FCSTD DOCUMENT  (FreeCAD 0.21R33771 (Git))
Label: RaspberryPi_Pico_Variations
Comment: https://gitlab.com/recursivenomad/ki-lime-pi-pico/
License: MIT-0 OR CC0-1.0
LicenseURL: https://opensource.org/license/mit-0/
objects: App::Link×368, App::LinkElement×80, App::DocumentObjectGroup×37, App::Part×36, PartDesign::Pad×35, Part::Compound×32, Sketcher::SketchObject×29, PartDesign::Mirrored×25, Part::Part2DObjectPython×21, PartDesign::LinearPattern×21, PartDesign::Pocket×16, PartDesign::Body×15, Part::FeaturePython×15, Part::Box×14, PartDesign::MultiTransform×11, Spreadsheet::Sheet×7, PartDesign::Point×5, Part::MultiFuse×5, Part::Cut×4, PartDesign::Fillet×3, +7 more types

FEATURE [Sketcher::SketchObject] Sketch  label="Sketch_Header_BodyQuadrant"
  FullyConstrained = true
  MapMode = 5
  Support = -> [XY_Plane005]
  expr: Constraints[15] = Spreadsheet002.InsulationEdgeToPin
  expr: Constraints[16] = <<vHeader>>.InsulationWidth
  expr: Constraints[29] = <<vPico>>.PinPitch * 2
  expr: Constraints[30] = Spreadsheet002.BodyOuterCrossbarInset + <<vHeader>>.InsulationWidth / 2
  expr: Constraints[32] = <<vPico>>.BoardWidth / 2 - <<vPico>>.PinInset
  expr: Constraints[33] = (<<vPico>>.PinDIPCount / 4 - 0.5) * <<vPico>>.PinPitch
  sketch-geometry (12):
    g0: LineSegment StartX=-10.16 StartY=25 StartZ=0 EndX=-7.62 EndY=25 EndZ=0
    g1: LineSegment StartX=-7.62 StartY=25 StartZ=0 EndX=-7.62 EndY=20.066 EndZ=0
    g2: LineSegment StartX=-7.62 StartY=20.066 StartZ=0 EndX=0 EndY=20.066 EndZ=0
    g3: LineSegment StartX=-10.16 StartY=25 StartZ=0 EndX=-10.16 EndY=0 EndZ=0
    g4: LineSegment StartX=-7.62 StartY=17.526 StartZ=0 EndX=0 EndY=17.526 EndZ=0
    g5: LineSegment StartX=-7.62 StartY=17.526 StartZ=0 EndX=-7.62 EndY=2.54 EndZ=0
    g6: LineSegment StartX=-7.62 StartY=2.54 StartZ=0 EndX=0 EndY=2.54 EndZ=0
    g7: LineSegment StartX=-8.89 StartY=24.13 StartZ=0 EndX=-8.89 EndY=25 EndZ=0
    g8: LineSegment StartX=-10.16 StartY=0 StartZ=0 EndX=0 EndY=0 EndZ=0
    g9: LineSegment StartX=0 StartY=0 StartZ=0 EndX=0 EndY=2.54 EndZ=0
    g10: LineSegment StartX=0 StartY=17.526 StartZ=0 EndX=0 EndY=20.066 EndZ=0
    g11: GeomPoint X=-8.89 Y=19.05 Z=0
  constraints (34):
    c: Coincident(g1,g0)
    c: Coincident(g2,g1)
    c: Coincident(g3,g0)
    c: Coincident(g5,g4)
    c: Coincident(g6,g5)
    c: Vertical(g3)
    c: Perpendicular(g0,g3)
    c: Parallel(g1,g3)
    c: PointOnObject(g4,g1)
    c: Parallel(g5,g3)
    c: Perpendicular(g3,g2)
    c: Parallel(g4,g2)
    c: Parallel(g6,g2)
    c: Perpendicular(g0,g7)
    c: Symmetric(g0,g0,g7)
    c: Distance(g7) = 0.87
    c: Distance(g0) = 2.54
    c: PointOnObject(g2,g-2)
    c: PointOnObject(g4,g-2)
    c: PointOnObject(g6,g-2)
    c: PointOnObject(g3,g-1)
    c: Coincident(g8,g3)
    c: Coincident(g8,g-1)
    c: Coincident(g9,g8)
    c: Coincident(g9,g6)
    c: Coincident(g10,g4)
    c: Coincident(g10,g2)
    c: Equal(g0,g10)
    c: PointOnObject(g11,g7)
    c: Distance(g7,g11) = 5.08
    c: Distance(g11,g4) = 1.524
    c: Equal(g9,g0)
    c: Distance(g7,g-2) = 8.89
    c: Distance(g7,g-1) = 24.13
FEATURE [PartDesign::Pad] Pad  label="Pad_Header_BodyQuadrant"
  Direction = (0,0,1)
  Length = 2.54
  Length2 = 10
  Profile = -> Sketch
  ReferenceAxis = -> Sketch [N_Axis]
  Type = 0
  expr: Length = <<vHeader>>.InsulationThickness
FEATURE [PartDesign::Mirrored] Mirrored  label="Mirror_Header_BodyQuarter"
  MirrorPlane = -> Sketch [V_Axis]
FEATURE [PartDesign::Mirrored] Mirrored001  label="Mirror_Header_BodyHalf"
  MirrorPlane = -> Sketch [H_Axis]
FEATURE [PartDesign::MultiTransform] MultiTransform  label="MultiMirror_Header_Body"
  BaseFeature = -> Pad
  Originals = -> [Pad]
  Refine = true
  Transformations = -> [Mirrored,Mirrored001]
FEATURE [PartDesign::Body] Body  label="Header_Body"
  Group = -> [Sketch,Pad,MultiTransform,Mirrored,Mirrored001]
  Origin = -> Origin005
  Tip = -> MultiTransform
FEATURE [Spreadsheet::Sheet] Spreadsheet001  label="vPico"
  cells = A1='Board Thickness; B1(BoardThickness)=1; D1='Board Corner Radius; E1(BoardCornerRadius)=0.5; G1='C1 Placement; H1='C2 Placement; I1='D1 Placement; J1='D2 Placement; K1='J1 Placement; L1='L1 Placement; M1='Q1 Placement; N1='SW1 Placement; O1='U1 Placement; P1='U2 Placement; Q1='U3 Placement; R1='X1 Placement; A2='Board Width; B2(BoardWidth)=21; D2='Board Mounting Hole Diameter; E2(BoardMountingHoleDiameter)=2.1; G2(C1Placement)==create(<<placement>>; create(<<vector>>; 2.9; 17.1; 0); create(<<rotation>>; 0; 0; 0)); H2(C2Placement)==create(<<placement>>; create(<<vector>>; 2.9; 12.1; 0); create(<<rotation>>; 0; 0; 0)); I2(D1Placement)==create(<<placement>>; create(<<vector>>; 6; 18.9; 0); create(<<rotation>>; 0; 0; 0)); J2(D2Placement)==create(<<placement>>; create(<<vector>>; -5.7; 20.7; 0); create(<<rotation>>; 0; 0; 0)); K2(J1Placement)==create(<<placement>>; create(<<vector>>; 0; BoardLength / 2 + 1.3 - .J1TabPortrusion.y - .J1BodySize.y / 2; 0); create(<<rotation>>; 0; 0; 0)); L2(L1Placement)==create(<<placement>>; create(<<vector>>; 6; 14.6; 0); create(<<rotation>>; 0; 0; 0)); M2(Q1Placement)==create(<<placement>>; create(<<vector>>; 6.4; 7.2; 0); create(<<rotation>>; 0; 0; 0)); N2(SW1Placement)==create(<<placement>>; create(<<vector>>; -3.5; 13.5; 0); create(<<rotation>>; 0; 0; 0)); O2(U1Placement)==create(<<placement>>; create(<<vector>>; 0; -0.5; 0); create(<<rotation>>; 0; 0; 0)); P2(U2Placement)==create(<<placement>>; create(<<vector>>; 2.9; 14.6; 0); create(<<rotation>>; 180; 0; 0)); Q2(U3Placement)==create(<<placement>>; create(<<vector>>; -3.8; 6.4; 0); create(<<rotation>>; 90; 0; 0)); R2(X1Placement)==create(<<placement>>; create(<<vector>>; -2.3; -9.05; 0); create(<<rotation>>; 0; 0; 0)); A3='Board Length; B3(BoardLength)=51; D3='Board Mounting Hole Margin Diameter; E3(BoardMountingHoleMarginDiameter)=3.8; G4='C1 Size; H4='C2 Size; I4='D1 Base Size; J4='D2 Base Size; K4='J1 Body Size; L4='L1 Size; M4='Q1 Size; N4='SW1 Base Size; O4='U1 Size; P4='U2 Size; Q4='U3 Size; R4='X1 Size; A5='Pin Pitch; B5(PinPitch)=2.54; D5='Pin Hole Diameter; E5(PinHoleDiameter)=1; G5(C1Size)==create(<<vector>>; 2; 1.25; 1.25); H5(C2Size)==C1Size; I5(D1BaseSize)==create(<<vector>>; 1.65; 2.7; 0.95); J5(D2BaseSize)==create(<<vector>>; 1.6; 0.8; 0.3); K5(J1BodySize)==create(<<vector>>; 7.5; 5; 2.45); L5(L1Size)==create(<<vector>>; 2; 2.5; 1.2); M5(Q1Size)==create(<<vector>>; 1.6; 0.8; 0.8); N5(SW1BaseSize)==create(<<vector>>; 3.2; 4.25; 1.6); O5(U1Size)==create(<<vector>>; 7; 7; 0.9); P5(U2Size)==create(<<vector>>; 2.5; 2.5; 0.75); Q5(U3Size)==create(<<vector>>; 3; 2; 0.6); R5(X1Size)==create(<<vector>>; 3.2; 2.5; 0.6); A6='Pin DIP Count; B6(PinDIPCount)=40; D6='Pin Pad Width; E6(PinPadWidth)=1.6; K6='// J1 part was potentially listed incorrectly on Pico datasheet schematic; listed part name in FreeCAD tree as possible true part; D7='Pin Square Pad Radius; E7(PinSquarePadRadius)=0.2; I7='D1 Lead Offset; J7='D2 Lens Offset; K7='J1 Cavity Base Width; N7='SW1 Button Offset; A8='TP AB Radius; B8(TPABRadius)=0.55; D8='Pin Inset; E8(PinInset)=1.61; I8(D1LeadOffset)==create(<<vector>>; 0; (.D1BaseSize.y + .D1LeadSize.y) / 2; 0); J8(D2LensOffset)==create(<<vector>>; 0; 0; .D2BaseSize.z); K8(J1CavityBaseWidth)=5.4; N8(SW1ButtonOffset)==create(<<vector>>; 0; 0; .SW1BaseSize.z); A9='TP AB Height; B9(TPABHeight)=1.8; D9='Pin Inset Debug; E9(PinInsetDebug)=1.6; A10='TP CD Radius; B10(TPCDRadius)=0.525; D10='Pin To Castellation Center; E10(PinToCastellationCenter)=1.6; I10='D1 Lead Size; J10='D2 Lens Size; K10='J1 Cavity Fillet Radius; N10='SW1 Button Size; A11='TP CD Height; B11(TPCDHeight)=1.45; D11='Pin Hole Rows; E11(PinHoleRows)=2; F11='// 3 so pads extend linearly over edge for cleaner model; I11(D1LeadSize)==create(<<vector>>; 0.9; (3.6 - .D1BaseSize.y) / 2; 0.15); J11(D2LensSize)==create(<<vector>>; 1; 0.8; 0.3); K11(J1CavityFilletRadius)=0.25; N11(SW1ButtonSize)==create(<<vector>>; 2.25; 1.15 + 2.25; 0.9); A13='TP Radius; B13(TPRadius)=0.3; D13='Debug Center; E13(DebugCenter)==create(<<vector>>; 0; -BoardLength / 2 + PinInsetDebug; 0); J13='D2 Phosphor Offset; K13='J1 Cavity Side Height; N13='SW1 Button Fillet Radius; A14='TP Width; B14(TPWidth)=1.5; D14='Debug Pad Depth; E14(DebugPadDepth)==BoardThickness; J14(D2PhosphorOffset)==create(<<vector>>; 0; 0; .D2BaseSize.z); K14(J1CavitySideHeight)=1.1; N14(SW1ButtonFilletRadius)=0.5; D15='Debug Square Pin Index; E15(DebugSquarePinIndex)=1; J16='D2 Phosphor Size; K16='J1 Shell Thickness; A17='TP Pos A; B17(TPPosA)==create(<<vector>>; 7.775; 49.5); J17(D2PhosphorSize)==create(<<vector>>; 0.1; 0.1; 0.075); K17(J1ShellThickness)=0.3; A18='TP Pos B; B18(TPPosB)==create(<<vector>>; 13.225; 49.5); J18='// ESTIMATE; A19='TP Pos C; B19(TPPosC)==create(<<vector>>; 8.075; 46.47); K19='J1 Tab Portrusion; A20='TP Pos D; B20(TPPosD)==create(<<vector>>; 12.925; 46.47); K20(J1TabPortrusion)==create(<<vector>>; 0; 5.6 - .J1BodySize.y; 0.3); A21='TP Pos 1; B21(TPPos1)==create(<<vector>>; 10.5; 46.5); A22='TP Pos 2; B22(TPPos2)==create(<<vector>>; 9.5; 49.8); K22='J1 Tab Inset; A23='TP Pos 3; B23(TPPos3)==create(<<vector>>; 11.5; 49.8); K23(J1TabInset)=0.05; A24='TP Pos 4; B24(TPPos4)==create(<<vector>>; 8; 43); A25='TP Pos 5; B25(TPPos5)==create(<<vector>>; 8; 40.5); K25='J1 Tab Angle; A26='TP Pos 6; B26(TPPos6)==create(<<vector>>; 8; 38); K26(J1TabAngle)=45; K28='J1 Tab Widths; A29='Board Mounting Hole Inset; B29(BoardMountingHoleInset)==create(<<vector>>; 4.8; 2; 0); K29(J1TabWidths)==create(<<vector>>; 6.2; 5.1; 0.65); K31='J1 Tab Fillet Radius; K32(J1TabFilletRadius)=0.2
FEATURE [Spreadsheet::Sheet] Spreadsheet002  label="vHeader"
  cells = A1='Pin Length; B1(PinLength)=10.525; A2='Pin Width; B2(PinWidth)=0.635; A3='Pin Base Width; B3(PinBaseWidth)=0.3175; A4='Pin Tip Length; B4(PinTipLength)=0.635; A5='Pin Interface Length; B5(PinInterfaceLength)=6.35; A7='Insulation Thickness; B7(InsulationThickness)=2.54; A8='Insulation Width; B8(InsulationWidth)=2.54; A9='Insulation Edge To Pin; B9(InsulationEdgeToPin)=0.87; A10='Outer Crossbar Inset; B10(BodyOuterCrossbarInset)=0.254
FEATURE [Spreadsheet::Sheet] Spreadsheet003  label="vSocket"
  cells = A1='Body Height; B1(BodyHeight)=8.46; A2='Body Width; B2(BodyWidth)=2.54; A4='Standoff Width; B4(StandoffWidth)==BodyWidth / 4; A5='Standoff Depth; B5(StandoffDepth)==StandoffWidth; A7='Hole Width; B7(HoleWidth)=0.85; A8='Hole Guide Angle; B8(HoleGuideAngle)=45; A9='Hole Margin; B9(HoleMargin)=0.4; A11='Pin Length; B11(PinLength)=3.175; A12='Pin Width; B12(PinWidth)=0.635; A13='Pin Thickness; B13(PinThickness)=0.4; A14='Pin Base Width; B14(PinBaseWidth)=0.3175; A15='Pin Base Height; B15(PinBaseHeight)==PinBaseWidth; A17='Insertion Depth; B17(InsertionDepth)=6.35; A19='Part Prefix; B19(PartPrefix)='DIP-40_W17.78mm_H8.51mm; A20='Part Name; B20(PartName)==PartPrefix + <<_Socket>>
FEATURE [Sketcher::SketchObject] Sketch002  label="Sketch_SocketBody"
  AttachmentOffset = pos=(-8.89,0,0) rot=(0,0,1;0rad)
  FullyConstrained = true
  MapMode = 5
  Placement = pos=(-8.89,0,0) rot=(1,0,0;1.5708rad)
  Support = -> [XZ_Plane007]
  expr: .AttachmentOffset.Base.x = -(<<vPico>>.BoardWidth / 2 - <<vPico>>.PinInset)
  expr: Constraints[21] = <<vSocket>>.StandoffWidth
  expr: Constraints[22] = <<vSocket>>.StandoffDepth
  expr: Constraints[7] = <<vSocket>>.BodyWidth
  expr: Constraints[8] = <<vSocket>>.BodyHeight
  sketch-geometry (9):
    g0: LineSegment StartX=0 StartY=8.46 StartZ=0 EndX=0 EndY=0 EndZ=0
    g1: LineSegment StartX=-1.27 StartY=0 StartZ=0 EndX=-1.27 EndY=8.46 EndZ=0
    g2: LineSegment StartX=-1.27 StartY=8.46 StartZ=0 EndX=1.27 EndY=8.46 EndZ=0
    g3: LineSegment StartX=1.27 StartY=8.46 StartZ=0 EndX=1.27 EndY=0 EndZ=0
    g4: LineSegment StartX=-1.27 StartY=0 StartZ=0 EndX=-0.635 EndY=0 EndZ=0
    g5: LineSegment StartX=-0.635 StartY=0 StartZ=0 EndX=-0.635 EndY=0.635 EndZ=0
    g6: LineSegment StartX=-0.635 StartY=0.635 StartZ=0 EndX=0.635 EndY=0.635 EndZ=0
    g7: LineSegment StartX=0.635 StartY=0.635 StartZ=0 EndX=0.634999 EndY=0 EndZ=0
    g8: LineSegment StartX=0.634999 StartY=0 StartZ=0 EndX=1.27 EndY=0 EndZ=0
  constraints (25):
    c: Vertical(g0)
    c: PointOnObject(g1,g-1)
    c: Coincident(g2,g1)
    c: Coincident(g3,g2)
    c: Symmetric(g1,g3,g0)
    c: Perpendicular(g-1,g1)
    c: Perpendicular(g-1,g3)
    c: Distance(g2) = 2.54
    c: Distance(g1) = 8.46
    c: Parallel(g2,g-1)
    c: Coincident(g4,g1)
    c: Coincident(g5,g4)
    c: Coincident(g6,g5)
    c: PointOnObject(g7,g-1)
    c: Coincident(g8,g7)
    c: Coincident(g8,g3)
    c: PointOnObject(g4,g-1)
    c: Coincident(g6,g7)
    c: Symmetric(g5,g6,g0)
    c: Equal(g7,g5)
    c: Perpendicular(g4,g5)
    c: Distance(g4) = 0.635
    c: Distance(g5) = 0.635
    c: PointOnObject(g0,g2)
    c: Coincident(g0,g-1)
FEATURE [PartDesign::Pad] Pad002  label="Pad_Socket_Body"
  Direction = (0,-1,-2e-16)
  Length = 51.6
  Length2 = 10
  Midplane = true
  Placement = pos=(0,0,0) rot=(1,0,0;1.5708rad)
  Profile = -> Sketch002
  ReferenceAxis = -> Sketch002 [N_Axis]
  Type = 0
  expr: Length = <<vPico>>.PinPitch * <<vPico>>.PinDIPCount / 2 + <<vSocket>>.HoleMargin * 2
FEATURE [Sketcher::SketchObject] Sketch003  label="Sketch_SocketHole"
  AttachmentOffset = pos=(-8.89,24.13,8.46) rot=(0,0,1;0rad)
  FullyConstrained = true
  MapMode = 5
  Placement = pos=(-8.89,24.13,8.46) rot=(0,0,1;0rad)
  Support = -> [XY_Plane007]
  expr: .AttachmentOffset.Base.x = -(<<vPico>>.BoardWidth / 2 - <<vPico>>.PinInset)
  expr: .AttachmentOffset.Base.y = (<<vPico>>.PinDIPCount / 4 - 0.5) * <<vPico>>.PinPitch
  expr: .AttachmentOffset.Base.z = <<vSocket>>.BodyHeight
  expr: Constraints[9] = <<vSocket>>.HoleWidth
  sketch-geometry (5):
    g0: LineSegment StartX=0.425 StartY=-0.425 StartZ=0 EndX=0.425 EndY=0.425 EndZ=0
    g1: LineSegment StartX=0.425 StartY=0.425 StartZ=0 EndX=-0.425 EndY=0.425 EndZ=0
    g2: LineSegment StartX=-0.425 StartY=0.425 StartZ=0 EndX=-0.425 EndY=-0.425 EndZ=0
    g3: LineSegment StartX=-0.425 StartY=-0.425 StartZ=0 EndX=0.425 EndY=-0.425 EndZ=0
    g4: GeomPoint X=0 Y=0 Z=0
  constraints (12):
    c: Coincident(g0,g1)
    c: Coincident(g1,g2)
    c: Coincident(g2,g3)
    c: Coincident(g3,g0)
    c: Perpendicular(g3,g0)
    c: Parallel(g0,g2)
    c: Parallel(g3,g1)
    c: Equal(g0,g3)
    c: Vertical(g0)
    c: Distance(g1) = 0.85
    c: Symmetric(g2,g0,g4)
    c: Coincident(g4,g-1)
FEATURE [PartDesign::Pocket] Pocket  label="Pocket_Socket_Hole"
  BaseFeature = -> Pad002
  Direction = (0,0,-1)
  Length = 6.35
  Length2 = 5
  Placement = pos=(0,0,0) rot=(1,0,0;1.5708rad)
  Profile = -> Sketch003
  ReferenceAxis = -> Sketch003 [N_Axis]
  Type = 0
  expr: Length = <<vSocket>>.InsertionDepth
FEATURE [Part::Box] Box  label="Cube_U1"
  AttacherType = Attacher::AttachEngine3D
  Height = 0.9
  Length = 7
  Placement = pos=(-3.5,-3.5,0) rot=(0,0,1;0rad)
  Width = 7
  expr: .Placement.Base.x = -Length / 2
  expr: .Placement.Base.y = -Width / 2
  expr: Height = <<U1>>.Metadata_Dimensions.z
  expr: Label = <<Cube_>> + <<U1>>.Label
  expr: Length = <<U1>>.Metadata_Dimensions.x
  expr: Width = <<U1>>.Metadata_Dimensions.y
FEATURE [App::DocumentObjectGroup] Group001  label="U1"
  Metadata_Dimensions = (7,7,0.9)
  Metadata_PartName = RP2040
  Metadata_Placement = pos=(0,-0.5,0) rot=(0,0,1;0rad)
  expr: Metadata_Dimensions = <<vPico>>.U1Size
  expr: Metadata_Placement = <<vPico>>.U1Placement
FEATURE [Part::Box] Box001  label="Cube_U2"
  AttacherType = Attacher::AttachEngine3D
  Height = 0.75
  Length = 2.5
  Placement = pos=(-1.25,-1.25,0) rot=(0,0,1;0rad)
  Width = 2.5
  expr: .Placement.Base.x = -Length / 2
  expr: .Placement.Base.y = -Width / 2
  expr: Height = <<U2>>.Metadata_Dimensions.z
  expr: Label = <<Cube_>> + <<U2>>.Label
  expr: Length = <<U2>>.Metadata_Dimensions.x
  expr: Width = <<U2>>.Metadata_Dimensions.y
FEATURE [App::DocumentObjectGroup] Group002  label="U2"
  Metadata_Dimensions = (2.5,2.5,0.75)
  Metadata_PartName = RT6150B-33GQW
  Metadata_Placement = pos=(2.9,14.6,0) rot=(0,0,1;3.14159rad)
  expr: Metadata_Dimensions = <<vPico>>.U2Size
  expr: Metadata_Placement = <<vPico>>.U2Placement
FEATURE [Part::Box] Box002  label="Cube_U3"
  AttacherType = Attacher::AttachEngine3D
  Height = 0.6
  Length = 3
  Placement = pos=(-1.5,-1,0) rot=(0,0,1;0rad)
  Width = 2
  expr: .Placement.Base.x = -Length / 2
  expr: .Placement.Base.y = -Width / 2
  expr: Height = <<U3>>.Metadata_Dimensions.z
  expr: Label = <<Cube_>> + <<U3>>.Label
  expr: Length = <<U3>>.Metadata_Dimensions.x
  expr: Width = <<U3>>.Metadata_Dimensions.y
FEATURE [App::DocumentObjectGroup] Group003  label="U3"
  Metadata_Dimensions = (3,2,0.6)
  Metadata_PartName = W25Q16JVUXIQ
  Metadata_Placement = pos=(-3.8,6.4,0) rot=(0,0,1;1.5708rad)
  expr: Metadata_Dimensions = <<vPico>>.U3Size
  expr: Metadata_Placement = <<vPico>>.U3Placement
FEATURE [Part::Box] Box003  label="Cube_X1"
  AttacherType = Attacher::AttachEngine3D
  Height = 0.6
  Length = 3.2
  Placement = pos=(-1.6,-1.25,0) rot=(0,0,1;0rad)
  Width = 2.5
  expr: .Placement.Base.x = -Length / 2
  expr: .Placement.Base.y = -Width / 2
  expr: Height = <<X1>>.Metadata_Dimensions.z
  expr: Label = <<Cube_>> + <<X1>>.Label
  expr: Length = <<X1>>.Metadata_Dimensions.x
  expr: Width = <<X1>>.Metadata_Dimensions.y
FEATURE [App::DocumentObjectGroup] Group004  label="X1"
  Metadata_Dimensions = (3.2,2.5,0.6)
  Metadata_PartName = X12M000000S096
  Metadata_Placement = pos=(-2.3,-9.05,0) rot=(0,0,1;0rad)
  expr: Metadata_Dimensions = <<vPico>>.X1Size
  expr: Metadata_Placement = <<vPico>>.X1Placement
FEATURE [Part::Box] Box006  label="Cube_Q1"
  AttacherType = Attacher::AttachEngine3D
  Height = 0.8
  Length = 1.6
  Placement = pos=(-0.8,-0.4,0) rot=(0,0,1;0rad)
  Width = 0.8
  expr: .Placement.Base.x = -Length / 2
  expr: .Placement.Base.y = -Width / 2
  expr: Height = <<Q1>>.Metadata_Dimensions.z
  expr: Label = <<Cube_>> + <<Q1>>.Label
  expr: Length = <<Q1>>.Metadata_Dimensions.x
  expr: Width = <<Q1>>.Metadata_Dimensions.y
FEATURE [App::DocumentObjectGroup] Group007  label="Q1"
  Metadata_Dimensions = (1.6,0.8,0.8)
  Metadata_PartName = DMG1012T
  Metadata_Placement = pos=(6.4,7.2,0) rot=(0,0,1;0rad)
  expr: Metadata_Dimensions = <<vPico>>.Q1Size
  expr: Metadata_Placement = <<vPico>>.Q1Placement
FEATURE [App::DocumentObjectGroup] Group008  label="D1"
  Metadata_Dimensions = (1.65,2.7,0.95)
  Metadata_LeadDimensions = (0.9,0.45,0.15)
  Metadata_LeadOffset = (0,1.575,0)
  Metadata_PartName = MBR120VLSFT1G
  Metadata_Placement = pos=(6,18.9,0) rot=(0,0,1;0rad)
  expr: Metadata_Dimensions = <<vPico>>.D1BaseSize
  expr: Metadata_LeadDimensions = <<vPico>>.D1LeadSize
  expr: Metadata_LeadOffset = <<vPico>>.D1LeadOffset
  expr: Metadata_Placement = <<vPico>>.D1Placement
FEATURE [App::DocumentObjectGroup] Group009  label="D2"
  Metadata_BodyDimensions = (1,0.8,0.3)
  Metadata_BodyOffset = (0,0,0.3)
  Metadata_Dimensions = (1.6,0.8,0.3)
  Metadata_PartName = QSME-C194
  Metadata_PhosphorDimensions = (0.1,0.1,0.075)
  Metadata_PhosphorOffset = (0,0,0.3)
  Metadata_Placement = pos=(-5.7,20.7,0) rot=(0,0,1;0rad)
  expr: Metadata_BodyDimensions = Spreadsheet001.D2LensSize
  expr: Metadata_BodyOffset = Spreadsheet001.D2LensOffset
  expr: Metadata_Dimensions = Spreadsheet001.J5
  expr: Metadata_PhosphorDimensions = <<vPico>>.D2PhosphorSize
  expr: Metadata_PhosphorOffset = <<vPico>>.D2PhosphorOffset
  expr: Metadata_Placement = <<vPico>>.D2Placement
FEATURE [App::DocumentObjectGroup] Group010  label="SW1"
  Metadata_ButtonDimensions = (2.25,3.4,0.9)
  Metadata_ButtonFilletRadius = 0.5
  Metadata_ButtonOffset = (0,0,1.6)
  Metadata_Dimensions = (3.2,4.25,1.6)
  Metadata_PartName = TP-1221U-K9K5325
  Metadata_Placement = pos=(-3.5,13.5,0) rot=(0,0,1;0rad)
  expr: Metadata_ButtonDimensions = <<vPico>>.SW1ButtonSize
  expr: Metadata_ButtonFilletRadius = <<vPico>>.SW1ButtonFilletRadius
  expr: Metadata_ButtonOffset = <<vPico>>.SW1ButtonOffset
  expr: Metadata_Dimensions = <<vPico>>.SW1BaseSize
  expr: Metadata_Placement = <<vPico>>.SW1Placement
FEATURE [Part::Box] Box010  label="Cube_L1"
  AttacherType = Attacher::AttachEngine3D
  Height = 1.2
  Length = 2
  Placement = pos=(-1,-1.25,0) rot=(0,0,1;0rad)
  Width = 2.5
  expr: .Placement.Base.x = -Length / 2
  expr: .Placement.Base.y = -Width / 2
  expr: Height = <<L1>>.Metadata_Dimensions.z
  expr: Label = <<Cube_>> + <<L1>>.Label
  expr: Length = <<L1>>.Metadata_Dimensions.x
  expr: Width = <<L1>>.Metadata_Dimensions.y
FEATURE [App::DocumentObjectGroup] Group011  label="L1"
  Metadata_Dimensions = (2,2.5,1.2)
  Metadata_PartName = 2u2
  Metadata_Placement = pos=(6,14.6,0) rot=(0,0,1;0rad)
  expr: Metadata_Dimensions = <<vPico>>.L1Size
  expr: Metadata_Placement = <<vPico>>.L1Placement
FEATURE [Sketcher::SketchObject] Sketch008  label="Sketch_SW1_Button"
  AttachmentOffset = pos=(0,0,1.6) rot=(0,0,1;0rad)
  FullyConstrained = true
  MapMode = 5
  Placement = pos=(0,0,1.6) rot=(0,0,1;0rad)
  Support = -> [XY_Plane023]
  expr: .AttachmentOffset.Base = <<vPico>>.SW1ButtonOffset
  expr: Constraints[7] = <<SW1>>.Metadata_ButtonDimensions.x
  expr: Constraints[8] = <<SW1>>.Metadata_ButtonDimensions.y - <<SW1>>.Metadata_ButtonDimensions.x
  expr: Label = <<Sketch_>> + <<SW1>>.Label + <<_Button>>
  sketch-geometry (4):
    g0: ArcOfCircle CenterX=-5.4893e-12 CenterY=0.575 CenterZ=0 NormalX=0 NormalY=0 NormalZ=1 AngleXU=0 Radius=1.125 StartAngle=-1.8616e-12 EndAngle=3.14159
    g1: ArcOfCircle CenterX=-5.5915e-12 CenterY=-0.575 CenterZ=0 NormalX=0 NormalY=0 NormalZ=1 AngleXU=0 Radius=1.125 StartAngle=3.14159 EndAngle=6.28319
    g2: LineSegment StartX=-1.125 StartY=0.575 StartZ=0 EndX=-1.125 EndY=-0.575 EndZ=0
    g3: LineSegment StartX=1.125 StartY=-0.575 StartZ=0 EndX=1.125 EndY=0.575 EndZ=0
  constraints (9):
    c: Tangent(g0,g2) = -1.5708
    c: Tangent(g2,g1) = -1.5708
    c: Tangent(g1,g3) = -1.5708
    c: Tangent(g3,g0) = -1.5708
    c: Equal(g0,g1)
    c: Symmetric(g1,g0,g-1)
    c: Vertical(g2)
    c: Distance(g1,g1) = 2.25
    c: Distance(g2) = 1.15
FEATURE [Spreadsheet::Sheet] Spreadsheet004  label="vPicoW"
  cells = A1='Lower Mounting Hole Margin Diameter; B1(LowerMountingHoleMarginDiameter)=3; C1='// ESTIMATE; E1='C1 Placement; F1='C2 Placement; G1='C21 Placement; H1='Q1 Placement; I1='SH1 Placement; J1='U1 Placement; K1='U2 Placement; L1='U3 Placement; M1='X1 Placement; A2='Debug Center; B2(DebugCenter)==create(<<vector>>; 13.6241 - <<vPico>>.BoardWidth / 2; 19.8 - <<vPico>>.BoardLength / 2; 0); E2(C1Placement)==create(<<placement>>; create(<<vector>>; 1.9; 18.07; 0); create(<<rotation>>; 0; 0; 0)); F2(C2Placement)==create(<<placement>>; create(<<vector>>; 2.01; 10.79; 0); create(<<rotation>>; 0; 0; 0)); G2(C21Placement)==create(<<placement>>; create(<<vector>>; 2.01; 9.07; 0); create(<<rotation>>; 0; 0; 0)); H2(Q1Placement)==create(<<placement>>; create(<<vector>>; 6.49; 7.76; 0); create(<<rotation>>; 0; 0; 0)); I2(SH1Placement)==create(<<placement>>; create(<<vector>>; 0; -12.3; 0); create(<<rotation>>; 0; 0; 0)); J2(U1Placement)==create(<<placement>>; create(<<vector>>; 0; 1.55; 0); create(<<rotation>>; 0; 0; 0)); K2(U2Placement)==create(<<placement>>; create(<<vector>>; 2.3; 14.6; 0); create(<<rotation>>; 90; 0; 0)); L2(U3Placement)==create(<<placement>>; create(<<vector>>; -3.32; 8.69; 0); create(<<rotation>>; 0; 0; 0)); M2(X1Placement)==create(<<placement>>; create(<<vector>>; -4.7; -4.91; 0); create(<<rotation>>; 0; 0; 0)); A3='Debug Square Pin Index; B3(DebugSquarePinIndex)=0; G4='C21 Size; I4='SH1 Size; K4='U2 Size; G5(C21Size)==<<vPico>>.C1Size; I5(SH1Size)==create(<<vector>>; 12; 10; 1.7); K5(U2Size)==create(<<vector>>; 3; 4; 0.75)
FEATURE [Part::Box] Box014  label="Cube_SH1"
  AttacherType = Attacher::AttachEngine3D
  Height = 1.7
  Length = 12
  Placement = pos=(-6,-5,0) rot=(0,0,1;0rad)
  Width = 10
  expr: .Placement.Base.x = -Length / 2
  expr: .Placement.Base.y = -Width / 2
  expr: Height = <<SH1>>.Metadata_Dimensions.z
  expr: Label = <<Cube_>> + <<SH1>>.Label
  expr: Length = <<SH1>>.Metadata_Dimensions.x
  expr: Width = <<SH1>>.Metadata_Dimensions.y
FEATURE [App::DocumentObjectGroup] Group013  label="SH1"
  Metadata_Dimensions = (12,10,1.7)
  Metadata_PartName = CYW43439
  Metadata_Placement = pos=(0,-12.3,0) rot=(0,0,1;0rad)
  expr: Metadata_Dimensions = <<vPicoW>>.SH1Size
  expr: Metadata_Placement = <<vPicoW>>.SH1Placement
FEATURE [App::DocumentObjectGroup] Group014  label="J1"
  Metadata_Dimensions = (7.5,5,2.45)
  Metadata_PartName = 690T505-x62-01x
  Metadata_Placement = pos=(0,23.7,0) rot=(0,0,1;0rad)
  expr: Metadata_Dimensions = Spreadsheet001.K5
  expr: Metadata_Placement = <<vPico>>.J1Placement
FEATURE [Part::Box] Box016  label="Cube_J2"
  AttacherType = Attacher::AttachEngine3D
  Height = 2.9
  Length = 5
  Placement = pos=(-2.5,-2.125,0) rot=(0,0,1;0rad)
  Width = 4.25
  expr: .Placement.Base.x = -Length / 2
  expr: .Placement.Base.y = -Width / 2
  expr: Height = <<J2>>.Metadata_Dimensions.z
  expr: Label = <<Cube_>> + <<J2>>.Label
  expr: Length = <<J2>>.Metadata_Dimensions.x
  expr: Width = <<J2>>.Metadata_Dimensions.y
FEATURE [App::DocumentObjectGroup] Group015  label="J2"
  Metadata_Dimensions = (5,4.25,2.9)
  Metadata_PartName = BM03B-SRSS-TB
  Metadata_Placement = pos=(0,-23,0) rot=(0,0,1;0rad)
  expr: Metadata_Dimensions = <<vPicoH>>.J2Size
  expr: Metadata_Placement = <<vPicoH>>.J2Placement
FEATURE [Part::Thickness] Thickness  label="Thickness_J2"
  Faces = -> Box016 [Face3]
  Intersection = false
  Join = 2
  Mode = 1
  SelfIntersection = false
  Value = -0.4
  expr: Label = <<Thickness_>> + <<J2>>.Label
  expr: Value = -<<vPicoH>>.J2WallThickness
FEATURE [Sketcher::SketchObject] Sketch009  label="Sketch_USBPort_J1"
  FullyConstrained = true
  MapMode = 5
  Placement = pos=(0,0,0) rot=(1,0,0;1.5708rad)
  Support = -> [XZ_Plane028]
  expr: Constraints[10] = <<J1>>.Metadata_Dimensions.x
  expr: Constraints[14] = <<J1>>.Metadata_Dimensions.z
  expr: Constraints[34] = <<vPico>>.J1ShellThickness
  expr: Constraints[35] = <<vPico>>.J1CavitySideHeight
  expr: Constraints[36] = <<vPico>>.J1CavityBaseWidth
  sketch-geometry (13):
    g0: LineSegment StartX=-2.82426 StartY=0 StartZ=0 EndX=2.82426 EndY=0 EndZ=0
    g1: LineSegment StartX=-2.82426 StartY=0 StartZ=0 EndX=-3.75 EndY=0.925736 EndZ=0
    g2: LineSegment StartX=-3.75 StartY=0.925736 StartZ=0 EndX=-3.75 EndY=2.45 EndZ=0
    g3: LineSegment StartX=-3.75 StartY=2.45 StartZ=0 EndX=3.75 EndY=2.45 EndZ=0
    g4: LineSegment StartX=3.75 StartY=2.45 StartZ=0 EndX=3.75 EndY=0.925736 EndZ=0
    g5: LineSegment StartX=3.75 StartY=0.925736 StartZ=0 EndX=2.82426 EndY=0 EndZ=0
    g6: LineSegment StartX=-2.7 StartY=0.3 StartZ=0 EndX=2.7 EndY=0.3 EndZ=0
    g7: LineSegment StartX=-3.45 StartY=2.15 StartZ=0 EndX=-3.45 EndY=1.05 EndZ=0
    g8: LineSegment StartX=-3.45 StartY=2.15 StartZ=0 EndX=-3.45 EndY=2.45 EndZ=0
    g9: LineSegment StartX=-3.45 StartY=2.15 StartZ=0 EndX=-3.75 EndY=2.15 EndZ=0
    g10: LineSegment StartX=-3.45 StartY=1.05 StartZ=0 EndX=-3.66213 EndY=0.837868 EndZ=0
    g11: LineSegment StartX=-2.7 StartY=0.3 StartZ=0 EndX=-2.91213 EndY=0.087868 EndZ=0
    g12: LineSegment StartX=-2.7 StartY=0.3 StartZ=0 EndX=-2.7 EndY=0 EndZ=0
  constraints (37):
    c: Symmetric(g0,g0,g-2)
    c: Coincident(g1,g0)
    c: Coincident(g2,g1)
    c: Coincident(g3,g2)
    c: Coincident(g4,g3)
    c: Coincident(g5,g4)
    c: Coincident(g5,g0)
    c: Symmetric(g3,g2,g-2)
    c: Symmetric(g4,g1,g-2)
    c: Perpendicular(g3,g2)
    c: Distance(g3) = 7.5
    c: Symmetric(g6,g6,g-2)
    c: PointOnObject(g0,g-1)
    c: Parallel(g7,g2)
    c: Distance(g0,g3) = 2.45
    c: Coincident(g8,g7)
    c: PointOnObject(g8,g3)
    c: Coincident(g9,g7)
    c: PointOnObject(g9,g2)
    c: Coincident(g10,g7)
    c: PointOnObject(g10,g1)
    c: Coincident(g11,g6)
    c: PointOnObject(g11,g1)
    c: Coincident(g12,g6)
    c: PointOnObject(g12,g0)
    c: Perpendicular(g0,g12)
    c: Perpendicular(g1,g11)
    c: Perpendicular(g1,g10)
    c: Perpendicular(g2,g9)
    c: Perpendicular(g3,g8)
    c: Equal(g12,g11)
    c: Equal(g12,g10)
    c: Equal(g12,g9)
    c: Equal(g12,g8)
    c: Distance(g12) = 0.3
    c: Distance(g7) = 1.1
    c: Distance(g6) = 5.4
FEATURE [PartDesign::Pad] Pad007  label="Pad_USBPort_J1"
  Direction = (0,-1,-2e-16)
  Length = 5
  Length2 = 10
  Midplane = true
  Placement = pos=(0,0,0) rot=(1,0,0;1.5708rad)
  Profile = -> Sketch009
  ReferenceAxis = -> Sketch009 [N_Axis]
  Type = 0
  expr: Length = <<J1>>.Metadata_Dimensions.y
FEATURE [PartDesign::Fillet] Fillet001  label="Fillet_USBPort_J1"
  Base = -> Pad007 [Edge11,Edge14,Edge1,Edge8,Edge5,Edge2]
  BaseFeature = -> Pad007
  Placement = pos=(0,0,0) rot=(1,0,0;1.5708rad)
  Radius = 0.55
  SupportTransform = false
  UseAllEdges = false
  expr: Radius = <<vPico>>.J1CavityFilletRadius + <<vPico>>.J1ShellThickness
FEATURE [PartDesign::Thickness] Thickness001  label="Thickness_USBPort_J1"
  Base = -> Fillet001 [Face2]
  BaseFeature = -> Fillet001
  Intersection = true
  Join = 0
  Mode = 0
  Reversed = true
  SupportTransform = false
  Value = 0.3
  expr: Value = <<vPico>>.J1ShellThickness
FEATURE [Sketcher::SketchObject] Sketch010  label="Sketch_USBPort_J1_Tab1"
  AttachmentOffset = pos=(2.5,2.45,0) rot=(0,0,1;0rad)
  FullyConstrained = true
  MapMode = 5
  Placement = pos=(0,2.5,2.45) rot=(0.57735,0.57735,0.57735;2.0944rad)
  Support = -> [YZ_Plane028]
  expr: .AttachmentOffset.Base.x = <<J1>>.Metadata_Dimensions.y / 2
  expr: .AttachmentOffset.Base.y = <<J1>>.Metadata_Dimensions.z
  expr: Constraints[10] = <<vPico>>.J1ShellThickness
  expr: Constraints[14] = 90 + <<vPico>>.J1TabAngle
  expr: Constraints[15] = <<vPico>>.J1TabPortrusion.y
  expr: Constraints[17] = <<vPico>>.J1TabPortrusion.z
  sketch-geometry (7):
    g0: LineSegment StartX=0 StartY=-0.3 StartZ=0 EndX=0 EndY=0 EndZ=0
    g1: LineSegment StartX=0.087868 StartY=0 StartZ=0 EndX=0.387868 EndY=0.3 EndZ=0
    g2: LineSegment StartX=0 StartY=-0.3 StartZ=0 EndX=0.087868 EndY=-0.3 EndZ=0
    g3: LineSegment StartX=0.3 StartY=-0.212132 StartZ=0 EndX=0.6 EndY=0.087868 EndZ=0
    g4: LineSegment StartX=0.387868 StartY=0.3 StartZ=0 EndX=0.6 EndY=0.087868 EndZ=0
    g5: LineSegment StartX=0 StartY=0 StartZ=0 EndX=0.087868 EndY=0 EndZ=0
    g6: ArcOfCircle CenterX=0.087868 CenterY=0 CenterZ=0 NormalX=0 NormalY=0 NormalZ=1 AngleXU=0 Radius=0.3 StartAngle=4.71239 EndAngle=5.49779
  constraints (19):
    c: PointOnObject(g0,g-2)
    c: Coincident(g2,g0)
    c: Coincident(g4,g1)
    c: Coincident(g4,g3)
    c: Perpendicular(g4,g1)
    c: Parallel(g3,g1)
    c: Equal(g4,g0)
    c: Perpendicular(g0,g2)
    c: Coincident(g5,g0)
    c: Perpendicular(g0,g5)
    c: Distance(g0) = 0.3
    c: Tangent(g2,g6) = -1.5708
    c: Tangent(g3,g6) = -1.5708
    c: Coincident(g-1,g0)
    c: Angle(g1,g5) = 2.35619
    c: Distance(g3,g-2) = 0.6
    c: Coincident(g5,g1)
    c: Distance(g1,g-1) = 0.3
    c: PointOnObject(g6,g5)
FEATURE [Part::Part2DObjectPython] Clone2D  label="Clone_Sketch_USBPort_J1_Tab2"  # Draft 2D object (typed FeaturePython)
  AttachmentOffset = pos=(2.5,0,0) rot=(1,0,0;3.14159rad)
  Fuse = false
  MapMode = 5
  Objects = -> [Sketch010]
  Placement = pos=(6e-16,2.5,-6e-16) rot=(0.57735,0.57735,-0.57735;4.18879rad)
  Scale = (1,1,1)
  Support = -> [YZ_Plane028]
  expr: .AttachmentOffset.Base.x = <<J1>>.Metadata_Dimensions.y / 2
FEATURE [Part::Part2DObjectPython] Clone2D001  label="Clone_Sketch_USBPort_J1_Tab3"  # Draft 2D object (typed FeaturePython)
  AttachmentOffset = pos=(-3.75,2.5,1.52678) rot=(0,0,1;1.5708rad)
  Fuse = false
  MapMode = 5
  Objects = -> [Sketch010]
  Placement = pos=(-3.75,2.5,1.52678) rot=(0,0,1;1.5708rad)
  Scale = (1,1,1)
  Support = -> [XY_Plane028]
  expr: .AttachmentOffset.Base.x = -<<J1>>.Metadata_Dimensions.x / 2
  expr: .AttachmentOffset.Base.y = <<J1>>.Metadata_Dimensions.y / 2
  expr: .AttachmentOffset.Base.z = <<Point_SideTabCentre>>.Placement.Base.z
FEATURE [PartDesign::Pad] Pad008  label="Pad_USBPortTab1_J1"
  BaseFeature = -> Thickness001
  Direction = (1,-2e-16,3e-16)
  Length = 6.2
  Length2 = 10
  Midplane = true
  Profile = -> Sketch010
  ReferenceAxis = -> Sketch010 [N_Axis]
  Type = 0
  expr: Length = <<vPico>>.J1TabWidths.x
FEATURE [PartDesign::Pad] Pad009  label="Pad_USBPortTab2_J1"
  BaseFeature = -> Pad008
  Direction = (-1,1e-16,-4e-16)
  Length = 5.1
  Length2 = 10
  Midplane = true
  Profile = -> Clone2D
  ReferenceAxis = -> Clone2D [N_Axis]
  Type = 0
  expr: Length = <<vPico>>.J1TabWidths.y
FEATURE [PartDesign::Pad] Pad010  label="Pad_USBPortTab3_J1"
  BaseFeature = -> Pad009
  Direction = (0,0,1)
  Length = 0.65
  Length2 = 10
  Midplane = true
  Profile = -> Clone2D001
  ReferenceAxis = -> Clone2D001 [N_Axis]
  Type = 0
  expr: Length = <<vPico>>.J1TabWidths.z
FEATURE [PartDesign::Mirrored] Mirrored003  label="Mirrored_USBPortTab4_J1"
  BaseFeature = -> Pad010
  MirrorPlane = -> YZ_Plane028
  Originals = -> [Pad010]
FEATURE [PartDesign::Fillet] Fillet002  label="Fillet_USBPortTabs"
  Base = -> Mirrored003 [Edge158,Edge153,Edge127,Edge67,Edge47,Edge78,Edge89,Edge142]
  BaseFeature = -> Mirrored003
  Radius = 0.2
  Refine = true
  SupportTransform = false
  UseAllEdges = false
  expr: Radius = <<vPico>>.J1TabFilletRadius
FEATURE [PartDesign::Point] DatumPoint004  label="Point_SideTabCentre"
  AttacherType = Attacher::AttachEnginePoint
  MapMode = 37
  Placement = pos=(-3.75,2.5,1.52678) rot=(0,0,1;0rad)
  Support = -> [Fillet001]
FEATURE [PartDesign::Body] Body005  label="USBPort_J1"
  Group = -> [Sketch009,Pad007,Fillet001,DatumPoint004,Thickness001,Sketch010,Clone2D,Clone2D001,Pad008,Pad009,Pad010,Mirrored003,Fillet002]
  Origin = -> Origin028
  Tip = -> Fillet002
  expr: Label = <<USBPort_>> + <<J1>>.Label
FEATURE [Spreadsheet::Sheet] Spreadsheet005  label="vPicoH"
  cells = A1='Pin Hole Rows; B1(PinHoleRows)=1; E1='J2 Size; A2='TP1 Offset; B2(TP1Offset)==create(<<vector>>; -(<<vPico>>.TPPosD.x - <<vPico>>.TPCDRadius - (<<vPico>>.TPPosB.x - <<vPico>>.TPABRadius - <<vPico>>.TPPos3.x) - <<vPico>>.TPPos1.x); <<vPico>>.TPCDHeight / 2; 0); C2='// ESTIMATE; E2(J2Size)==create(<<vector>>; 5; 4.25; 2.9); A3='TP5 Offset; B3(TP5Offset)==create(<<vector>>; 0; -1.5); C3='// ESTIMATE; A4='TP Debug Center; B4(TPDebugCenter)==create(<<vector>>; 0; -<<vPico>>.BoardLength / 2 + 4; 0); C4='// ESTIMATE; E4='J2 Placement; A5='Debug Pad Depth; B5(DebugPadDepth)==<<vPico>>.BoardThickness / 2; E5(J2Placement)==create(<<placement>>; create(<<vector>>; 0; -23; 0); create(<<rotation>>; 0; 0; 0)); F5='// ESTIMATED PLACEMENT; E7='J2 Wall Thickness; E8(J2WallThickness)=0.4
FEATURE [Spreadsheet::Sheet] Spreadsheet006  label="vPicoWH"
  cells = A1='TP Debug Center; B1(TPDebugCenter)==<<vPicoW>>.DebugCenter; C1='// ESTIMATE; E1='J2 Placement; E2(J2Placement)==create(<<placement>>; create(<<vector>>; 3; -5 - <<vPicoH>>.J2Size.z / 2; <<vPicoH>>.J2Size.y / 2); create(<<rotation>>; 0; 0; -90)); F2='// ESTIMATED
FEATURE [App::DocumentObjectGroup] Group016  label="Boards"
  Metadata_DebugCenter = (0,-23.9,0)
  Metadata_DebugPadDepth = 1
  Metadata_LowerMountingHoleMarginDiameter = 3.8
  Metadata_TP1Offset = (0,0,0)
  Metadata_TP5Offset = 0
  expr: Metadata_DebugCenter = <<vPico>>.DebugCenter
  expr: Metadata_DebugPadDepth = <<vPico>>.DebugPadDepth
  expr: Metadata_LowerMountingHoleMarginDiameter = <<vPico>>.BoardMountingHoleMarginDiameter
FEATURE [App::DocumentObjectGroup] Group021  label="Pico"
FEATURE [Part::Box] Box017  label="Cube_U2_"
  AttacherType = Attacher::AttachEngine3D
  Height = 0.75
  Length = 3
  Placement = pos=(-1.5,-2,0) rot=(0,0,1;0rad)
  Width = 4
  expr: .Placement.Base.x = -Length / 2
  expr: .Placement.Base.y = -Width / 2
  expr: Height = <<U2_>>.Metadata_Dimensions.z
  expr: Label = <<Cube_>> + <<U2_>>.Label
  expr: Length = <<U2_>>.Metadata_Dimensions.x
  expr: Width = <<U2_>>.Metadata_Dimensions.y
FEATURE [App::DocumentObjectGroup] Group025  label="U2_"
  Metadata_Dimensions = (3,4,0.75)
  Metadata_PartName = RT6154AGQW
  Metadata_Placement = pos=(2.3,14.6,0) rot=(0,0,1;1.5708rad)
  expr: Metadata_Dimensions = <<vPicoW>>.U2Size
  expr: Metadata_Placement = <<vPicoW>>.U2Placement
FEATURE [PartDesign::AdditiveBox] Box018  label="Box_SW1_Base"
  AttacherType = Attacher::AttachEngine3D
  AttachmentOffset = pos=(-1.6,-2.125,0) rot=(0,0,1;0rad)
  Height = 1.6
  Length = 3.2
  MapMode = 5
  Placement = pos=(-1.6,-2.125,0) rot=(0,0,1;0rad)
  Support = -> [XY_Plane023]
  Width = 4.25
  expr: .AttachmentOffset.Base.x = -Length / 2
  expr: .AttachmentOffset.Base.y = -Width / 2
  expr: Height = <<SW1>>.Metadata_Dimensions.z
  expr: Label = <<Box_>> + <<SW1>>.Label + <<_Base>>
  expr: Length = <<SW1>>.Metadata_Dimensions.x
  expr: Width = <<SW1>>.Metadata_Dimensions.y
FEATURE [PartDesign::Pad] Pad006  label="Pad_SW1_Button"
  BaseFeature = -> Box018
  Direction = (0,0,1)
  Length = 0.9
  Length2 = 10
  Placement = pos=(-1.6,-2.125,0) rot=(0,0,1;0rad)
  Profile = -> Sketch008
  ReferenceAxis = -> Sketch008 [N_Axis]
  Type = 0
  expr: Label = <<Pad_>> + <<SW1>>.Label + <<_Button>>
  expr: Length = <<SW1>>.Metadata_ButtonDimensions.z
FEATURE [PartDesign::Fillet] Fillet  label="Fillet_SW1_Button"
  Base = -> Pad006 [Edge23]
  BaseFeature = -> Pad006
  Placement = pos=(-1.6,-2.125,0) rot=(0,0,1;0rad)
  Radius = 0.5
  SupportTransform = false
  UseAllEdges = false
  expr: Label = <<Fillet_>> + <<SW1>>.Label + <<_Button>>
  expr: Radius = <<SW1>>.Metadata_ButtonFilletRadius
FEATURE [PartDesign::Body] Body004  label="Body_SW1"
  Group = -> [Box018,Sketch008,Pad006,Fillet]
  Origin = -> Origin023
  Tip = -> Fillet
  expr: Label = <<Body_>> + <<SW1>>.Label
FEATURE [PartDesign::AdditiveBox] Box019  label="Box_D2_Lens"
  AttacherType = Attacher::AttachEngine3D
  AttachmentOffset = pos=(-0.5,-0.4,0.3) rot=(0,0,1;0rad)
  Height = 0.3
  Length = 1
  MapMode = 5
  Placement = pos=(-0.5,-0.4,0.3) rot=(0,0,1;0rad)
  Support = -> [XY_Plane044]
  Width = 0.8
  expr: .AttachmentOffset.Base.x = -Length / 2
  expr: .AttachmentOffset.Base.y = -Width / 2
  expr: .AttachmentOffset.Base.z = <<D2>>.Metadata_BodyOffset.z
  expr: Height = <<D2>>.Metadata_BodyDimensions.z
  expr: Label = <<Box_>> + <<D2>>.Label + <<_Lens>>
  expr: Length = <<D2>>.Metadata_BodyDimensions.x
  expr: Width = <<D2>>.Metadata_BodyDimensions.y
FEATURE [PartDesign::AdditiveBox] Box021  label="Box_D1_Package"
  AttacherType = Attacher::AttachEngine3D
  AttachmentOffset = pos=(-0.825,-1.35,0) rot=(0,0,1;0rad)
  Height = 0.95
  Length = 1.65
  MapMode = 5
  Placement = pos=(-0.825,-1.35,0) rot=(0,0,1;0rad)
  Support = -> [XY_Plane045]
  Width = 2.7
  expr: .AttachmentOffset.Base.x = -Length / 2
  expr: .AttachmentOffset.Base.y = -Width / 2
  expr: Height = <<D1>>.Metadata_Dimensions.z
  expr: Label = <<Box_>> + <<D1>>.Label + <<_Package>>
  expr: Length = <<D1>>.Metadata_Dimensions.x
  expr: Width = <<D1>>.Metadata_Dimensions.y
FEATURE [PartDesign::Body] Body011  label="Body_D1"
  Group = -> [Box021]
  Origin = -> Origin045
  Tip = -> Box021
  expr: Label = <<Body_>> + <<D1>>.Label
FEATURE [App::DocumentObjectGroup] Group034  label="DIP-40_W17.78mm_H8.51mm"
  expr: Label = <<vSocket>>.PartPrefix
FEATURE [Part::Box] Box023  label="D2_QSME-C194_Phosphor"
  AttacherType = Attacher::AttachEngine3D
  Height = 0.075
  Length = 0.1
  Placement = pos=(-0.05,-0.05,0.3) rot=(0,0,1;0rad)
  Width = 0.1
  expr: .Placement.Base.x = -Length / 2
  expr: .Placement.Base.y = -Width / 2
  expr: .Placement.Base.z = <<D2>>.Metadata_PhosphorOffset.z
  expr: Height = <<D2>>.Metadata_PhosphorDimensions.z
  expr: Label = <<D2>>.Label + <<_>> + <<D2>>.Metadata_PartName + <<_Phosphor>>
  expr: Length = <<D2>>.Metadata_PhosphorDimensions.x
  expr: Width = <<D2>>.Metadata_PhosphorDimensions.y
FEATURE [Part::Box] Box024  label="D2_QSME-C194_Base"
  AttacherType = Attacher::AttachEngine3D
  Height = 0.3
  Length = 1.6
  Placement = pos=(-0.8,-0.4,0) rot=(0,0,1;0rad)
  Width = 0.8
  expr: .Placement.Base.x = -Length / 2
  expr: .Placement.Base.y = -Width / 2
  expr: Height = <<D2>>.Metadata_Dimensions.z
  expr: Label = <<D2>>.Label + <<_>> + <<D2>>.Metadata_PartName + <<_Base>>
  expr: Length = <<D2>>.Metadata_Dimensions.x
  expr: Width = <<D2>>.Metadata_Dimensions.y
FEATURE [App::Link] Link092  label="D2_QSME-C194_Phosphor_Link"
  LinkTransform = true
  LinkedObject = -> Box023
  expr: Label = LinkedObject[0].Label + <<_Link>>
FEATURE [PartDesign::Boolean] Boolean  label="Boolean_Cut_D2_Lens"
  BaseFeature = -> Box019
  Group = -> [Box023]
  Type = 1
  expr: Label = <<Boolean_Cut_>> + <<D2>>.Label + <<_Lens>>
FEATURE [PartDesign::Body] Body010  label="D2_QSME-C194_Lens"
  Group = -> [Box019,Boolean]
  Origin = -> Origin044
  Tip = -> Boolean
  expr: Label = <<D2>>.Label + <<_>> + <<D2>>.Metadata_PartName + <<_Lens>>
FEATURE [App::Part] Part013  label="D2_QSME-C194"
  Group = -> [Group009,Box024,Link092,Body010]
  Origin = -> Origin020
  Placement = pos=(-5.7,20.7,0) rot=(0,0,1;0rad)
  expr: Label = <<D2>>.Label + <<_>> + <<D2>>.Metadata_PartName
  expr: Placement = <<D2>>.Metadata_Placement
FEATURE [App::DocumentObjectGroup] Group005  label="C1"
  Metadata_Dimensions = (2,1.25,1.25)
  Metadata_PartName = 47u
  Metadata_Placement = pos=(2.9,17.1,0) rot=(0,0,1;0rad)
  expr: Metadata_Dimensions = <<vPico>>.C1Size
  expr: Metadata_Placement = <<vPico>>.C1Placement
FEATURE [Part::Box] Box004  label="Cube_C1"
  AttacherType = Attacher::AttachEngine3D
  Height = 1.25
  Length = 2
  Placement = pos=(-1,-0.625,0) rot=(0,0,1;0rad)
  Width = 1.25
  expr: .Placement.Base.x = -Length / 2
  expr: .Placement.Base.y = -Width / 2
  expr: Height = <<C1>>.Metadata_Dimensions.z
  expr: Label = <<Cube_>> + <<C1>>.Label
  expr: Length = <<C1>>.Metadata_Dimensions.x
  expr: Width = <<C1>>.Metadata_Dimensions.y
FEATURE [Part::Compound] Compound006  label="C1_47u"
  Links = -> [Box004,Group005]
  Placement = pos=(2.9,17.1,0) rot=(0,0,1;0rad)
  expr: Label = <<C1>>.Label + <<_>> + <<C1>>.Metadata_PartName
  expr: Placement = <<C1>>.Metadata_Placement
FEATURE [App::Link] Link096  label="Pico_C1_47u"
  LinkPlacement = pos=(2.9,17.1,0) rot=(0,0,1;0rad)
  LinkedObject = -> Compound006
  Placement = pos=(2.9,17.1,0) rot=(0,0,1;0rad)
  expr: Label = <<Pico>>.Label + <<_>> + .LinkedObject.Label
  expr: Placement = <<vPico>>.C1Placement
FEATURE [Part::Box] Box025  label="Cube_C2"
  AttacherType = Attacher::AttachEngine3D
  Height = 1.25
  Length = 2
  Placement = pos=(-1,-0.625,0) rot=(0,0,1;0rad)
  Width = 1.25
  expr: .Placement.Base.x = -Length / 2
  expr: .Placement.Base.y = -Width / 2
  expr: Height = <<C2>>.Metadata_Dimensions.z
  expr: Label = <<Cube_>> + <<C2>>.Label
  expr: Length = <<C2>>.Metadata_Dimensions.x
  expr: Width = <<C2>>.Metadata_Dimensions.y
FEATURE [App::DocumentObjectGroup] Group038  label="C2"
  Metadata_Dimensions = (2,1.25,1.25)
  Metadata_PartName = 47u
  Metadata_Placement = pos=(2.9,12.1,0) rot=(0,0,1;0rad)
  expr: Metadata_Dimensions = <<vPico>>.C2Size
  expr: Metadata_Placement = <<vPico>>.C2Placement
FEATURE [Part::Compound] Compound008  label="C2_47u"
  Links = -> [Box025,Group038]
  Placement = pos=(2.9,12.1,0) rot=(0,0,1;0rad)
  expr: Label = <<C2>>.Label + <<_>> + <<C2>>.Metadata_PartName
  expr: Placement = <<C2>>.Metadata_Placement
FEATURE [Part::Box] Box026  label="Cube_C21"
  AttacherType = Attacher::AttachEngine3D
  Height = 1.25
  Length = 2
  Placement = pos=(-1,-0.625,0) rot=(0,0,1;0rad)
  Width = 1.25
  expr: .Placement.Base.x = -Length / 2
  expr: .Placement.Base.y = -Width / 2
  expr: Height = <<C21>>.Metadata_Dimensions.z
  expr: Label = <<Cube_>> + <<C21>>.Label
  expr: Length = <<C21>>.Metadata_Dimensions.x
  expr: Width = <<C21>>.Metadata_Dimensions.y
FEATURE [App::DocumentObjectGroup] Group039  label="C21"
  Metadata_Dimensions = (2,1.25,1.25)
  Metadata_PartName = 47u
  Metadata_Placement = pos=(2.01,9.07,0) rot=(0,0,1;0rad)
  expr: Metadata_Dimensions = <<vPicoW>>.C21Size
  expr: Metadata_Placement = <<vPicoW>>.C21Placement
FEATURE [Part::Compound] Compound009  label="C21_47u"
  Links = -> [Box026,Group039]
  Placement = pos=(2.01,9.07,0) rot=(0,0,1;0rad)
  expr: Label = <<C21>>.Label + <<_>> + <<C21>>.Metadata_PartName
  expr: Placement = <<C21>>.Metadata_Placement
FEATURE [App::Link] Link097  label="Pico_Board_Link"
  LinkedObject = -> Fusion
  expr: Label = <<Pico>>.Label + <<_Board>> + <<_Link>>
FEATURE [App::Link] Link098  label="Pico_C2_47u"
  LinkPlacement = pos=(2.9,12.1,0) rot=(0,0,1;0rad)
  LinkedObject = -> Compound008
  Placement = pos=(2.9,12.1,0) rot=(0,0,1;0rad)
  expr: Label = <<Pico>>.Label + <<_>> + .LinkedObject.Label
  expr: Placement = <<vPico>>.C2Placement
FEATURE [App::Link] Link100  label="Pico_D1_MBR120VLSFT1G"
  LinkPlacement = pos=(6,18.9,0) rot=(0,0,1;0rad)
  LinkedObject = -> Compound007
  Placement = pos=(6,18.9,0) rot=(0,0,1;0rad)
  expr: Label = <<Pico>>.Label + <<_>> + .LinkedObject.Label
  expr: Placement = <<vPico>>.D1Placement
FEATURE [App::Link] Link101  label="Pico_D2_QSME-C194"
  LinkPlacement = pos=(-5.7,20.7,0) rot=(0,0,1;0rad)
  LinkedObject = -> Part013
  Placement = pos=(-5.7,20.7,0) rot=(0,0,1;0rad)
  expr: Label = <<Pico>>.Label + <<_>> + .LinkedObject.Label
  expr: Placement = <<vPico>>.D2Placement
FEATURE [App::Link] Link102  label="Pico_J1_690T505-x62-01x"
  LinkPlacement = pos=(0,23.7,0) rot=(0,0,1;0rad)
  LinkedObject = -> Compound
  Placement = pos=(0,23.7,0) rot=(0,0,1;0rad)
  expr: Label = <<Pico>>.Label + <<_>> + .LinkedObject.Label
  expr: Placement = <<vPico>>.J1Placement
FEATURE [App::Link] Link104  label="Pico_L1_2u2"
  LinkPlacement = pos=(6,14.6,0) rot=(0,0,1;0rad)
  LinkedObject = -> Compound011
  Placement = pos=(6,14.6,0) rot=(0,0,1;0rad)
  expr: Label = <<Pico>>.Label + <<_>> + .LinkedObject.Label
  expr: Placement = <<vPico>>.L1Placement
FEATURE [App::Link] Link105  label="Pico_Q1_DMG1012T"
  LinkPlacement = pos=(6.4,7.2,0) rot=(0,0,1;0rad)
  LinkedObject = -> Compound012
  Placement = pos=(6.4,7.2,0) rot=(0,0,1;0rad)
  expr: Label = <<Pico>>.Label + <<_>> + .LinkedObject.Label
  expr: Placement = <<vPico>>.Q1Placement
FEATURE [App::Link] Link107  label="Pico_SW1_TP-1221U-K9K5325"
  LinkPlacement = pos=(-3.5,13.5,0) rot=(0,0,1;0rad)
  LinkedObject = -> Compound014
  Placement = pos=(-3.5,13.5,0) rot=(0,0,1;0rad)
  expr: Label = <<Pico>>.Label + <<_>> + .LinkedObject.Label
  expr: Placement = <<vPico>>.SW1Placement
FEATURE [App::Link] Link108  label="Pico_U1_RP2040"
  LinkPlacement = pos=(0,-0.5,0) rot=(0,0,1;0rad)
  LinkedObject = -> Compound015
  Placement = pos=(0,-0.5,0) rot=(0,0,1;0rad)
  expr: Label = <<Pico>>.Label + <<_>> + .LinkedObject.Label
  expr: Placement = <<vPico>>.U1Placement
FEATURE [App::Link] Link109  label="Pico_U2_RT6150B-33GQW"
  LinkPlacement = pos=(2.9,14.6,0) rot=(0,0,1;3.14159rad)
  LinkedObject = -> Compound016
  Placement = pos=(2.9,14.6,0) rot=(0,0,1;3.14159rad)
  expr: Label = <<Pico>>.Label + <<_>> + .LinkedObject.Label
  expr: Placement = <<vPico>>.U2Placement
FEATURE [App::Link] Link111  label="Pico_U3_W25Q16JVUXIQ"
  LinkPlacement = pos=(-3.8,6.4,0) rot=(0,0,1;1.5708rad)
  LinkedObject = -> Compound018
  Placement = pos=(-3.8,6.4,0) rot=(0,0,1;1.5708rad)
  expr: Label = <<Pico>>.Label + <<_>> + .LinkedObject.Label
  expr: Placement = <<vPico>>.U3Placement
FEATURE [App::Link] Link112  label="Pico_X1_X12M000000S096"
  LinkPlacement = pos=(-2.3,-9.05,0) rot=(0,0,1;0rad)
  LinkedObject = -> Compound019
  Placement = pos=(-2.3,-9.05,0) rot=(0,0,1;0rad)
  expr: Label = <<Pico>>.Label + <<_>> + .LinkedObject.Label
  expr: Placement = <<vPico>>.X1Placement
FEATURE [App::Part] Part030  label="Pico_Components"
  Group = -> [Link096,Link098,Link100,Link101,Link102,Link104,Link105,Link107,Link108,Link109,Link111,Link112]
  Origin = -> Origin043
  Placement = pos=(0,0,1) rot=(0,0,1;0rad)
  expr: .Placement.Base.z = <<vPico>>.BoardThickness
  expr: Label = <<Pico>>.Label + <<_Components>>
FEATURE [App::Part] Part024  label="RaspberryPi_Pico_STEP"
  Group = -> [Group021,Link097,Part030]
  License = MIT-0 (Public-domain-equivalent)
  LicenseURL = https://spdx.org/licenses/MIT-0.html
  Origin = -> Origin037
  expr: Label = <<RaspberryPi_>> + <<Pico>>.Label + <<_STEP>>
FEATURE [Part::Compound] Compound  label="J1_690T505-x62-01x"
  Links = -> [Body005,Group014]
  Placement = pos=(0,23.7,0) rot=(0,0,1;0rad)
  expr: Label = <<J1>>.Label + <<_>> + <<J1>>.Metadata_PartName
  expr: Placement = <<J1>>.Metadata_Placement
FEATURE [Part::Compound] Compound010  label="J2_BM03B-SRSS-TB"
  Links = -> [Group015,Thickness]
  Placement = pos=(0,-23,0) rot=(0,0,1;0rad)
  expr: Label = <<J2>>.Label + <<_>> + <<J2>>.Metadata_PartName
  expr: Placement = <<J2>>.Metadata_Placement
FEATURE [Part::Compound] Compound011  label="L1_2u2"
  Links = -> [Group011,Box010]
  Placement = pos=(6,14.6,0) rot=(0,0,1;0rad)
  expr: Label = <<L1>>.Label + <<_>> + <<L1>>.Metadata_PartName
  expr: Placement = <<L1>>.Metadata_Placement
FEATURE [Part::Compound] Compound012  label="Q1_DMG1012T"
  Links = -> [Group007,Box006]
  Placement = pos=(6.4,7.2,0) rot=(0,0,1;0rad)
  expr: Label = <<Q1>>.Label + <<_>> + <<Q1>>.Metadata_PartName
  expr: Placement = <<Q1>>.Metadata_Placement
FEATURE [Part::Compound] Compound013  label="SH1_CYW43439"
  Links = -> [Group013,Box014]
  Placement = pos=(0,-12.3,0) rot=(0,0,1;0rad)
  expr: Label = <<SH1>>.Label + <<_>> + <<SH1>>.Metadata_PartName
  expr: Placement = <<SH1>>.Metadata_Placement
FEATURE [Part::Compound] Compound014  label="SW1_TP-1221U-K9K5325"
  Links = -> [Group010,Body004]
  Placement = pos=(-3.5,13.5,0) rot=(0,0,1;0rad)
  expr: Label = <<SW1>>.Label + <<_>> + <<SW1>>.Metadata_PartName
  expr: Placement = <<SW1>>.Metadata_Placement
FEATURE [Part::Compound] Compound015  label="U1_RP2040"
  Links = -> [Group001,Box]
  Placement = pos=(0,-0.5,0) rot=(0,0,1;0rad)
  expr: Label = <<U1>>.Label + <<_>> + <<U1>>.Metadata_PartName
  expr: Placement = <<U1>>.Metadata_Placement
FEATURE [Part::Compound] Compound016  label="U2_RT6150B-33GQW"
  Links = -> [Group002,Box001]
  Placement = pos=(2.9,14.6,0) rot=(0,0,1;3.14159rad)
  expr: Label = <<U2>>.Label + <<_>> + <<U2>>.Metadata_PartName
  expr: Placement = <<U2>>.Metadata_Placement
FEATURE [Part::Compound] Compound017  label="U2_RT6154AGQW"
  Links = -> [Group025,Box017]
  Placement = pos=(2.3,14.6,0) rot=(0,0,1;1.5708rad)
  expr: Label = <<U2_>>.Label + <<>> + <<U2_>>.Metadata_PartName
  expr: Placement = <<U2_>>.Metadata_Placement
FEATURE [Part::Compound] Compound018  label="U3_W25Q16JVUXIQ"
  Links = -> [Box002,Group003]
  Placement = pos=(-3.8,6.4,0) rot=(0,0,1;1.5708rad)
  expr: Label = <<U3>>.Label + <<_>> + <<U3>>.Metadata_PartName
  expr: Placement = <<U3>>.Metadata_Placement
FEATURE [Part::Compound] Compound019  label="X1_X12M000000S096"
  Links = -> [Group004,Box003]
  Placement = pos=(-2.3,-9.05,0) rot=(0,0,1;0rad)
  expr: Label = <<X1>>.Label + <<_>> + <<X1>>.Metadata_PartName
  expr: Placement = <<X1>>.Metadata_Placement
FEATURE [App::DocumentObjectGroup] Group040  label="Pico_H"
FEATURE [App::Link] Link114  label="Pico_H_C1_47u"
  LinkPlacement = pos=(2.9,17.1,0) rot=(0,0,1;0rad)
  LinkedObject = -> Compound006
  Placement = pos=(2.9,17.1,0) rot=(0,0,1;0rad)
  expr: Label = <<Pico_H>>.Label + <<_>> + .LinkedObject.Label
  expr: Placement = <<vPico>>.C1Placement
FEATURE [App::Link] Link115  label="Pico_H_Board_Link"
  LinkedObject = -> Fusion001
  expr: Label = .LinkedObject.Label + <<_Link>>
FEATURE [App::Link] Link116  label="Pico_H_C2_47u"
  LinkPlacement = pos=(2.9,12.1,0) rot=(0,0,1;0rad)
  LinkedObject = -> Compound008
  Placement = pos=(2.9,12.1,0) rot=(0,0,1;0rad)
  expr: Label = <<Pico_H>>.Label + <<_>> + .LinkedObject.Label
  expr: Placement = <<vPico>>.C2Placement
FEATURE [App::Link] Link118  label="Pico_H_D1_MBR120VLSFT1G"
  LinkPlacement = pos=(6,18.9,0) rot=(0,0,1;0rad)
  LinkedObject = -> Compound007
  Placement = pos=(6,18.9,0) rot=(0,0,1;0rad)
  expr: Label = <<Pico_H>>.Label + <<_>> + .LinkedObject.Label
  expr: Placement = <<vPico>>.D1Placement
FEATURE [App::Link] Link119  label="Pico_H_D2_QSME-C194"
  LinkPlacement = pos=(-5.7,20.7,0) rot=(0,0,1;0rad)
  LinkedObject = -> Part013
  Placement = pos=(-5.7,20.7,0) rot=(0,0,1;0rad)
  expr: Label = <<Pico_H>>.Label + <<_>> + .LinkedObject.Label
  expr: Placement = <<vPico>>.D2Placement
FEATURE [App::Link] Link120  label="Pico_H_J1_690T505-x62-01x"
  LinkPlacement = pos=(0,23.7,0) rot=(0,0,1;0rad)
  LinkedObject = -> Compound
  Placement = pos=(0,23.7,0) rot=(0,0,1;0rad)
  expr: Label = <<Pico_H>>.Label + <<_>> + .LinkedObject.Label
  expr: Placement = <<vPico>>.J1Placement
FEATURE [App::Link] Link121  label="Pico_H_J2_BM03B-SRSS-TB"
  LinkPlacement = pos=(0,-23,0) rot=(0,0,1;0rad)
  LinkedObject = -> Compound010
  Placement = pos=(0,-23,0) rot=(0,0,1;0rad)
  expr: Label = <<Pico_H>>.Label + <<_>> + .LinkedObject.Label
  expr: Placement = <<vPicoH>>.J2Placement
FEATURE [App::Link] Link122  label="Pico_H_L1_2u2"
  LinkPlacement = pos=(6,14.6,0) rot=(0,0,1;0rad)
  LinkedObject = -> Compound011
  Placement = pos=(6,14.6,0) rot=(0,0,1;0rad)
  expr: Label = <<Pico_H>>.Label + <<_>> + .LinkedObject.Label
  expr: Placement = <<vPico>>.L1Placement
FEATURE [App::Link] Link123  label="Pico_H_Q1_DMG1012T"
  LinkPlacement = pos=(6.4,7.2,0) rot=(0,0,1;0rad)
  LinkedObject = -> Compound012
  Placement = pos=(6.4,7.2,0) rot=(0,0,1;0rad)
  expr: Label = <<Pico_H>>.Label + <<_>> + .LinkedObject.Label
  expr: Placement = <<vPico>>.Q1Placement
FEATURE [App::Link] Link125  label="Pico_H_SW1_TP-1221U-K9K5325"
  LinkPlacement = pos=(-3.5,13.5,0) rot=(0,0,1;0rad)
  LinkedObject = -> Compound014
  Placement = pos=(-3.5,13.5,0) rot=(0,0,1;0rad)
  expr: Label = <<Pico_H>>.Label + <<_>> + .LinkedObject.Label
  expr: Placement = <<vPico>>.SW1Placement
FEATURE [App::Link] Link126  label="Pico_H_U1_RP2040"
  LinkPlacement = pos=(0,-0.5,0) rot=(0,0,1;0rad)
  LinkedObject = -> Compound015
  Placement = pos=(0,-0.5,0) rot=(0,0,1;0rad)
  expr: Label = <<Pico_H>>.Label + <<_>> + .LinkedObject.Label
  expr: Placement = <<vPico>>.U1Placement
FEATURE [App::Link] Link127  label="Pico_H_U2_RT6150B-33GQW"
  LinkPlacement = pos=(2.9,14.6,0) rot=(0,0,1;3.14159rad)
  LinkedObject = -> Compound016
  Placement = pos=(2.9,14.6,0) rot=(0,0,1;3.14159rad)
  expr: Label = <<Pico_H>>.Label + <<_>> + .LinkedObject.Label
  expr: Placement = <<vPico>>.U2Placement
FEATURE [App::Link] Link129  label="Pico_H_U3_W25Q16JVUXIQ"
  LinkPlacement = pos=(-3.8,6.4,0) rot=(0,0,1;1.5708rad)
  LinkedObject = -> Compound018
  Placement = pos=(-3.8,6.4,0) rot=(0,0,1;1.5708rad)
  expr: Label = <<Pico_H>>.Label + <<_>> + .LinkedObject.Label
  expr: Placement = <<vPico>>.U3Placement
FEATURE [App::Link] Link130  label="Pico_H_X1_X12M000000S096"
  LinkPlacement = pos=(-2.3,-9.05,0) rot=(0,0,1;0rad)
  LinkedObject = -> Compound019
  Placement = pos=(-2.3,-9.05,0) rot=(0,0,1;0rad)
  expr: Label = <<Pico_H>>.Label + <<_>> + .LinkedObject.Label
  expr: Placement = <<vPico>>.X1Placement
FEATURE [App::Part] Part050  label="Pico_H_Components"
  Group = -> [Link114,Link116,Link118,Link119,Link120,Link121,Link122,Link123,Link125,Link126,Link127,Link129,Link130]
  Origin = -> Origin068
  Placement = pos=(0,0,1) rot=(0,0,1;0rad)
  expr: .Placement.Base.z = <<vPico>>.BoardThickness
  expr: Label = <<Pico_H>>.Label + <<_Components>>
FEATURE [App::Part] Part051  label="Pico_H_Module"
  Group = -> [Link115,Part050]
  Origin = -> Origin069
  Placement = pos=(0,0,2.54) rot=(0,0,1;0rad)
  expr: .Placement.Base.z = <<vHeader>>.InsulationThickness
  expr: Label = <<Pico_H>>.Label + <<_Module>>
FEATURE [App::DocumentObjectGroup] Group041  label="Pico_H_Socketed"
FEATURE [App::Link] Link132  label="Pico_H_Socketed_C1_47u"
  LinkPlacement = pos=(2.9,17.1,0) rot=(0,0,1;0rad)
  LinkedObject = -> Compound006
  Placement = pos=(2.9,17.1,0) rot=(0,0,1;0rad)
  expr: Label = <<Pico_H_Socketed>>.Label + <<_>> + .LinkedObject.Label
  expr: Placement = <<vPico>>.C1Placement
FEATURE [App::Link] Link133  label="Pico_H_Socketed_Board_Link"
  LinkedObject = -> Fusion001
  expr: Label = <<Pico_H_Socketed>>.Label + <<_Board>> + <<_Link>>
FEATURE [App::Link] Link134  label="Pico_H_Socketed_C2_47u"
  LinkPlacement = pos=(2.9,12.1,0) rot=(0,0,1;0rad)
  LinkedObject = -> Compound008
  Placement = pos=(2.9,12.1,0) rot=(0,0,1;0rad)
  expr: Label = <<Pico_H_Socketed>>.Label + <<_>> + .LinkedObject.Label
  expr: Placement = <<vPico>>.C2Placement
FEATURE [App::Link] Link136  label="Pico_H_Socketed_D1_MBR120VLSFT1G"
  LinkPlacement = pos=(6,18.9,0) rot=(0,0,1;0rad)
  LinkedObject = -> Compound007
  Placement = pos=(6,18.9,0) rot=(0,0,1;0rad)
  expr: Label = <<Pico_H_Socketed>>.Label + <<_>> + .LinkedObject.Label
  expr: Placement = <<vPico>>.D1Placement
FEATURE [App::Link] Link137  label="Pico_H_Socketed_D2_QSME-C194"
  LinkPlacement = pos=(-5.7,20.7,0) rot=(0,0,1;0rad)
  LinkedObject = -> Part013
  Placement = pos=(-5.7,20.7,0) rot=(0,0,1;0rad)
  expr: Label = <<Pico_H_Socketed>>.Label + <<_>> + .LinkedObject.Label
  expr: Placement = <<vPico>>.D2Placement
FEATURE [App::Link] Link138  label="Pico_H_Socketed_J1_690T505-x62-01x"
  LinkPlacement = pos=(0,23.7,0) rot=(0,0,1;0rad)
  LinkedObject = -> Compound
  Placement = pos=(0,23.7,0) rot=(0,0,1;0rad)
  expr: Label = <<Pico_H_Socketed>>.Label + <<_>> + .LinkedObject.Label
  expr: Placement = <<vPico>>.J1Placement
FEATURE [App::Link] Link139  label="Pico_H_Socketed_J2_BM03B-SRSS-TB"
  LinkPlacement = pos=(0,-23,0) rot=(0,0,1;0rad)
  LinkedObject = -> Compound010
  Placement = pos=(0,-23,0) rot=(0,0,1;0rad)
  expr: Label = <<Pico_H_Socketed>>.Label + <<_>> + .LinkedObject.Label
  expr: Placement = <<vPicoH>>.J2Placement
FEATURE [App::Link] Link140  label="Pico_H_Socketed_L1_2u2"
  LinkPlacement = pos=(6,14.6,0) rot=(0,0,1;0rad)
  LinkedObject = -> Compound011
  Placement = pos=(6,14.6,0) rot=(0,0,1;0rad)
  expr: Label = <<Pico_H_Socketed>>.Label + <<_>> + .LinkedObject.Label
  expr: Placement = <<vPico>>.L1Placement
FEATURE [App::Link] Link141  label="Pico_H_Socketed_Q1_DMG1012T"
  LinkPlacement = pos=(6.4,7.2,0) rot=(0,0,1;0rad)
  LinkedObject = -> Compound012
  Placement = pos=(6.4,7.2,0) rot=(0,0,1;0rad)
  expr: Label = <<Pico_H_Socketed>>.Label + <<_>> + .LinkedObject.Label
  expr: Placement = <<vPico>>.Q1Placement
FEATURE [App::Link] Link143  label="Pico_H_Socketed_SW1_TP-1221U-K9K5325"
  LinkPlacement = pos=(-3.5,13.5,0) rot=(0,0,1;0rad)
  LinkedObject = -> Compound014
  Placement = pos=(-3.5,13.5,0) rot=(0,0,1;0rad)
  expr: Label = <<Pico_H_Socketed>>.Label + <<_>> + .LinkedObject.Label
  expr: Placement = <<vPico>>.SW1Placement
FEATURE [App::Link] Link144  label="Pico_H_Socketed_U1_RP2040"
  LinkPlacement = pos=(0,-0.5,0) rot=(0,0,1;0rad)
  LinkedObject = -> Compound015
  Placement = pos=(0,-0.5,0) rot=(0,0,1;0rad)
  expr: Label = <<Pico_H_Socketed>>.Label + <<_>> + .LinkedObject.Label
  expr: Placement = <<vPico>>.U1Placement
FEATURE [App::Link] Link145  label="Pico_H_Socketed_U2_RT6150B-33GQW"
  LinkPlacement = pos=(2.9,14.6,0) rot=(0,0,1;3.14159rad)
  LinkedObject = -> Compound016
  Placement = pos=(2.9,14.6,0) rot=(0,0,1;3.14159rad)
  expr: Label = <<Pico_H_Socketed>>.Label + <<_>> + .LinkedObject.Label
  expr: Placement = <<vPico>>.U2Placement
FEATURE [App::Link] Link147  label="Pico_H_Socketed_U3_W25Q16JVUXIQ"
  LinkPlacement = pos=(-3.8,6.4,0) rot=(0,0,1;1.5708rad)
  LinkedObject = -> Compound018
  Placement = pos=(-3.8,6.4,0) rot=(0,0,1;1.5708rad)
  expr: Label = <<Pico_H_Socketed>>.Label + <<_>> + .LinkedObject.Label
  expr: Placement = <<vPico>>.U3Placement
FEATURE [App::Link] Link148  label="Pico_H_Socketed_X1_X12M000000S096"
  LinkPlacement = pos=(-2.3,-9.05,0) rot=(0,0,1;0rad)
  LinkedObject = -> Compound019
  Placement = pos=(-2.3,-9.05,0) rot=(0,0,1;0rad)
  expr: Label = <<Pico_H_Socketed>>.Label + <<_>> + .LinkedObject.Label
  expr: Placement = <<vPico>>.X1Placement
FEATURE [App::Part] Part053  label="Pico_H_Socketed_Components"
  Group = -> [Link132,Link134,Link136,Link137,Link138,Link139,Link140,Link141,Link143,Link144,Link145,Link147,Link148]
  Origin = -> Origin071
  Placement = pos=(0,0,1) rot=(0,0,1;0rad)
  expr: .Placement.Base.z = <<vPico>>.BoardThickness
  expr: Label = <<Pico_H_Socketed>>.Label + <<_Components>>
FEATURE [App::Part] Part054  label="Pico_H_Socketed_Module"
  Group = -> [Link133,Part053]
  Origin = -> Origin072
  Placement = pos=(0,0,11) rot=(0,0,1;0rad)
  expr: .Placement.Base.z = <<vHeader>>.InsulationThickness + <<vSocket>>.BodyHeight
  expr: Label = <<Pico_H_Socketed>>.Label + <<_Module>>
FEATURE [App::DocumentObjectGroup] Group042  label="Pico_W"
FEATURE [App::Link] Link150  label="Pico_W_C1_47u"
  LinkPlacement = pos=(1.9,18.07,0) rot=(0,0,1;0rad)
  LinkedObject = -> Compound006
  Placement = pos=(1.9,18.07,0) rot=(0,0,1;0rad)
  expr: Label = <<Pico_W>>.Label + <<_>> + .LinkedObject.Label
  expr: Placement = <<vPicoW>>.C1Placement
FEATURE [App::Link] Link151  label="Pico_W_Board_Link"
  LinkedObject = -> Fusion002
  expr: Label = <<Pico_W>>.Label + <<_Board_Link>>
FEATURE [App::Link] Link152  label="Pico_W_C2_47u"
  LinkPlacement = pos=(2.01,10.79,0) rot=(0,0,1;0rad)
  LinkedObject = -> Compound008
  Placement = pos=(2.01,10.79,0) rot=(0,0,1;0rad)
  expr: Label = <<Pico_W>>.Label + <<_>> + .LinkedObject.Label
  expr: Placement = <<vPicoW>>.C2Placement
FEATURE [App::Link] Link153  label="Pico_W_C21_47u"
  LinkPlacement = pos=(2.01,9.07,0) rot=(0,0,1;0rad)
  LinkedObject = -> Compound009
  Placement = pos=(2.01,9.07,0) rot=(0,0,1;0rad)
  expr: Label = <<Pico_W>>.Label + <<_>> + .LinkedObject.Label
  expr: Placement = <<vPicoW>>.C21Placement
FEATURE [App::Link] Link154  label="Pico_W_D1_MBR120VLSFT1G"
  LinkPlacement = pos=(6,18.9,0) rot=(0,0,1;0rad)
  LinkedObject = -> Compound007
  Placement = pos=(6,18.9,0) rot=(0,0,1;0rad)
  expr: Label = <<Pico_W>>.Label + <<_>> + .LinkedObject.Label
  expr: Placement = <<vPico>>.D1Placement
FEATURE [App::Link] Link155  label="Pico_W_D2_QSME-C194"
  LinkPlacement = pos=(-5.7,20.7,0) rot=(0,0,1;0rad)
  LinkedObject = -> Part013
  Placement = pos=(-5.7,20.7,0) rot=(0,0,1;0rad)
  expr: Label = <<Pico_W>>.Label + <<_>> + .LinkedObject.Label
  expr: Placement = <<vPico>>.D2Placement
FEATURE [App::Link] Link156  label="Pico_W_J1_690T505-x62-01x"
  LinkPlacement = pos=(0,23.7,0) rot=(0,0,1;0rad)
  LinkedObject = -> Compound
  Placement = pos=(0,23.7,0) rot=(0,0,1;0rad)
  expr: Label = <<Pico_W>>.Label + <<_>> + .LinkedObject.Label
  expr: Placement = <<vPico>>.J1Placement
FEATURE [App::Link] Link158  label="Pico_W_L1_2u2"
  LinkPlacement = pos=(6,14.6,0) rot=(0,0,1;0rad)
  LinkedObject = -> Compound011
  Placement = pos=(6,14.6,0) rot=(0,0,1;0rad)
  expr: Label = <<Pico_W>>.Label + <<_>> + .LinkedObject.Label
  expr: Placement = <<vPico>>.L1Placement
FEATURE [App::Link] Link159  label="Pico_W_Q1_DMG1012T"
  LinkPlacement = pos=(6.49,7.76,0) rot=(0,0,1;0rad)
  LinkedObject = -> Compound012
  Placement = pos=(6.49,7.76,0) rot=(0,0,1;0rad)
  expr: Label = <<Pico_W>>.Label + <<_>> + .LinkedObject.Label
  expr: Placement = <<vPicoW>>.Q1Placement
FEATURE [App::Link] Link160  label="Pico_W_SH1_CYW43439"
  LinkPlacement = pos=(0,-12.3,0) rot=(0,0,1;0rad)
  LinkedObject = -> Compound013
  Placement = pos=(0,-12.3,0) rot=(0,0,1;0rad)
  expr: Label = <<Pico_W>>.Label + <<_>> + .LinkedObject.Label
  expr: Placement = <<vPicoW>>.SH1Placement
FEATURE [App::Link] Link161  label="Pico_W_SW1_TP-1221U-K9K5325"
  LinkPlacement = pos=(-3.5,13.5,0) rot=(0,0,1;0rad)
  LinkedObject = -> Compound014
  Placement = pos=(-3.5,13.5,0) rot=(0,0,1;0rad)
  expr: Label = <<Pico_W>>.Label + <<_>> + .LinkedObject.Label
  expr: Placement = <<vPico>>.SW1Placement
FEATURE [App::Link] Link162  label="Pico_W_U1_RP2040"
  LinkPlacement = pos=(0,1.55,0) rot=(0,0,1;0rad)
  LinkedObject = -> Compound015
  Placement = pos=(0,1.55,0) rot=(0,0,1;0rad)
  expr: Label = <<Pico_W>>.Label + <<_>> + .LinkedObject.Label
  expr: Placement = <<vPicoW>>.U1Placement
FEATURE [App::Link] Link164  label="Pico_W_U2_RT6154AGQW"
  LinkPlacement = pos=(2.3,14.6,0) rot=(0,0,1;1.5708rad)
  LinkedObject = -> Compound017
  Placement = pos=(2.3,14.6,0) rot=(0,0,1;1.5708rad)
  expr: Label = <<Pico_W>>.Label + <<_>> + .LinkedObject.Label
  expr: Placement = <<vPicoW>>.U2Placement
FEATURE [App::Link] Link165  label="Pico_W_U3_W25Q16JVUXIQ"
  LinkPlacement = pos=(-3.32,8.69,0) rot=(0,0,1;0rad)
  LinkedObject = -> Compound018
  Placement = pos=(-3.32,8.69,0) rot=(0,0,1;0rad)
  expr: Label = <<Pico_W>>.Label + <<_>> + .LinkedObject.Label
  expr: Placement = <<vPicoW>>.U3Placement
FEATURE [App::Link] Link166  label="Pico_W_X1_X12M000000S096"
  LinkPlacement = pos=(-4.7,-4.91,0) rot=(0,0,1;0rad)
  LinkedObject = -> Compound019
  Placement = pos=(-4.7,-4.91,0) rot=(0,0,1;0rad)
  expr: Label = <<Pico_W>>.Label + <<_>> + .LinkedObject.Label
  expr: Placement = <<vPicoW>>.X1Placement
FEATURE [App::Part] Part056  label="Pico_W_Components"
  Group = -> [Link150,Link152,Link153,Link154,Link155,Link156,Link158,Link159,Link160,Link161,Link162,Link164,Link165,Link166]
  Origin = -> Origin074
  Placement = pos=(0,0,1) rot=(0,0,1;0rad)
  expr: .Placement.Base.z = <<vPico>>.BoardThickness
  expr: Label = <<Pico_W>>.Label + <<_Components>>
FEATURE [App::Part] Part055  label="RaspberryPi_Pico_W_STEP"
  Group = -> [Group042,Link151,Part056]
  License = MIT-0 (Public-domain-equivalent)
  LicenseURL = https://spdx.org/licenses/MIT-0.html
  Origin = -> Origin073
  expr: Label = <<RaspberryPi_>> + <<Pico_W>>.Label + <<_STEP>>
FEATURE [App::DocumentObjectGroup] Group043  label="Pico_WH"
FEATURE [App::Link] Link167  label="Pico_WH_C1_47u"
  LinkPlacement = pos=(1.9,18.07,0) rot=(0,0,1;0rad)
  LinkedObject = -> Compound006
  Placement = pos=(1.9,18.07,0) rot=(0,0,1;0rad)
  expr: Label = <<Pico_WH>>.Label + <<_>> + .LinkedObject.Label
  expr: Placement = <<vPicoW>>.C1Placement
FEATURE [App::Link] Link168  label="Pico_WH_Board_Link"
  LinkedObject = -> Fusion003
  expr: Label = .LinkedObject.Label + <<_Link>>
FEATURE [App::Link] Link169  label="Pico_WH_C2_47u"
  LinkPlacement = pos=(2.01,10.79,0) rot=(0,0,1;0rad)
  LinkedObject = -> Compound008
  Placement = pos=(2.01,10.79,0) rot=(0,0,1;0rad)
  expr: Label = <<Pico_WH>>.Label + <<_>> + .LinkedObject.Label
  expr: Placement = <<vPicoW>>.C2Placement
FEATURE [App::Link] Link170  label="Pico_WH_C21_47u"
  LinkPlacement = pos=(2.01,9.07,0) rot=(0,0,1;0rad)
  LinkedObject = -> Compound009
  Placement = pos=(2.01,9.07,0) rot=(0,0,1;0rad)
  expr: Label = <<Pico_WH>>.Label + <<_>> + .LinkedObject.Label
  expr: Placement = <<vPicoW>>.C21Placement
FEATURE [App::Link] Link171  label="Pico_WH_D1_MBR120VLSFT1G"
  LinkPlacement = pos=(6,18.9,0) rot=(0,0,1;0rad)
  LinkedObject = -> Compound007
  Placement = pos=(6,18.9,0) rot=(0,0,1;0rad)
  expr: Label = <<Pico_WH>>.Label + <<_>> + .LinkedObject.Label
  expr: Placement = <<vPico>>.D1Placement
FEATURE [App::Link] Link172  label="Pico_WH_D2_QSME-C194"
  LinkPlacement = pos=(-5.7,20.7,0) rot=(0,0,1;0rad)
  LinkedObject = -> Part013
  Placement = pos=(-5.7,20.7,0) rot=(0,0,1;0rad)
  expr: Label = <<Pico_WH>>.Label + <<_>> + .LinkedObject.Label
  expr: Placement = <<vPico>>.D2Placement
FEATURE [App::Link] Link173  label="Pico_WH_J1_690T505-x62-01x"
  LinkPlacement = pos=(0,23.7,0) rot=(0,0,1;0rad)
  LinkedObject = -> Compound
  Placement = pos=(0,23.7,0) rot=(0,0,1;0rad)
  expr: Label = <<Pico_WH>>.Label + <<_>> + .LinkedObject.Label
  expr: Placement = <<vPico>>.J1Placement
FEATURE [App::Link] Link174  label="Pico_WH_J2_BM03B-SRSS-TB"
  LinkPlacement = pos=(3,-6.45,2.125) rot=(-1,0,0;1.5708rad)
  LinkedObject = -> Compound010
  Placement = pos=(3,-6.45,2.125) rot=(-1,0,0;1.5708rad)
  expr: Label = <<Pico_WH>>.Label + <<_>> + .LinkedObject.Label
  expr: Placement = <<vPicoWH>>.J2Placement
FEATURE [App::Link] Link175  label="Pico_WH_L1_2u2"
  LinkPlacement = pos=(6,14.6,0) rot=(0,0,1;0rad)
  LinkedObject = -> Compound011
  Placement = pos=(6,14.6,0) rot=(0,0,1;0rad)
  expr: Label = <<Pico_WH>>.Label + <<_>> + .LinkedObject.Label
  expr: Placement = <<vPico>>.L1Placement
FEATURE [App::Link] Link176  label="Pico_WH_Q1_DMG1012T"
  LinkPlacement = pos=(6.49,7.76,0) rot=(0,0,1;0rad)
  LinkedObject = -> Compound012
  Placement = pos=(6.49,7.76,0) rot=(0,0,1;0rad)
  expr: Label = <<Pico_WH>>.Label + <<_>> + .LinkedObject.Label
  expr: Placement = <<vPicoW>>.Q1Placement
FEATURE [App::Link] Link177  label="Pico_WH_SH1_CYW43439"
  LinkPlacement = pos=(0,-12.3,0) rot=(0,0,1;0rad)
  LinkedObject = -> Compound013
  Placement = pos=(0,-12.3,0) rot=(0,0,1;0rad)
  expr: Label = <<Pico_WH>>.Label + <<_>> + .LinkedObject.Label
  expr: Placement = <<vPicoW>>.SH1Placement
FEATURE [App::Link] Link178  label="Pico_WH_SW1_TP-1221U-K9K5325"
  LinkPlacement = pos=(-3.5,13.5,0) rot=(0,0,1;0rad)
  LinkedObject = -> Compound014
  Placement = pos=(-3.5,13.5,0) rot=(0,0,1;0rad)
  expr: Label = <<Pico_WH>>.Label + <<_>> + .LinkedObject.Label
  expr: Placement = <<vPico>>.SW1Placement
FEATURE [App::Link] Link179  label="Pico_WH_U1_RP2040"
  LinkPlacement = pos=(0,1.55,0) rot=(0,0,1;0rad)
  LinkedObject = -> Compound015
  Placement = pos=(0,1.55,0) rot=(0,0,1;0rad)
  expr: Label = <<Pico_WH>>.Label + <<_>> + .LinkedObject.Label
  expr: Placement = <<vPicoW>>.U1Placement
FEATURE [App::Link] Link181  label="Pico_WH_U2_RT6154AGQW"
  LinkPlacement = pos=(2.3,14.6,0) rot=(0,0,1;1.5708rad)
  LinkedObject = -> Compound017
  Placement = pos=(2.3,14.6,0) rot=(0,0,1;1.5708rad)
  expr: Label = <<Pico_WH>>.Label + <<_>> + .LinkedObject.Label
  expr: Placement = <<vPicoW>>.U2Placement
FEATURE [App::Link] Link182  label="Pico_WH_U3_W25Q16JVUXIQ"
  LinkPlacement = pos=(-3.32,8.69,0) rot=(0,0,1;0rad)
  LinkedObject = -> Compound018
  Placement = pos=(-3.32,8.69,0) rot=(0,0,1;0rad)
  expr: Label = <<Pico_WH>>.Label + <<_>> + .LinkedObject.Label
  expr: Placement = <<vPicoW>>.U3Placement
FEATURE [App::Link] Link183  label="Pico_WH_X1_X12M000000S096"
  LinkPlacement = pos=(-4.7,-4.91,0) rot=(0,0,1;0rad)
  LinkedObject = -> Compound019
  Placement = pos=(-4.7,-4.91,0) rot=(0,0,1;0rad)
  expr: Label = <<Pico_WH>>.Label + <<_>> + .LinkedObject.Label
  expr: Placement = <<vPicoW>>.X1Placement
FEATURE [App::Part] Part058  label="Pico_WH_Components"
  Group = -> [Link167,Link169,Link170,Link171,Link172,Link173,Link174,Link175,Link176,Link177,Link178,Link179,Link181,Link182,Link183]
  Origin = -> Origin076
  Placement = pos=(0,0,1) rot=(0,0,1;0rad)
  expr: .Placement.Base.z = <<vPico>>.BoardThickness
  expr: Label = <<Pico_WH>>.Label + <<_Components>>
FEATURE [App::Part] Part059  label="Pico_WH_Module"
  Group = -> [Link168,Part058]
  Origin = -> Origin077
  Placement = pos=(0,0,2.54) rot=(0,0,1;0rad)
  expr: .Placement.Base.z = <<vHeader>>.InsulationThickness
  expr: Label = <<Pico_WH>>.Label + <<_Module>>
FEATURE [App::DocumentObjectGroup] Group044  label="Pico_WH_Socketed"
FEATURE [App::Link] Link185  label="Pico_WH_Socketed_C1_47u"
  LinkPlacement = pos=(1.9,18.07,0) rot=(0,0,1;0rad)
  LinkedObject = -> Compound006
  Placement = pos=(1.9,18.07,0) rot=(0,0,1;0rad)
  expr: Label = <<Pico_WH_Socketed>>.Label + <<_>> + .LinkedObject.Label
  expr: Placement = <<vPicoW>>.C1Placement
FEATURE [App::Link] Link186  label="Pico_WH_Socketed_Board_Link"
  LinkedObject = -> Fusion003
  expr: Label = <<Pico_WH_Socketed>>.Label + <<_Board>> + <<_Link>>
FEATURE [App::Link] Link187  label="Pico_WH_Socketed_C2_47u"
  LinkPlacement = pos=(2.01,10.79,0) rot=(0,0,1;0rad)
  LinkedObject = -> Compound008
  Placement = pos=(2.01,10.79,0) rot=(0,0,1;0rad)
  expr: Label = <<Pico_WH_Socketed>>.Label + <<_>> + .LinkedObject.Label
  expr: Placement = <<vPicoW>>.C2Placement
FEATURE [App::Link] Link188  label="Pico_WH_Socketed_C21_47u"
  LinkPlacement = pos=(2.01,9.07,0) rot=(0,0,1;0rad)
  LinkedObject = -> Compound009
  Placement = pos=(2.01,9.07,0) rot=(0,0,1;0rad)
  expr: Label = <<Pico_WH_Socketed>>.Label + <<_>> + .LinkedObject.Label
  expr: Placement = <<vPicoW>>.C21Placement
FEATURE [App::Link] Link189  label="Pico_WH_Socketed_D1_MBR120VLSFT1G"
  LinkPlacement = pos=(6,18.9,0) rot=(0,0,1;0rad)
  LinkedObject = -> Compound007
  Placement = pos=(6,18.9,0) rot=(0,0,1;0rad)
  expr: Label = <<Pico_WH_Socketed>>.Label + <<_>> + .LinkedObject.Label
  expr: Placement = <<vPico>>.D1Placement
FEATURE [App::Link] Link190  label="Pico_WH_Socketed_D2_QSME-C194"
  LinkPlacement = pos=(-5.7,20.7,0) rot=(0,0,1;0rad)
  LinkedObject = -> Part013
  Placement = pos=(-5.7,20.7,0) rot=(0,0,1;0rad)
  expr: Label = <<Pico_WH_Socketed>>.Label + <<_>> + .LinkedObject.Label
  expr: Placement = <<vPico>>.D2Placement
FEATURE [App::Link] Link191  label="Pico_WH_Socketed_J1_690T505-x62-01x"
  LinkPlacement = pos=(0,23.7,0) rot=(0,0,1;0rad)
  LinkedObject = -> Compound
  Placement = pos=(0,23.7,0) rot=(0,0,1;0rad)
  expr: Label = <<Pico_WH_Socketed>>.Label + <<_>> + .LinkedObject.Label
  expr: Placement = <<vPico>>.J1Placement
FEATURE [App::Link] Link192  label="Pico_WH_Socketed_J2_BM03B-SRSS-TB"
  LinkPlacement = pos=(3,-6.45,2.125) rot=(-1,0,0;1.5708rad)
  LinkedObject = -> Compound010
  Placement = pos=(3,-6.45,2.125) rot=(-1,0,0;1.5708rad)
  expr: Label = <<Pico_WH_Socketed>>.Label + <<_>> + .LinkedObject.Label
  expr: Placement = <<vPicoWH>>.J2Placement
FEATURE [App::Link] Link193  label="Pico_WH_Socketed_L1_2u2"
  LinkPlacement = pos=(6,14.6,0) rot=(0,0,1;0rad)
  LinkedObject = -> Compound011
  Placement = pos=(6,14.6,0) rot=(0,0,1;0rad)
  expr: Label = <<Pico_WH_Socketed>>.Label + <<_>> + .LinkedObject.Label
  expr: Placement = <<vPico>>.L1Placement
FEATURE [App::Link] Link194  label="Pico_WH_Socketed_Q1_DMG1012T"
  LinkPlacement = pos=(6.49,7.76,0) rot=(0,0,1;0rad)
  LinkedObject = -> Compound012
  Placement = pos=(6.49,7.76,0) rot=(0,0,1;0rad)
  expr: Label = <<Pico_WH_Socketed>>.Label + <<_>> + .LinkedObject.Label
  expr: Placement = <<vPicoW>>.Q1Placement
FEATURE [App::Link] Link195  label="Pico_WH_Socketed_SH1_CYW43439"
  LinkPlacement = pos=(0,-12.3,0) rot=(0,0,1;0rad)
  LinkedObject = -> Compound013
  Placement = pos=(0,-12.3,0) rot=(0,0,1;0rad)
  expr: Label = <<Pico_WH_Socketed>>.Label + <<_>> + .LinkedObject.Label
  expr: Placement = <<vPicoW>>.SH1Placement
FEATURE [App::Link] Link196  label="Pico_WH_Socketed_SW1_TP-1221U-K9K5325"
  LinkPlacement = pos=(-3.5,13.5,0) rot=(0,0,1;0rad)
  LinkedObject = -> Compound014
  Placement = pos=(-3.5,13.5,0) rot=(0,0,1;0rad)
  expr: Label = <<Pico_WH_Socketed>>.Label + <<_>> + .LinkedObject.Label
  expr: Placement = <<vPico>>.SW1Placement
FEATURE [App::Link] Link197  label="Pico_WH_Socketed_U1_RP2040"
  LinkPlacement = pos=(0,1.55,0) rot=(0,0,1;0rad)
  LinkedObject = -> Compound015
  Placement = pos=(0,1.55,0) rot=(0,0,1;0rad)
  expr: Label = <<Pico_WH_Socketed>>.Label + <<_>> + .LinkedObject.Label
  expr: Placement = <<vPicoW>>.U1Placement
FEATURE [App::Link] Link199  label="Pico_WH_Socketed_U2_RT6154AGQW"
  LinkPlacement = pos=(2.3,14.6,0) rot=(0,0,1;1.5708rad)
  LinkedObject = -> Compound017
  Placement = pos=(2.3,14.6,0) rot=(0,0,1;1.5708rad)
  expr: Label = <<Pico_WH_Socketed>>.Label + <<_>> + .LinkedObject.Label
  expr: Placement = <<vPicoW>>.U2Placement
FEATURE [App::Link] Link200  label="Pico_WH_Socketed_U3_W25Q16JVUXIQ"
  LinkPlacement = pos=(-3.32,8.69,0) rot=(0,0,1;0rad)
  LinkedObject = -> Compound018
  Placement = pos=(-3.32,8.69,0) rot=(0,0,1;0rad)
  expr: Label = <<Pico_WH_Socketed>>.Label + <<_>> + .LinkedObject.Label
  expr: Placement = <<vPicoW>>.U3Placement
FEATURE [App::Link] Link201  label="Pico_WH_Socketed_X1_X12M000000S096"
  LinkPlacement = pos=(-4.7,-4.91,0) rot=(0,0,1;0rad)
  LinkedObject = -> Compound019
  Placement = pos=(-4.7,-4.91,0) rot=(0,0,1;0rad)
  expr: Label = <<Pico_WH_Socketed>>.Label + <<_>> + .LinkedObject.Label
  expr: Placement = <<vPicoW>>.X1Placement
FEATURE [App::Part] Part061  label="Pico_WH_Socketed_Components"
  Group = -> [Link185,Link187,Link188,Link189,Link190,Link191,Link192,Link193,Link194,Link195,Link196,Link197,Link199,Link200,Link201]
  Origin = -> Origin079
  Placement = pos=(0,0,1) rot=(0,0,1;0rad)
  expr: .Placement.Base.z = <<vPico>>.BoardThickness
  expr: Label = <<Pico_WH_Socketed>>.Label + <<_Components>>
FEATURE [App::Part] Part062  label="Pico_WH_Socketed_Module"
  Group = -> [Link186,Part061]
  Origin = -> Origin080
  Placement = pos=(0,0,11) rot=(0,0,1;0rad)
  expr: .Placement.Base.z = <<vHeader>>.InsulationThickness + <<vSocket>>.BodyHeight
  expr: Label = <<Pico_WH_Socketed>>.Label + <<_Module>>
FEATURE [PartDesign::Point] DatumPoint  label="Substrate"
  AttacherType = Attacher::AttachEnginePoint
FEATURE [Sketcher::SketchObject] Sketch084  label="Sketch_Boards_Substrate_BoardOutline"
  FullyConstrained = true
  MapMode = 5
  Support = -> [XY_Plane081]
  expr: Constraints[23] = <<vPico>>.BoardWidth
  expr: Constraints[24] = <<vPico>>.BoardLength
  expr: Constraints[25] = <<vPico>>.BoardCornerRadius
  expr: Label = <<Sketch_>> + <<Boards>>.Label + <<_>> + <<Substrate>>.Label + <<_BoardOutline>>
  sketch-geometry (13):
    g0: LineSegment StartX=-10.5 StartY=-25 StartZ=0 EndX=-10.5 EndY=25 EndZ=0
    g1: LineSegment StartX=-10 StartY=25.5 StartZ=0 EndX=10 EndY=25.5 EndZ=0
    g2: LineSegment StartX=10.5 StartY=25 StartZ=0 EndX=10.5 EndY=-25 EndZ=0
    g3: LineSegment StartX=10 StartY=-25.5 StartZ=0 EndX=-10 EndY=-25.5 EndZ=0
    g4: GeomPoint X=0 Y=0 Z=0
    g5: ArcOfCircle CenterX=-10 CenterY=25 CenterZ=0 NormalX=0 NormalY=0 NormalZ=1 AngleXU=0 Radius=0.5 StartAngle=1.5708 EndAngle=3.14159
    g6: GeomPoint X=-10.5 Y=25.5 Z=0
    g7: ArcOfCircle CenterX=10 CenterY=25 CenterZ=0 NormalX=0 NormalY=0 NormalZ=1 AngleXU=0 Radius=0.5 StartAngle=-3.6e-15 EndAngle=1.5708
    g8: GeomPoint X=10.5 Y=25.5 Z=0
    g9: ArcOfCircle CenterX=10 CenterY=-25 CenterZ=0 NormalX=0 NormalY=0 NormalZ=1 AngleXU=0 Radius=0.5 StartAngle=4.71239 EndAngle=6.28319
    g10: GeomPoint X=10.5 Y=-25.5 Z=0
    g11: ArcOfCircle CenterX=-10 CenterY=-25 CenterZ=0 NormalX=0 NormalY=0 NormalZ=1 AngleXU=0 Radius=0.5 StartAngle=3.14159 EndAngle=4.71239
    g12: GeomPoint X=-10.5 Y=-25.5 Z=0
  constraints (26):
    c: Coincident(g4,g-1)
    c: Symmetric(g6,g8,g-2)
    c: Symmetric(g12,g6,g-1)
    c: Symmetric(g6,g10,g4)
    c: PointOnObject(g6,g0)
    c: PointOnObject(g6,g1)
    c: Tangent(g0,g5) = 1.5708
    c: Tangent(g1,g5) = 1.5708
    c: PointOnObject(g8,g1)
    c: PointOnObject(g8,g2)
    c: Tangent(g1,g7) = 1.5708
    c: Tangent(g2,g7) = 1.5708
    c: PointOnObject(g10,g2)
    c: PointOnObject(g10,g3)
    c: Tangent(g2,g9) = 1.5708
    c: Tangent(g3,g9) = 1.5708
    c: PointOnObject(g12,g0)
    c: PointOnObject(g12,g3)
    c: Tangent(g0,g11) = 1.5708
    c: Tangent(g3,g11) = 1.5708
    c: Equal(g11,g5)
    c: Equal(g5,g7)
    c: Equal(g5,g9)
    c: Distance(g0,g2) = 21
    c: Distance(g1,g3) = 51
    c: Radius(g5) = 0.5
FEATURE [PartDesign::Pad] Pad084  label="Pad_Boards_Substrate_BoardOutline"
  Direction = (0,0,1)
  Length = 1
  Length2 = 10
  Profile = -> Sketch084
  ReferenceAxis = -> Sketch084 [N_Axis]
  Type = 0
  expr: Label = <<Pad_>> + <<Boards>>.Label + <<_>> + <<Substrate>>.Label + <<_BoardOutline>>
  expr: Length = <<vPico>>.BoardThickness
FEATURE [Sketcher::SketchObject] Sketch085  label="Sketch_Boards_Substrate_MountingHole"
  AttachmentOffset = pos=(-5.7,23.5,0) rot=(0,0,1;0rad)
  FullyConstrained = true
  MapMode = 5
  Placement = pos=(-5.7,23.5,0) rot=(0,0,1;0rad)
  Support = -> [XY_Plane081]
  expr: .AttachmentOffset.Base.x = -(<<vPico>>.BoardWidth / 2 - <<vPico>>.BoardMountingHoleInset.x)
  expr: .AttachmentOffset.Base.y = <<vPico>>.BoardLength / 2 - <<vPico>>.BoardMountingHoleInset.y
  expr: Constraints[0] = <<vPico>>.BoardMountingHoleDiameter
  expr: Label = <<Sketch_>> + <<Boards>>.Label + <<_>> + <<Substrate>>.Label + <<_MountingHole>>
  sketch-geometry (1):
    g0: Circle CenterX=0 CenterY=0 CenterZ=0 NormalX=0 NormalY=0 NormalZ=1 AngleXU=0 Radius=1.05
  constraints (2):
    c: Diameter(g0) = 2.1
    c: Coincident(g0,g-1)
FEATURE [PartDesign::Pocket] Pocket029  label="Pocket_Boards_Substrate_MountingHole"
  BaseFeature = -> Pad084
  Direction = (0,0,-1)
  Length = 5
  Length2 = 5
  Midplane = true
  Profile = -> Sketch085
  ReferenceAxis = -> Sketch085 [N_Axis]
  Type = 1
  expr: Label = <<Pocket_>> + <<Boards>>.Label + <<_>> + <<Substrate>>.Label + <<_MountingHole>>
FEATURE [PartDesign::Mirrored] Mirrored041  label="Mirror_Boards_Substrate_MountingHolesVertical"
  MirrorPlane = -> XZ_Plane081
  expr: Label = <<Mirror_>> + <<Boards>>.Label + <<_>> + <<Substrate>>.Label + <<_MountingHolesVertical>>
FEATURE [PartDesign::Mirrored] Mirrored042  label="Mirror_Boards_Substrate_MountingHolesHorizontal"
  MirrorPlane = -> YZ_Plane081
  expr: Label = <<Mirror_>> + <<Boards>>.Label + <<_>> + <<Substrate>>.Label + <<_MountingHolesHorizontal>>
FEATURE [PartDesign::MultiTransform] MultiTransform023  label="MultiMirror_Boards_Substrate_MountingHoles"
  BaseFeature = -> Pocket029
  Originals = -> [Pocket029]
  Transformations = -> [Mirrored041,Mirrored042]
  expr: Label = <<MultiMirror_>> + <<Boards>>.Label + <<_>> + <<Substrate>>.Label + <<_MountingHoles>>
FEATURE [Sketcher::SketchObject] Sketch086  label="Sketch_Boards_Substrate_PinHole"
  AttachmentOffset = pos=(-8.89,24.13,0) rot=(0,0,1;0rad)
  FullyConstrained = true
  MapMode = 5
  Placement = pos=(-8.89,24.13,0) rot=(0,0,1;0rad)
  Support = -> [XY_Plane081]
  expr: .AttachmentOffset.Base.x = -(<<vPico>>.BoardWidth / 2 - <<vPico>>.PinInset)
  expr: .AttachmentOffset.Base.y = <<vPico>>.PinPitch * (<<vPico>>.PinDIPCount / 4 - 0.5)
  expr: Constraints[0] = <<vPico>>.PinHoleDiameter
  expr: Label = <<Sketch_>> + <<Boards>>.Label + <<_>> + <<Substrate>>.Label + <<_PinHole>>
  sketch-geometry (1):
    g0: ArcOfCircle CenterX=0 CenterY=0 CenterZ=0 NormalX=0 NormalY=0 NormalZ=1 AngleXU=0 Radius=0.5 StartAngle=3.14159 EndAngle=9.42478
  constraints (4):
    c: Diameter(g0) = 1
    c: Coincident(g0,g-1)
    c: PointOnObject(g0,g-1)
    c: PointOnObject(g0,g-1)
FEATURE [PartDesign::Pocket] Pocket030  label="Pocket_Boards_Substrate_PinHole"
  BaseFeature = -> MultiTransform023
  Direction = (0,0,-1)
  Length = 5
  Length2 = 5
  Midplane = true
  Profile = -> Sketch086
  ReferenceAxis = -> Sketch086 [N_Axis]
  Type = 1
  expr: Label = <<Pocket_>> + <<Boards>>.Label + <<_>> + <<Substrate>>.Label + <<_PinHole>>
FEATURE [PartDesign::LinearPattern] LinearPattern063  label="LinearPattern_Boards_Substrate_PinHoles"
  Direction = -> Y_Axis081
  Length = 48.26
  Occurrences = 20
  Reversed = true
  expr: Label = <<LinearPattern_>> + <<Boards>>.Label + <<_>> + <<Substrate>>.Label + <<_PinHoles>>
  expr: Length = (<<vPico>>.PinDIPCount / 2 - 1) * <<vPico>>.PinPitch
  expr: Occurrences = <<vPico>>.PinDIPCount / 2
FEATURE [PartDesign::Mirrored] Mirrored043  label="Mirror_Boards_Substrate_PinHoles"
  MirrorPlane = -> YZ_Plane081
  expr: Label = <<Mirror_>> + <<Boards>>.Label + <<_>> + <<Substrate>>.Label + <<_PinHoles>>
FEATURE [PartDesign::MultiTransform] MultiTransform024  label="MultiTransform_Boards_Substrate_PinHoles"
  BaseFeature = -> Pocket030
  Originals = -> [Pocket030]
  Transformations = -> [LinearPattern063,Mirrored043]
  expr: Label = <<MultiTransform_>> + <<Boards>>.Label + <<_>> + <<Substrate>>.Label + <<_PinHoles>>
FEATURE [Part::Part2DObjectPython] Clone2D015  label="Clone_Sketch_Boards_Substrate_PinHole_CastellatedPinHole"  # Draft 2D object (typed FeaturePython)
  AttachmentOffset = pos=(-1.6,0,0) rot=(0,0,1;0rad)
  Fuse = false
  MapMode = 2
  Objects = -> [Sketch086]
  Placement = pos=(-10.49,24.13,0) rot=(0,0,1;0rad)
  Scale = (1,1,1)
  Support = -> [Sketch086]
  expr: .AttachmentOffset.Base.x = -<<vPico>>.PinToCastellationCenter
  expr: Label = <<Clone_>> + Objects[0].Label + <<_CastellatedPinHole>>
FEATURE [PartDesign::Pocket] Pocket031  label="Pocket_Boards_Substrate_CastellatedPinHole"
  BaseFeature = -> MultiTransform024
  Direction = (0,0,-1)
  Length = 5
  Length2 = 5
  Midplane = true
  Profile = -> Clone2D015
  ReferenceAxis = -> Clone2D015 [N_Axis]
  Type = 1
  expr: Label = <<Pocket_>> + <<Boards>>.Label + <<_>> + <<Substrate>>.Label + <<_CastellatedPinHole>>
FEATURE [PartDesign::Point] DatumPoint005  label="Soldermask"
  AttacherType = Attacher::AttachEnginePoint
FEATURE [Part::Part2DObjectPython] Clone2D016  label="EXTREF_Clone_Sketch_Boards_Substrate_BoardOutline_Soldermask"  # Draft 2D object (typed FeaturePython)
  Fuse = false
  MapMode = 5
  Objects = -> [Sketch084]
  Scale = (1,1,1)
  Support = -> [XY_Plane082]
  expr: Label = <<EXTREF_>> + <<Clone_>> + Objects[0].Label + <<_>> + <<Soldermask>>.Label
FEATURE [PartDesign::Pad] Pad085  label="EXTREF_Pad_Boards_Soldermask_BoardSurface"
  Direction = (0,0,1)
  Length = 1
  Length2 = 10
  Profile = -> Clone2D016
  ReferenceAxis = -> Clone2D016 [N_Axis]
  Reversed = true
  Type = 0
  expr: Label = <<EXTREF_>> + <<Pad_>> + <<Boards>>.Label + <<_>> + <<Soldermask>>.Label + <<_BoardSurface>>
  expr: Length = <<vPico>>.BoardThickness
FEATURE [PartDesign::LinearPattern] LinearPattern064  label="LinearPattern_Boards_Substrate_CastellatedPinHoles"
  Direction = -> Y_Axis081
  Length = 48.26
  Occurrences = 20
  Reversed = true
  expr: Label = <<LinearPattern_>> + <<Boards>>.Label + <<_>> + <<Substrate>>.Label + <<_CastellatedPinHoles>>
  expr: Length = (<<vPico>>.PinDIPCount / 2 - 1) * <<vPico>>.PinPitch
  expr: Occurrences = <<vPico>>.PinDIPCount / 2
FEATURE [PartDesign::Mirrored] Mirrored044  label="Mirror_Boards_Substrate_CastellatedPinHoles"
  MirrorPlane = -> YZ_Plane081
  expr: Label = <<Mirror_>> + <<Boards>>.Label + <<_>> + <<Substrate>>.Label + <<_CastellatedPinHoles>>
FEATURE [PartDesign::MultiTransform] MultiTransform025  label="MultiTransform_Boards_Substrate_CastellatedPinHoles"
  BaseFeature = -> Pocket031
  Originals = -> [Pocket031]
  Transformations = -> [LinearPattern064,Mirrored044]
  expr: Label = <<MultiTransform_>> + <<Boards>>.Label + <<_>> + <<Substrate>>.Label + <<_CastellatedPinHoles>>
FEATURE [Sketcher::SketchObject] Sketch087  label="Sketch_Boards_Soldermask_UpperMountingHoleMargin"
  AttachmentOffset = pos=(-5.7,23.5,0) rot=(0,0,1;0rad)
  FullyConstrained = true
  MapMode = 5
  Placement = pos=(-5.7,23.5,0) rot=(0,0,1;0rad)
  Support = -> [XY_Plane082]
  expr: .AttachmentOffset.Base.x = -(<<vPico>>.BoardWidth / 2 - <<vPico>>.BoardMountingHoleInset.x)
  expr: .AttachmentOffset.Base.y = <<vPico>>.BoardLength / 2 - <<vPico>>.BoardMountingHoleInset.y
  expr: Constraints[1] = <<vPico>>.BoardMountingHoleMarginDiameter
  expr: Label = <<Sketch_>> + <<Boards>>.Label + <<_>> + <<Soldermask>>.Label + <<_UpperMountingHoleMargin>>
  sketch-geometry (1):
    g0: Circle CenterX=0 CenterY=0 CenterZ=0 NormalX=0 NormalY=0 NormalZ=1 AngleXU=0 Radius=1.9
  constraints (2):
    c: Coincident(g0,g-1)
    c: Diameter(g0) = 3.8
FEATURE [PartDesign::Pocket] Pocket032  label="Pocket_Boards_Soldermask_UpperMountingHoleMargin"
  BaseFeature = -> Pad085
  Direction = (0,0,-1)
  Length = 5
  Length2 = 5
  Midplane = true
  Profile = -> Sketch087
  ReferenceAxis = -> Sketch087 [N_Axis]
  Type = 1
  expr: Label = <<Pocket_>> + <<Boards>>.Label + <<_>> + <<Soldermask>>.Label + <<_UpperMountingHoleMargin>>
FEATURE [PartDesign::Mirrored] Mirrored045  label="Mirror_Boards_Soldermask_UpperMountingHoleMargins"
  BaseFeature = -> Pocket032
  MirrorPlane = -> YZ_Plane082
  Originals = -> [Pocket032]
  expr: Label = <<Mirror_>> + <<Boards>>.Label + <<_>> + <<Soldermask>>.Label + <<_UpperMountingHoleMargins>>
FEATURE [Part::Part2DObjectPython] Clone2D017  label="Clone_Sketch_Boards_Substrate_PinHole_DebugPinHole"  # Draft 2D object (typed FeaturePython)
  AttachmentOffset = pos=(-2.54,-23.9,0) rot=(0,0,1;1.5708rad)
  Fuse = false
  MapMode = 5
  Objects = -> [Sketch086]
  Placement = pos=(-2.54,-23.9,0) rot=(0,0,1;1.5708rad)
  Scale = (1,1,1)
  Support = -> [XY_Plane081]
  expr: .AttachmentOffset.Base.x = <<vPico>>.DebugCenter.x - <<vPico>>.PinPitch
  expr: .AttachmentOffset.Base.y = <<vPico>>.DebugCenter.y
  expr: Label = <<Clone_>> + Objects[0].Label + <<_DebugPinHole>>
FEATURE [PartDesign::LinearPattern] LinearPattern065  label="LinearPattern_Boards_Substrate_DebugPinHoles"
  Direction = -> X_Axis081
  Length = 5.08
  Occurrences = 3
  expr: Label = <<LinearPattern_>> + <<Boards>>.Label + <<_>> + <<Substrate>>.Label + <<_DebugPinHoles>>
  expr: Length = <<vPico>>.PinPitch * (Occurrences - 1)
FEATURE [PartDesign::LinearPattern] LinearPattern066  label="LinearPattern_Boards_Substrate_CastellatedDebugPinHoles"
  Direction = -> Y_Axis081
  Length = 1.6
  Occurrences = 2
  Reversed = true
  expr: Label = <<LinearPattern_>> + <<Boards>>.Label + <<_>> + <<Substrate>>.Label + <<_CastellatedDebugPinHoles>>
  expr: Length = <<vPico>>.PinToCastellationCenter
FEATURE [Sketcher::SketchObject] Sketch088  label="Sketch_Boards_Soldermask_PicoWLowerMountingHoleMargin"
  AttachmentOffset = pos=(-5.7,-23.5,0) rot=(0,0,1;0rad)
  FullyConstrained = true
  MapMode = 5
  Placement = pos=(-5.7,-23.5,0) rot=(0,0,1;0rad)
  Support = -> [XY_Plane082]
  expr: .AttachmentOffset.Base.x = -(<<vPico>>.BoardWidth / 2 - <<vPico>>.BoardMountingHoleInset.x)
  expr: .AttachmentOffset.Base.y = -(<<vPico>>.BoardLength / 2 - <<vPico>>.BoardMountingHoleInset.y)
  expr: Constraints[1] = <<vPicoW>>.LowerMountingHoleMarginDiameter
  expr: Label = <<Sketch_>> + <<Boards>>.Label + <<_>> + <<Soldermask>>.Label + <<_PicoWLowerMountingHoleMargin>>
  sketch-geometry (1):
    g0: Circle CenterX=0 CenterY=0 CenterZ=0 NormalX=0 NormalY=0 NormalZ=1 AngleXU=0 Radius=1.5
  constraints (2):
    c: Coincident(g0,g-1)
    c: Diameter(g0) = 3
FEATURE [PartDesign::Pocket] Pocket034  label="Pocket_Boards_Soldermask_PicoWLowerMountingHoleMargin"
  BaseFeature = -> Mirrored045
  Direction = (0,0,-1)
  Length = 5
  Length2 = 5
  Midplane = true
  Profile = -> Sketch088
  ReferenceAxis = -> Sketch088 [N_Axis]
  Type = 1
  expr: Label = <<Pocket_>> + <<Boards>>.Label + <<_>> + <<Soldermask>>.Label + <<_PicoWLowerMountingHoleMargin>>
FEATURE [PartDesign::Mirrored] Mirrored046  label="Mirror_Boards_Soldermask_PicoWLowerMountingHoleMargins"
  BaseFeature = -> Pocket034
  MirrorPlane = -> YZ_Plane082
  Originals = -> [Pocket034]
  expr: Label = <<Mirror_>> + <<Boards>>.Label + <<_>> + <<Soldermask>>.Label + <<_PicoWLowerMountingHoleMargins>>
FEATURE [Part::Part2DObjectPython] Clone2D018  label="Clone_Sketch_Boards_Soldermask_UpperMountingHoleMargin_PicoLowerMountingHoleMargin"  # Draft 2D object (typed FeaturePython)
  Fuse = false
  MapMode = 2
  Objects = -> [Sketch087]
  Placement = pos=(-5.7,-23.5,0) rot=(0,0,1;0rad)
  Scale = (1,1,1)
  Support = -> [Sketch088]
  expr: Label = <<Clone_>> + Objects[0].Label + <<_PicoLowerMountingHoleMargin>>
FEATURE [PartDesign::Pocket] Pocket035  label="Pocket_Boards_Soldermask_PicoLowerMountingHoleMargin"
  BaseFeature = -> Mirrored046
  Direction = (0,0,-1)
  Length = 5
  Length2 = 5
  Midplane = true
  Profile = -> Clone2D018
  ReferenceAxis = -> Clone2D018 [N_Axis]
  Type = 1
  expr: Label = <<Pocket_>> + <<Boards>>.Label + <<_>> + <<Soldermask>>.Label + <<_PicoLowerMountingHoleMargin>>
FEATURE [PartDesign::Mirrored] Mirrored047  label="Mirror_Boards_Soldermask_PicoLowerMountingHoleMargins"
  BaseFeature = -> Pocket035
  MirrorPlane = -> YZ_Plane082
  Originals = -> [Pocket035]
  expr: Label = <<Mirror_>> + <<Boards>>.Label + <<_>> + <<Soldermask>>.Label + <<_PicoLowerMountingHoleMargins>>
FEATURE [PartDesign::Body] Body016  label="Boards_Soldermask"
  Group = -> [DatumPoint005,Clone2D016,Pad085,Sketch087,Pocket032,Mirrored045,Sketch088,Pocket034,Mirrored046,Clone2D018,Pocket035,Mirrored047]
  Origin = -> Origin082
  Tip = -> Mirrored047
  expr: Label = <<Boards>>.Label + <<_>> + <<Soldermask>>.Label
FEATURE [App::Link] Link205  label="Tool_Boards_Soldermask_Bottom_PicoW"
  LinkedObject = -> Mirrored046
  expr: Label = <<Tool_>> + <<Boards>>.Label + <<_>> + <<Soldermask>>.Label + <<_Bottom_PicoW>>
FEATURE [App::Link] Link206  label="Tool_Boards_Soldermask_Bottom_Pico"
  LinkedObject = -> Mirrored047
  expr: Label = <<Tool_>> + <<Boards>>.Label + <<_>> + <<Soldermask>>.Label + <<_Bottom_Pico>>
FEATURE [App::Link] Link207  label="Tool_Boards_Soldermask_Top_PicoW"
  LinkPlacement = pos=(0,0,2) rot=(0,0,1;0rad)
  LinkedObject = -> Mirrored046
  Placement = pos=(0,0,2) rot=(0,0,1;0rad)
  expr: .LinkPlacement.Base.z = <<vPico>>.BoardThickness * 1 mm + <<EXTREF_Pad_Boards_Soldermask_BoardSurface>>.Length
  expr: Label = <<Tool_>> + <<Boards>>.Label + <<_>> + <<Soldermask>>.Label + <<_Top_PicoW>>
FEATURE [App::Link] Link208  label="Tool_Boards_Soldermask_Top_Pico"
  LinkPlacement = pos=(0,0,2) rot=(0,0,1;0rad)
  LinkedObject = -> Mirrored047
  Placement = pos=(0,0,2) rot=(0,0,1;0rad)
  expr: .LinkPlacement.Base.z = <<vPico>>.BoardThickness * 1 mm + <<EXTREF_Pad_Boards_Soldermask_BoardSurface>>.Length
  expr: Label = <<Tool_>> + <<Boards>>.Label + <<_>> + <<Soldermask>>.Label + <<_Top_Pico>>
FEATURE [Part::Compound] Compound020  label="Tool_Boards_Soldermask_Pico"
  Links = -> [Link208,Link206]
  expr: Label = <<Tool_>> + <<Boards>>.Label + <<_>> + <<Soldermask>>.Label + <<_Pico>>
FEATURE [Part::Compound] Compound021  label="Tool_Boards_Soldermask_PicoW"
  Links = -> [Link207,Link205]
  expr: Label = <<Tool_>> + <<Boards>>.Label + <<_>> + <<Soldermask>>.Label + <<_PicoW>>
FEATURE [App::Link] Link209  label="Tool_Boards_Substrate_PicoH"
  LinkedObject = -> MultiTransform024
  expr: Label = <<Tool_>> + <<Boards>>.Label + <<_>> + <<Substrate>>.Label + <<_PicoH>>
FEATURE [App::Link] Link211  label="Tool_Boards_Substrate_Pico"
  LinkedObject = -> MultiTransform026
  expr: Label = <<Tool_>> + <<Boards>>.Label + <<_>> + <<Substrate>>.Label + <<_Pico>>
FEATURE [App::Link] Link212  label="Tool_Board_Pico_Substrate"
  LinkedObject = -> Link211
  expr: Label = <<Tool_Board_>> + <<Pico_>> + <<Substrate>>.Label
FEATURE [App::Link] Link213  label="Tool_Board_Pico_Soldermask"
  LinkTransform = true
  LinkedObject = -> Compound020
  expr: Label = <<Tool_Board_>> + <<Pico_>> + <<Soldermask>>.Label
FEATURE [App::Link] Link214  label="Tool_Board_PicoH_Substrate"
  LinkedObject = -> Link209
  expr: Label = <<Tool_Board_>> + <<PicoH_>> + <<Substrate>>.Label
FEATURE [App::Link] Link215  label="Tool_Board_PicoH_Soldermask"
  LinkTransform = true
  LinkedObject = -> Compound020
  expr: Label = <<Tool_Board_>> + <<PicoH_>> + <<Soldermask>>.Label
FEATURE [App::Link] Link217  label="Tool_Board_PicoW_Soldermask"
  LinkTransform = true
  LinkedObject = -> Compound021
  expr: Label = <<Tool_Board_>> + <<PicoW_>> + <<Soldermask>>.Label
FEATURE [App::Link] Link218  label="Tool_Board_PicoWH_Substrate"
  LinkedObject = -> Link209
  expr: Label = <<Tool_Board_>> + <<PicoWH_>> + <<Substrate>>.Label
FEATURE [App::Link] Link219  label="Tool_Board_PicoWH_Soldermask"
  LinkTransform = true
  LinkedObject = -> Compound021
  expr: Label = <<Tool_Board_>> + <<PicoWH_>> + <<Soldermask>>.Label
FEATURE [Part::Cut] Cut001  label="Tool_Board_Pico_NoPads"
  Base = -> Link212
  Tool = -> Link213
FEATURE [Part::Cut] Cut002  label="Tool_Board_PicoH_NoPads"
  Base = -> Link214
  Tool = -> Link215
FEATURE [Part::Cut] Cut004  label="Tool_Board_PicoWH_NoPads"
  Base = -> Link218
  Tool = -> Link219
FEATURE [PartDesign::Point] DatumPoint008  label="GoldPads"
  AttacherType = Attacher::AttachEnginePoint
FEATURE [Sketcher::SketchObject] Sketch096  label="Sketch_Boards_GoldPads_PinPad_Round_Castellated"
  AttachmentOffset = pos=(-8.89,24.13,0) rot=(0,0,1;0rad)
  FullyConstrained = true
  MapMode = 5
  Placement = pos=(-8.89,24.13,0) rot=(0,0,1;0rad)
  Support = -> [XY_Plane085]
  expr: .AttachmentOffset.Base.x = -(<<vPico>>.BoardWidth / 2 - <<vPico>>.PinInset)
  expr: .AttachmentOffset.Base.y = (<<vPico>>.PinDIPCount / 4 - 0.5) * <<vPico>>.PinPitch
  expr: Constraints[18] = <<vPico>>.PinToCastellationCenter
  expr: Constraints[1] = <<vPico>>.PinPadWidth
  expr: Constraints[20] = <<vPico>>.PinInset
  expr: Constraints[5] = <<vPico>>.PinHoleDiameter
  expr: Label = <<Sketch_>> + <<Boards>>.Label + <<_>> + <<GoldPads>>.Label + <<_PinPad_Round_Castellated>>
  sketch-geometry (7):
    g0: ArcOfCircle CenterX=0 CenterY=0 CenterZ=0 NormalX=0 NormalY=0 NormalZ=1 AngleXU=0 Radius=0.8 StartAngle=4.71239 EndAngle=7.85398
    g1: ArcOfCircle CenterX=0 CenterY=0 CenterZ=0 NormalX=0 NormalY=0 NormalZ=1 AngleXU=0 Radius=0.5 StartAngle=3.14159 EndAngle=9.42478
    g2: LineSegment StartX=2e-16 StartY=0.8 StartZ=0 EndX=-1.61 EndY=0.8 EndZ=0
    g3: LineSegment StartX=-1e-16 StartY=-0.8 StartZ=0 EndX=-1.61 EndY=-0.8 EndZ=0
    g4: LineSegment StartX=-1.61 StartY=0.8 StartZ=0 EndX=-1.61 EndY=0.4999 EndZ=0
    g5: LineSegment StartX=-1.61 StartY=-0.8 StartZ=0 EndX=-1.61 EndY=-0.4999 EndZ=0
    g6: ArcOfCircle CenterX=-1.6 CenterY=0 CenterZ=0 NormalX=0 NormalY=0 NormalZ=1 AngleXU=0 Radius=0.5 StartAngle=4.69239 EndAngle=7.87398
  constraints (21):
    c: Coincident(g0,g-1)
    c: Diameter(g0) = 1.6
    c: Coincident(g1,g0)
    c: PointOnObject(g1,g-1)
    c: PointOnObject(g1,g-1)
    c: Diameter(g1) = 1
    c: Coincident(g4,g2)
    c: Coincident(g5,g3)
    c: Coincident(g6,g4)
    c: Coincident(g6,g5)
    c: Tangent(g2,g0) = -1.5708
    c: Tangent(g3,g0) = 1.5708
    c: Horizontal(g3)
    c: Parallel(g2,g3)
    c: Perpendicular(g3,g5)
    c: PointOnObject(g2,g5)
    c: PointOnObject(g4,g5)
    c: PointOnObject(g6,g-1)
    c: Distance(g6,g0) = 1.6
    c: Equal(g6,g1)
    c: Distance(g0,g5) = 1.61
FEATURE [PartDesign::Mirrored] Mirrored048  label="Mirror_Boards_GoldPads_Core_Vertical"
  MirrorPlane = -> XZ_Plane085
  expr: Label = <<Mirror_>> + <<Boards>>.Label + <<_>> + <<GoldPads>>.Label + <<_Core_Vertical>>
FEATURE [PartDesign::Mirrored] Mirrored049  label="Mirror_Boards_GoldPads_Core_Horizontal"
  MirrorPlane = -> YZ_Plane085
  expr: Label = <<Mirror_>> + <<Boards>>.Label + <<_>> + <<GoldPads>>.Label + <<_Core_Horizontal>>
FEATURE [PartDesign::LinearPattern] LinearPattern067  label="LinearPattern_Boards_GoldPads_PinPads_Round_Castellated_1"
  Direction = -> Y_Axis085
  Length = 2.54
  Occurrences = 2
  Reversed = true
  expr: Label = <<LinearPattern_>> + <<Boards>>.Label + <<_>> + <<GoldPads>>.Label + <<_PinPads_Round_Castellated_1>>
  expr: Length = <<vPico>>.PinPitch * (Occurrences - 1)
FEATURE [PartDesign::Mirrored] Mirrored050  label="Mirror_Boards_GoldPads_PinPads_Round_Castellated"
  MirrorPlane = -> YZ_Plane085
  expr: Label = <<Mirror_>> + <<Boards>>.Label + <<_>> + <<GoldPads>>.Label + <<_PinPads_Round_Castellated>>
FEATURE [PartDesign::Point] DatumPoint009  label="SolderedPads"
  AttacherType = Attacher::AttachEnginePoint
FEATURE [PartDesign::LinearPattern] LinearPattern068  label="LinearPattern_Boards_SolderedPads_PinPads_Round_1"
  Direction = -> Y_Axis086
  Length = 2.54
  Occurrences = 2
  Reversed = true
  expr: Label = <<LinearPattern_>> + <<Boards>>.Label + <<_>> + <<SolderedPads>>.Label + <<_PinPads_Round_1>>
  expr: Length = <<vPico>>.PinPitch * (Occurrences - 1)
  expr: Occurrences = 2
FEATURE [PartDesign::Mirrored] Mirrored053  label="Mirror_Boards_SolderedPads_PinPads_Round"
  MirrorPlane = -> YZ_Plane086
  expr: Label = <<Mirror_>> + <<Boards>>.Label + <<_>> + <<SolderedPads>>.Label + <<_PinPads_Round>>
FEATURE [Sketcher::SketchObject] Sketch099  label="Sketch_Boards_SolderedPads_Core"
  AttachmentOffset = pos=(0,0,0.5) rot=(0,0,1;0rad)
  FullyConstrained = true
  MapMode = 5
  Placement = pos=(0,0,0.5) rot=(0,0,1;0rad)
  Support = -> [XY_Plane086]
  expr: .AttachmentOffset.Base.z = <<vPico>>.BoardThickness / 2
  expr: Constraints[15] = abs(<<vPico>>.DebugCenter.y) - (<<vPico>>.PinHoleDiameter + <<vPico>>.PinPadWidth) / 4
  expr: Constraints[1] = <<vPico>>.BoardWidth / 2 - (<<vPico>>.PinInset + (<<vPico>>.PinHoleDiameter + <<vPico>>.PinPadWidth) / 4)
  expr: Constraints[20] = (<<vPico>>.PinHoleDiameter + <<vPico>>.PinPadWidth) / 4
  expr: Constraints[29] = <<vPico>>.PinPitch - (<<vPico>>.PinHoleDiameter + <<vPico>>.PinPadWidth) / 2
  expr: Constraints[3] = (<<vPico>>.PinDIPCount / 4 - 0.5) * <<vPico>>.PinPitch
  expr: Constraints[4] = <<vPico>>.BoardWidth / 2 - <<vPico>>.BoardMountingHoleInset.x
  expr: Constraints[5] = <<vPico>>.BoardLength / 2 - <<vPico>>.BoardMountingHoleInset.y
  expr: Constraints[6] = (<<vPico>>.BoardMountingHoleDiameter + <<vPicoW>>.LowerMountingHoleMarginDiameter) / 2
  expr: Label = <<Sketch_>> + <<Boards>>.Label + <<_>> + <<SolderedPads>>.Label + <<_Core>>
  sketch-geometry (10):
    g0: LineSegment StartX=-8.24 StartY=0 StartZ=0 EndX=-8.24 EndY=24.13 EndZ=0
    g1: ArcOfCircle CenterX=-5.7 CenterY=23.5 CenterZ=0 NormalX=0 NormalY=0 NormalZ=1 AngleXU=0 Radius=1.275 StartAngle=2.62477 EndAngle=6.08583
    g2: LineSegment StartX=-8.24 StartY=24.13 StartZ=0 EndX=-6.80848 EndY=24.13 EndZ=0
    g3: LineSegment StartX=0 StartY=23.25 StartZ=0 EndX=0 EndY=0 EndZ=0
    g4: LineSegment StartX=0 StartY=0 StartZ=0 EndX=-8.24 EndY=0 EndZ=0
    g5: LineSegment StartX=-4.44975 StartY=23.25 StartZ=0 EndX=-1.89 EndY=23.25 EndZ=0
    g6: LineSegment StartX=-0.65 StartY=23.25 StartZ=0 EndX=0 EndY=23.25 EndZ=0
    g7: LineSegment StartX=-1.89 StartY=23.25 StartZ=0 EndX=-1.89 EndY=24.13 EndZ=0
    g8: LineSegment StartX=-1.89 StartY=24.13 StartZ=0 EndX=-0.65 EndY=24.13 EndZ=0
    g9: LineSegment StartX=-0.65 StartY=24.13 StartZ=0 EndX=-0.65 EndY=23.25 EndZ=0
  constraints (30):
    c: Vertical(g0)
    c: Distance(g0,g-2) = 8.24
    c: PointOnObject(g0,g-1)
    c: Distance(g0) = 24.13
    c: Distance(g1,g-2) = 5.7
    c: Distance(g1,g-1) = 23.5
    c: Diameter(g1) = 2.55
    c: Coincident(g2,g0)
    c: Coincident(g2,g1)
    c: Coincident(g3,g-1)
    c: Coincident(g4,g3)
    c: Coincident(g4,g0)
    c: Perpendicular(g2,g0)
    c: Coincident(g5,g1)
    c: Perpendicular(g0,g5)
    c: Distance(g3,g-1) = 23.25
    c: PointOnObject(g3,g-2)
    c: Coincident(g6,g3)
    c: PointOnObject(g3,g5)
    c: Perpendicular(g3,g6)
    c: Distance(g6) = 0.65
    c: Coincident(g7,g5)
    c: Coincident(g8,g7)
    c: Coincident(g9,g8)
    c: Coincident(g9,g6)
    c: PointOnObject(g7,g2)
    c: PointOnObject(g8,g2)
    c: Perpendicular(g7,g8)
    c: Perpendicular(g9,g8)
    c: Distance(g8) = 1.24
FEATURE [PartDesign::Mirrored] Mirrored051  label="Mirror_Boards_SolderedPads_Core_Vertical"
  MirrorPlane = -> Sketch099 [H_Axis]
  expr: Label = <<Mirror_>> + <<Boards>>.Label + <<_>> + <<SolderedPads>>.Label + <<_Core_Vertical>>
FEATURE [PartDesign::Mirrored] Mirrored052  label="Mirror_Boards_SolderedPads_Core_Horizontal"
  MirrorPlane = -> Sketch099 [V_Axis]
  expr: Label = <<Mirror_>> + <<Boards>>.Label + <<_>> + <<SolderedPads>>.Label + <<_Core_Horizontal>>
FEATURE [PartDesign::Pad] Pad094  label="Pad_Boards_SolderedPads_Core"
  Direction = (0,0,1)
  Length = 0.5
  Length2 = 10
  Midplane = true
  Profile = -> Sketch099
  ReferenceAxis = -> Sketch099 [N_Axis]
  Type = 0
  expr: Label = <<Pad_>> + <<Boards>>.Label + <<_>> + <<SolderedPads>>.Label + <<_Core>>
  expr: Length = <<vPico>>.BoardThickness / 2
FEATURE [PartDesign::MultiTransform] MultiTransform029  label="MultiTransform_Boards_SolderedPads_Core"
  BaseFeature = -> Pad094
  Originals = -> [Pad094]
  Refine = true
  Transformations = -> [Mirrored051,Mirrored052]
  expr: Label = <<MultiTransform_>> + <<Boards>>.Label + <<_>> + <<SolderedPads>>.Label + <<_Core>>
FEATURE [Sketcher::SketchObject] Sketch100  label="Sketch_Boards_SolderedPads_PinPad_Round"
  AttachmentOffset = pos=(-8.89,24.13,0) rot=(0,0,1;0rad)
  FullyConstrained = true
  MapMode = 5
  Placement = pos=(-8.89,24.13,0) rot=(0,0,1;0rad)
  Support = -> [XY_Plane086]
  expr: .AttachmentOffset.Base.x = -(<<vPico>>.BoardWidth / 2 - <<vPico>>.PinInset)
  expr: .AttachmentOffset.Base.y = (<<vPico>>.PinDIPCount / 4 - 0.5) * <<vPico>>.PinPitch
  expr: Constraints[1] = <<vPico>>.PinPadWidth
  expr: Constraints[5] = <<vPico>>.PinHoleDiameter
  expr: Label = <<Sketch_>> + <<Boards>>.Label + <<_>> + <<SolderedPads>>.Label + <<_PinPad_Round>>
  sketch-geometry (2):
    g0: ArcOfCircle CenterX=0 CenterY=0 CenterZ=0 NormalX=0 NormalY=0 NormalZ=1 AngleXU=0 Radius=0.8 StartAngle=3.14159 EndAngle=9.42478
    g1: ArcOfCircle CenterX=0 CenterY=0 CenterZ=0 NormalX=0 NormalY=0 NormalZ=1 AngleXU=0 Radius=0.5 StartAngle=3.14159 EndAngle=9.42478
  constraints (8):
    c: Coincident(g0,g-1)
    c: Diameter(g0) = 1.6
    c: Coincident(g1,g0)
    c: PointOnObject(g1,g-1)
    c: PointOnObject(g1,g-1)
    c: Diameter(g1) = 1
    c: PointOnObject(g0,g-1)
    c: PointOnObject(g0,g-1)
FEATURE [Sketcher::SketchObject] Sketch101  label="Sketch_Boards_SolderedPads_PinPad_Square"
  AttachmentOffset = pos=(0,-5.08,0) rot=(0,0,1;0rad)
  FullyConstrained = true
  MapMode = 2
  Placement = pos=(-8.89,19.05,0) rot=(0,0,1;0rad)
  Support = -> [Sketch100]
  expr: .AttachmentOffset.Base.y = -<<vPico>>.PinPitch * 2
  expr: Constraints[17] = <<vPico>>.PinPadWidth
  expr: Constraints[18] = <<vPico>>.PinSquarePadRadius
  expr: Constraints[22] = <<vPico>>.PinHoleDiameter
  expr: Label = <<Sketch_>> + <<Boards>>.Label + <<_>> + <<SolderedPads>>.Label + <<_PinPad_Square>>
  sketch-geometry (9):
    g0: LineSegment StartX=-0.8 StartY=-0.6 StartZ=0 EndX=-0.8 EndY=0.6 EndZ=0
    g1: LineSegment StartX=-0.6 StartY=0.8 StartZ=0 EndX=0.6 EndY=0.8 EndZ=0
    g2: LineSegment StartX=0.8 StartY=0.6 StartZ=0 EndX=0.8 EndY=-0.6 EndZ=0
    g3: LineSegment StartX=0.6 StartY=-0.8 StartZ=0 EndX=-0.6 EndY=-0.8 EndZ=0
    g4: ArcOfCircle CenterX=-0.6 CenterY=0.6 CenterZ=0 NormalX=0 NormalY=0 NormalZ=1 AngleXU=0 Radius=0.2 StartAngle=1.5708 EndAngle=3.14159
    g5: ArcOfCircle CenterX=0.6 CenterY=0.6 CenterZ=0 NormalX=0 NormalY=0 NormalZ=1 AngleXU=0 Radius=0.2 StartAngle=-2.7e-15 EndAngle=1.5708
    g6: ArcOfCircle CenterX=0.6 CenterY=-0.6 CenterZ=0 NormalX=0 NormalY=0 NormalZ=1 AngleXU=0 Radius=0.2 StartAngle=4.71239 EndAngle=6.28319
    g7: ArcOfCircle CenterX=-0.6 CenterY=-0.6 CenterZ=0 NormalX=0 NormalY=0 NormalZ=1 AngleXU=0 Radius=0.2 StartAngle=3.14159 EndAngle=4.71239
    g8: ArcOfCircle CenterX=0 CenterY=0 CenterZ=0 NormalX=0 NormalY=0 NormalZ=1 AngleXU=0 Radius=0.5 StartAngle=3.14159 EndAngle=9.42478
  constraints (23):
    c: Vertical(g0)
    c: Tangent(g0,g4) = 1.5708
    c: Tangent(g1,g4) = 1.5708
    c: Tangent(g1,g5) = 1.5708
    c: Tangent(g2,g5) = 1.5708
    c: Tangent(g2,g6) = 1.5708
    c: Tangent(g3,g6) = 1.5708
    c: Tangent(g0,g7) = 1.5708
    c: Tangent(g3,g7) = 1.5708
    c: Equal(g0,g3)
    c: Parallel(g0,g2)
    c: Parallel(g3,g1)
    c: Perpendicular(g3,g0)
    c: Equal(g7,g4)
    c: Equal(g7,g5)
    c: Equal(g7,g6)
    c: Symmetric(g7,g5,g-1)
    c: Distance(g3,g1) = 1.6
    c: Radius(g7) = 0.2
    c: Coincident(g8,g-1)
    c: PointOnObject(g8,g-1)
    c: PointOnObject(g8,g-1)
    c: Diameter(g8) = 1
FEATURE [PartDesign::LinearPattern] LinearPattern069  label="LinearPattern_Boards_SolderedPads_PinPads_Square"
  Direction = -> Y_Axis086
  Length = 38.1
  Occurrences = 4
  Reversed = true
  expr: Label = <<LinearPattern_>> + <<Boards>>.Label + <<_>> + <<SolderedPads>>.Label + <<_PinPads_Square>>
  expr: Length = <<vPico>>.PinPitch * 5 * (Occurrences - 1)
FEATURE [PartDesign::LinearPattern] LinearPattern070  label="LinearPattern_Boards_SolderedPads_PinPads_Round_2"
  Direction = -> Y_Axis086
  Length = 7.62
  Occurrences = 2
  Reversed = true
  expr: Label = <<LinearPattern_>> + <<Boards>>.Label + <<_>> + <<SolderedPads>>.Label + <<_PinPads_Round_2>>
  expr: Length = <<vPico>>.PinPitch * 3 * (.Occurrences - 1)
FEATURE [PartDesign::LinearPattern] LinearPattern071  label="LinearPattern_Boards_SolderedPads_PinPads_Round_3"
  Direction = -> Y_Axis086
  Length = 38.1
  Occurrences = 4
  Reversed = true
  expr: Label = <<LinearPattern_>> + <<Boards>>.Label + <<_>> + <<SolderedPads>>.Label + <<_PinPads_Round_3>>
  expr: Length = <<vPico>>.PinPitch * 5 * (.Occurrences - 1)
FEATURE [PartDesign::Mirrored] Mirrored054  label="Mirror_Boards_SolderedPads_PinPads_Square"
  MirrorPlane = -> YZ_Plane086
  expr: Label = <<Mirror_>> + <<Boards>>.Label + <<_>> + <<SolderedPads>>.Label + <<_PinPads_Square>>
FEATURE [Sketcher::SketchObject] Sketch102  label="Sketch_Boards_SolderedPads_USBPins"
  AttachmentOffset = pos=(-10.5,-25.5,0) rot=(0,0,1;0rad)
  FullyConstrained = true
  MapMode = 5
  Placement = pos=(-10.5,-25.5,0) rot=(0,0,1;0rad)
  Support = -> [XY_Plane086]
  expr: .AttachmentOffset.Base.x = -<<vPico>>.BoardWidth / 2
  expr: .AttachmentOffset.Base.y = -<<vPico>>.BoardLength / 2
  expr: Constraints[14] = <<vPico>>.TPABRadius
  expr: Constraints[15] = <<vPico>>.TPCDRadius
  expr: Constraints[16] = <<vPico>>.TPABHeight - <<vPico>>.TPABRadius * 2
  expr: Constraints[17] = <<vPico>>.TPCDHeight - <<vPico>>.TPCDRadius * 2
  expr: Constraints[18] = <<vPico>>.TPPosA.x
  expr: Constraints[19] = <<vPico>>.TPPosC.x
  expr: Constraints[20] = <<vPico>>.TPPosC.y
  expr: Constraints[21] = <<vPico>>.TPPosA.y
  expr: Label = <<Sketch_>> + <<Boards>>.Label + <<_>> + <<SolderedPads>>.Label + <<_USBPins>>
  sketch-geometry (10):
    g0: ArcOfCircle CenterX=7.775 CenterY=49.85 CenterZ=0 NormalX=0 NormalY=0 NormalZ=1 AngleXU=0 Radius=0.55 StartAngle=8e-16 EndAngle=3.14159
    g1: ArcOfCircle CenterX=7.775 CenterY=49.15 CenterZ=0 NormalX=0 NormalY=0 NormalZ=1 AngleXU=0 Radius=0.55 StartAngle=3.14159 EndAngle=6.28319
    g2: LineSegment StartX=7.225 StartY=49.85 StartZ=0 EndX=7.225 EndY=49.15 EndZ=0
    g3: LineSegment StartX=8.325 StartY=49.15 StartZ=0 EndX=8.325 EndY=49.85 EndZ=0
    g4: ArcOfCircle CenterX=8.075 CenterY=46.67 CenterZ=0 NormalX=0 NormalY=0 NormalZ=1 AngleXU=0 Radius=0.525 StartAngle=2.9e-15 EndAngle=3.14159
    g5: ArcOfCircle CenterX=8.075 CenterY=46.27 CenterZ=0 NormalX=0 NormalY=0 NormalZ=1 AngleXU=0 Radius=0.525 StartAngle=3.14159 EndAngle=6.28319
    g6: LineSegment StartX=7.55 StartY=46.67 StartZ=0 EndX=7.55 EndY=46.27 EndZ=0
    g7: LineSegment StartX=8.6 StartY=46.27 StartZ=0 EndX=8.6 EndY=46.67 EndZ=0
    g8: GeomPoint X=7.775 Y=49.5 Z=0
    g9: GeomPoint X=8.075 Y=46.47 Z=0
  constraints (22):
    c: Tangent(g0,g2) = -1.5708
    c: Tangent(g2,g1) = -1.5708
    c: Tangent(g1,g3) = -1.5708
    c: Tangent(g3,g0) = -1.5708
    c: Equal(g0,g1)
    c: Vertical(g2)
    c: Tangent(g4,g6) = -1.5708
    c: Tangent(g6,g5) = -1.5708
    c: Tangent(g5,g7) = -1.5708
    c: Tangent(g7,g4) = -1.5708
    c: Equal(g4,g5)
    c: Vertical(g6)
    c: Symmetric(g1,g0,g8)
    c: Symmetric(g5,g4,g9)
    c: Radius(g0) = 0.55
    c: Radius(g4) = 0.525
    c: Distance(g2) = 0.7
    c: Distance(g6) = 0.4
    c: Distance(g8,g-2) = 7.775
    c: Distance(g9,g-2) = 8.075
    c: Distance(g9,g-1) = 46.47
    c: Distance(g8,g-1) = 49.5
FEATURE [App::Link] Link220  label="Tool_Boards_SolderedPads_Pico"
  LinkedObject = -> Mirrored055
  expr: Label = <<Tool_>> + <<Boards>>.Label + <<_>> + <<SolderedPads>>.Label + <<_Pico>>
FEATURE [Part::Part2DObjectPython] Clone2D019  label="EXTREF_Clone_Sketch_Boards_SolderedPads_Core_GoldPads"  # Draft 2D object (typed FeaturePython)
  AttachmentOffset = pos=(0,0,0.5) rot=(0,0,1;0rad)
  Fuse = false
  MapMode = 5
  Objects = -> [Sketch099]
  Placement = pos=(0,0,0.5) rot=(0,0,1;0rad)
  Scale = (1,1,1)
  Support = -> [XY_Plane085]
  expr: .AttachmentOffset.Base.z = <<vPico>>.BoardThickness / 2
  expr: Label = <<EXTREF_Clone_>> + Objects[0].Label + <<_>> + <<GoldPads>>.Label
FEATURE [PartDesign::Pad] Pad098  label="EXTREF_Pad_Boards_GoldPads_Core"
  Direction = (0,0,1)
  Length = 0.5
  Length2 = 10
  Midplane = true
  Profile = -> Clone2D019
  ReferenceAxis = -> Clone2D019 [N_Axis]
  Type = 0
  expr: Label = <<EXTREF_Pad_>> + <<Boards>>.Label + <<_>> + <<GoldPads>>.Label + <<_Core>>
  expr: Length = <<vPico>>.BoardThickness / 2
FEATURE [PartDesign::MultiTransform] MultiTransform027  label="MultiTransform_Boards_GoldPads_Core"
  BaseFeature = -> Pad098
  Originals = -> [Pad098]
  Refine = true
  Transformations = -> [Mirrored048,Mirrored049]
  expr: Label = <<MultiTransform_>> + <<Boards>>.Label + <<_>> + <<GoldPads>>.Label + <<_Core>>
FEATURE [PartDesign::CoordinateSystem] Local_CS  label="Local_CS_Boards_SolderedPads_TPCoordinateOrigin"
  AttacherType = Attacher::AttachEngine3D
  AttachmentOffset = pos=(-10.5,-25.5,0) rot=(0,0,1;0rad)
  MapMode = 5
  Placement = pos=(-10.5,-25.5,0) rot=(0,0,1;0rad)
  Support = -> [XY_Plane086]
  expr: .AttachmentOffset.Base.x = -<<vPico>>.BoardWidth / 2
  expr: .AttachmentOffset.Base.y = -<<vPico>>.BoardLength / 2
  expr: Label = <<Local_CS_>> + <<Boards>>.Label + <<_>> + <<SolderedPads>>.Label + <<_TPCoordinateOrigin>>
FEATURE [Sketcher::SketchObject] Sketch103  label="Sketch_Boards_SolderedPads_TP"
  AttachmentOffset = pos=(9.5,49.8,0) rot=(0,0,1;0rad)
  FullyConstrained = true
  MapMode = 5
  Placement = pos=(-1,24.3,0) rot=(0,0,1;0rad)
  Support = -> [Local_CS]
  expr: .AttachmentOffset.Base = <<vPico>>.TPPos2
  expr: Constraints[16] = <<vPico>>.TPRadius
  expr: Constraints[17] = <<vPico>>.TPWidth
  expr: Label = <<Sketch_>> + <<Boards>>.Label + <<_>> + <<SolderedPads>>.Label + <<_TP>>
  sketch-geometry (8):
    g0: LineSegment StartX=-0.45 StartY=0.75 StartZ=0 EndX=0.45 EndY=0.75 EndZ=0
    g1: LineSegment StartX=0.75 StartY=0.45 StartZ=0 EndX=0.75 EndY=-0.45 EndZ=0
    g2: LineSegment StartX=0.45 StartY=-0.75 StartZ=0 EndX=-0.45 EndY=-0.75 EndZ=0
    g3: LineSegment StartX=-0.75 StartY=-0.45 StartZ=0 EndX=-0.75 EndY=0.45 EndZ=0
    g4: ArcOfCircle CenterX=-0.45 CenterY=0.45 CenterZ=0 NormalX=0 NormalY=0 NormalZ=1 AngleXU=0 Radius=0.3 StartAngle=1.5708 EndAngle=3.14159
    g5: ArcOfCircle CenterX=0.45 CenterY=0.45 CenterZ=0 NormalX=0 NormalY=0 NormalZ=1 AngleXU=0 Radius=0.3 StartAngle=0 EndAngle=1.5708
    g6: ArcOfCircle CenterX=0.45 CenterY=-0.45 CenterZ=0 NormalX=0 NormalY=0 NormalZ=1 AngleXU=0 Radius=0.3 StartAngle=4.71239 EndAngle=6.28319
    g7: ArcOfCircle CenterX=-0.45 CenterY=-0.45 CenterZ=0 NormalX=0 NormalY=0 NormalZ=1 AngleXU=0 Radius=0.3 StartAngle=3.14159 EndAngle=4.71239
  constraints (19):
    c: Vertical(g3)
    c: Parallel(g3,g1)
    c: Parallel(g2,g0)
    c: Perpendicular(g2,g3)
    c: Tangent(g0,g4) = 1.5708
    c: Tangent(g3,g4) = 1.5708
    c: Tangent(g0,g5) = 1.5708
    c: Tangent(g1,g5) = 1.5708
    c: Tangent(g1,g6) = 1.5708
    c: Tangent(g2,g6) = 1.5708
    c: Tangent(g2,g7) = 1.5708
    c: Tangent(g3,g7) = 1.5708
    c: Equal(g3,g2)
    c: Equal(g7,g4)
    c: Equal(g7,g5)
    c: Equal(g7,g6)
    c: Radius(g7) = 0.3
    c: Distance(g2,g0) = 1.5
    c: Symmetric(g7,g5,g-1)
FEATURE [Part::Part2DObjectPython] Clone2D020  label="Clone_Sketch_Boards_SolderedPads_TP_TP1"  # Draft 2D object (typed FeaturePython)
  AttachmentOffset = pos=(9.775,47.225,0) rot=(0,0,1;0rad)
  Fuse = false
  MapMode = 5
  Objects = -> [Sketch103]
  Placement = pos=(-0.725,21.725,0) rot=(0,0,1;0rad)
  Scale = (1,1,1)
  Support = -> [Local_CS]
  expr: .AttachmentOffset.Base = <<vPico>>.TPPos1 + <<vPicoH>>.TP1Offset
  expr: Label = <<Clone_>> + Objects[0].Label + <<_TP1>>
FEATURE [Part::Part2DObjectPython] Clone2D021  label="Clone_Sketch_Boards_SolderedPads_TP_TP4"  # Draft 2D object (typed FeaturePython)
  AttachmentOffset = pos=(8,41.5,0) rot=(0,0,1;0rad)
  Fuse = false
  MapMode = 5
  Objects = -> [Sketch103]
  Placement = pos=(-2.5,16,0) rot=(0,0,1;0rad)
  Scale = (1,1,1)
  Support = -> [Local_CS]
  expr: .AttachmentOffset.Base = <<vPico>>.TPPos4 + <<vPicoH>>.TP5Offset
  expr: Label = <<Clone_>> + Objects[0].Label + <<_TP4>>
FEATURE [Part::Part2DObjectPython] Clone2D022  label="Clone_Sketch_Boards_SolderedPads_TP_TPDebug_PicoH"  # Draft 2D object (typed FeaturePython)
  AttachmentOffset = pos=(-2.54,-23.9,0) rot=(0,0,1;0rad)
  Fuse = false
  MapMode = 5
  Objects = -> [Sketch103]
  Placement = pos=(-2.54,-23.9,0) rot=(0,0,1;0rad)
  Scale = (1,1,1)
  Support = -> [XY_Plane086]
  expr: .AttachmentOffset.Base.x = <<vPico>>.DebugCenter.x - <<vPico>>.PinPitch
  expr: .AttachmentOffset.Base.y = <<vPico>>.DebugCenter.y
  expr: Label = <<Clone_>> + Objects[0].Label + <<_TPDebug_PicoH>>
FEATURE [Part::Part2DObjectPython] Clone2D023  label="Clone_Sketch_Boards_SolderedPads_TP_TPDebug_PicoWH"  # Draft 2D object (typed FeaturePython)
  AttachmentOffset = pos=(0.5841,-5.7,0) rot=(0,0,1;0rad)
  Fuse = false
  MapMode = 5
  Objects = -> [Sketch103]
  Placement = pos=(0.5841,-5.7,0) rot=(0,0,1;0rad)
  Scale = (1,1,1)
  Support = -> [XY_Plane086]
  expr: .AttachmentOffset.Base.x = <<vPicoWH>>.TPDebugCenter.x - <<vPico>>.PinPitch
  expr: .AttachmentOffset.Base.y = <<vPicoWH>>.TPDebugCenter.y
  expr: Label = <<Clone_>> + Objects[0].Label + <<_TPDebug_PicoWH>>
FEATURE [PartDesign::CoordinateSystem] Local_CS001  label="Local_CS_Boards_GoldPads_TPCoordinateOrigin"
  AttacherType = Attacher::AttachEngine3D
  AttachmentOffset = pos=(-10.5,-25.5,0) rot=(0,0,1;0rad)
  MapMode = 5
  Placement = pos=(-10.5,-25.5,0) rot=(0,0,1;0rad)
  Support = -> [XY_Plane085]
  expr: .AttachmentOffset.Base.x = -<<vPico>>.BoardWidth / 2
  expr: .AttachmentOffset.Base.y = -<<vPico>>.BoardLength / 2
  expr: Label = <<Local_CS_>> + <<Boards>>.Label + <<_>> + <<GoldPads>>.Label + <<_TPCoordinateOrigin>>
FEATURE [Part::Part2DObjectPython] Clone2D024  label="EXTREF_Clone_Sketch_Boards_SolderedPads_TP_GoldPads_TP2"  # Draft 2D object (typed FeaturePython)
  AttachmentOffset = pos=(9.5,49.8,0) rot=(0,0,1;0rad)
  Fuse = false
  MapMode = 5
  Objects = -> [Sketch103]
  Placement = pos=(-1,24.3,0) rot=(0,0,1;0rad)
  Scale = (1,1,1)
  Support = -> [Local_CS001]
  expr: .AttachmentOffset.Base = <<vPico>>.TPPos2
  expr: Label = <<EXTREF_Clone_>> + Objects[0].Label + <<_>> + <<GoldPads>>.Label + <<_TP2>>
FEATURE [Part::Part2DObjectPython] Clone2D025  label="EXTREF_Clone_Sketch_Boards_SolderedPads_TP_GoldPads_TP1"  # Draft 2D object (typed FeaturePython)
  AttachmentOffset = pos=(10.5,46.5,0) rot=(0,0,1;0rad)
  Fuse = false
  MapMode = 5
  Objects = -> [Sketch103]
  Placement = pos=(0,21,0) rot=(0,0,1;0rad)
  Scale = (1,1,1)
  Support = -> [Local_CS001]
  expr: .AttachmentOffset.Base = <<vPico>>.TPPos1
  expr: Label = <<EXTREF_Clone_>> + Objects[0].Label + <<_>> + <<GoldPads>>.Label + <<_TP1>>
FEATURE [Part::Part2DObjectPython] Clone2D026  label="EXTREF_Clone_Sketch_Boards_SolderedPads_TP_GoldPads_TP4"  # Draft 2D object (typed FeaturePython)
  AttachmentOffset = pos=(8,43,0) rot=(0,0,1;0rad)
  Fuse = false
  MapMode = 5
  Objects = -> [Sketch103]
  Placement = pos=(-2.5,17.5,0) rot=(0,0,1;0rad)
  Scale = (1,1,1)
  Support = -> [Local_CS001]
  expr: .AttachmentOffset.Base = <<vPico>>.TPPos4
  expr: Label = <<EXTREF_Clone_>> + Objects[0].Label + <<_>> + <<GoldPads>>.Label + <<_TP4>>
FEATURE [PartDesign::LinearPattern] LinearPattern076  label="LinearPattern_Boards_GoldPads_PinPads_Round_Castellated_2"
  Direction = -> Y_Axis085
  Length = 7.62
  Occurrences = 2
  Reversed = true
  expr: Label = <<LinearPattern_>> + <<Boards>>.Label + <<_>> + <<GoldPads>>.Label + <<_PinPads_Round_Castellated_2>>
  expr: Length = <<vPico>>.PinPitch * 3 * (Occurrences - 1)
FEATURE [PartDesign::LinearPattern] LinearPattern077  label="LinearPattern_Boards_GoldPads_PinPads_Round_Castellated_3"
  Direction = -> Y_Axis085
  Length = 38.1
  Occurrences = 4
  Reversed = true
  expr: Label = <<LinearPattern_>> + <<Boards>>.Label + <<_>> + <<GoldPads>>.Label + <<_PinPads_Round_Castellated_3>>
  expr: Length = <<vPico>>.PinPitch * 5 * (Occurrences - 1)
FEATURE [Sketcher::SketchObject] Sketch104  label="Sketch_Boards_GoldPads_PinPad_Square_Castellated"
  AttachmentOffset = pos=(0,-5.08,0) rot=(0,0,1;0rad)
  FullyConstrained = true
  MapMode = 2
  Placement = pos=(-8.89,19.05,0) rot=(0,0,1;0rad)
  Support = -> [Sketch096]
  expr: .AttachmentOffset.Base.y = -<<vPico>>.PinPitch * 2
  expr: Constraints[14] = <<vPico>>.PinPadWidth
  expr: Constraints[20] = <<vPico>>.PinSquarePadRadius
  expr: Constraints[21] = <<vPico>>.PinPadWidth / 2
  expr: Constraints[24] = <<vPico>>.PinToCastellationCenter
  expr: Constraints[25] = <<vPico>>.PinInset
  expr: Constraints[2] = <<vPico>>.PinHoleDiameter
  expr: Label = <<Sketch_>> + <<Boards>>.Label + <<_>> + <<GoldPads>>.Label + <<_PinPad_Square_Castellated>>
  sketch-geometry (9):
    g0: ArcOfCircle CenterX=0 CenterY=0 CenterZ=0 NormalX=0 NormalY=0 NormalZ=1 AngleXU=0 Radius=0.5 StartAngle=3.14159 EndAngle=9.42478
    g1: LineSegment StartX=0.6 StartY=0.8 StartZ=0 EndX=-1.61 EndY=0.8 EndZ=0
    g2: LineSegment StartX=0.6 StartY=-0.8 StartZ=0 EndX=-1.61 EndY=-0.8 EndZ=0
    g3: LineSegment StartX=-1.61 StartY=0.8 StartZ=0 EndX=-1.61 EndY=0.4999 EndZ=0
    g4: LineSegment StartX=-1.61 StartY=-0.8 StartZ=0 EndX=-1.61 EndY=-0.4999 EndZ=0
    g5: ArcOfCircle CenterX=-1.6 CenterY=0 CenterZ=0 NormalX=0 NormalY=0 NormalZ=1 AngleXU=0 Radius=0.5 StartAngle=4.69239 EndAngle=7.87398
    g6: LineSegment StartX=0.8 StartY=0.6 StartZ=0 EndX=0.8 EndY=-0.6 EndZ=0
    g7: ArcOfCircle CenterX=0.6 CenterY=0.6 CenterZ=0 NormalX=0 NormalY=0 NormalZ=1 AngleXU=0 Radius=0.2 StartAngle=2e-16 EndAngle=1.5708
    g8: ArcOfCircle CenterX=0.6 CenterY=-0.6 CenterZ=0 NormalX=0 NormalY=0 NormalZ=1 AngleXU=0 Radius=0.2 StartAngle=4.71239 EndAngle=6.28319
  constraints (26):
    c: PointOnObject(g0,g-1)
    c: PointOnObject(g0,g-1)
    c: Diameter(g0) = 1
    c: Coincident(g3,g1)
    c: Coincident(g4,g2)
    c: Coincident(g5,g3)
    c: Coincident(g5,g4)
    c: Horizontal(g2)
    c: Parallel(g1,g2)
    c: Perpendicular(g2,g4)
    c: PointOnObject(g1,g4)
    c: PointOnObject(g3,g4)
    c: PointOnObject(g5,g-1)
    c: Equal(g5,g0)
    c: Distance(g1,g2) = 1.6
    c: Tangent(g1,g7) = -1.5708
    c: Tangent(g6,g7) = 1.5708
    c: Tangent(g2,g8) = 1.5708
    c: Tangent(g6,g8) = 1.5708
    c: Equal(g7,g8)
    c: Radius(g7) = 0.2
    c: Distance(g0,g6) = 0.8
    c: Coincident(g0,g-1)
    c: Symmetric(g6,g6,g-1)
    c: Distance(g5,g0) = 1.6
    c: Distance(g0,g4) = 1.61
FEATURE [PartDesign::LinearPattern] LinearPattern078  label="LinearPattern_Boards_GoldPads_PinPad_Square_Castellated"
  Direction = -> Y_Axis085
  Length = 38.1
  Occurrences = 4
  Reversed = true
  expr: Label = <<LinearPattern_>> + <<Boards>>.Label + <<_>> + <<GoldPads>>.Label + <<_PinPad_Square_Castellated>>
  expr: Length = <<vPico>>.PinPitch * 5 * (Occurrences - 1)
FEATURE [PartDesign::Mirrored] Mirrored058  label="Mirror_Boards_GoldPads_PinPad_Square_Castellated"
  MirrorPlane = -> YZ_Plane085
  expr: Label = <<Mirror_>> + <<Boards>>.Label + <<_>> + <<GoldPads>>.Label + <<_PinPad_Square_Castellated>>
FEATURE [Part::Part2DObjectPython] Clone2D027  label="Clone_Sketch_Boards_GoldPads_PinPad_Round_Castellated_Debug"  # Draft 2D object (typed FeaturePython)
  AttachmentOffset = pos=(-2.54,-23.9,0) rot=(0,0,1;1.5708rad)
  Fuse = false
  MapMode = 2
  Objects = -> [Sketch096]
  Placement = pos=(-2.54,-23.9,0) rot=(0,0,1;1.5708rad)
  Scale = (1,1,1)
  Support = -> [XY_Plane085]
  expr: .AttachmentOffset.Base.x = <<vPico>>.DebugCenter.x - <<vPico>>.PinPitch
  expr: .AttachmentOffset.Base.y = <<vPico>>.DebugCenter.y
  expr: Label = <<Clone_>> + Objects[0].Label + <<_Debug>>
FEATURE [Part::Part2DObjectPython] Clone2D028  label="Clone_Sketch_Boards_GoldPads_PinPad_Square_Castellated_Debug"  # Draft 2D object (typed FeaturePython)
  AttachmentOffset = pos=(0,-23.9,0) rot=(0,0,1;1.5708rad)
  Fuse = false
  MapMode = 5
  Objects = -> [Sketch104]
  Placement = pos=(0,-23.9,0) rot=(0,0,1;1.5708rad)
  Scale = (1,1,1)
  Support = -> [XY_Plane085]
  expr: .AttachmentOffset.Base = <<vPico>>.DebugCenter
  expr: Label = <<Clone_>> + Objects[0].Label + <<_Debug>>
FEATURE [Sketcher::SketchObject] Sketch105  label="Sketch_Boards_GoldPads_CleanCastellatedDebugPins"
  AttachmentOffset = pos=(0,-25.5,0) rot=(0,0,1;0rad)
  FullyConstrained = true
  MapMode = 5
  Placement = pos=(0,-25.5,0) rot=(0,0,1;0rad)
  Support = -> [XY_Plane085]
  expr: .AttachmentOffset.Base.y = -<<vPico>>.BoardLength / 2
  expr: Constraints[10] = <<vPico>>.PinInset + <<vPico>>.PinPadWidth / 2
  expr: Constraints[9] = <<vPico>>.PinPitch * 3 + <<vPico>>.PinPadWidth
  expr: Label = <<Sketch_>> + <<Boards>>.Label + <<_>> + <<GoldPads>>.Label + <<_CleanCastellatedDebugPins>>
  sketch-geometry (4):
    g0: LineSegment StartX=-4.61 StartY=0 StartZ=0 EndX=4.61 EndY=-1e-16 EndZ=0
    g1: LineSegment StartX=4.61 StartY=-1e-16 StartZ=0 EndX=4.61 EndY=-2.41 EndZ=0
    g2: LineSegment StartX=4.61 StartY=-2.41 StartZ=0 EndX=-4.61 EndY=-2.41 EndZ=0
    g3: LineSegment StartX=-4.61 StartY=-2.41 StartZ=0 EndX=-4.61 EndY=0 EndZ=0
  constraints (11):
    c: Coincident(g0,g1)
    c: Coincident(g1,g2)
    c: Coincident(g2,g3)
    c: Coincident(g3,g0)
    c: PointOnObject(g0,g-1)
    c: Symmetric(g0,g0,g-1)
    c: Parallel(g0,g2)
    c: Parallel(g3,g1)
    c: Perpendicular(g3,g0)
    c: Distance(g0) = 9.22
    c: Distance(g3) = 2.41
FEATURE [Part::Part2DObjectPython] Clone2D029  label="EXTREF_Clone_Sketch_Boards_SolderedPads_PinPad_Round_GoldPads"  # Draft 2D object (typed FeaturePython)
  AttachmentOffset = pos=(3.1241,-5.7,0) rot=(0,0,1;1.5708rad)
  Fuse = false
  MapMode = 5
  Objects = -> [Sketch100]
  Placement = pos=(3.1241,-5.7,0) rot=(0,0,1;1.5708rad)
  Scale = (1,1,1)
  Support = -> [XY_Plane085]
  expr: .AttachmentOffset.Base = <<vPicoW>>.DebugCenter
  expr: Label = <<EXTREF_Clone_>> + Objects[0].Label + <<_>> + <<GoldPads>>.Label
FEATURE [Part::Part2DObjectPython] Clone2D030  label="EXTREF_Clone_Sketch_Boards_SolderedPads_PinPad_Square_GoldPads"  # Draft 2D object (typed FeaturePython)
  AttachmentOffset = pos=(0.5841,-5.7,0) rot=(0,0,1;1.5708rad)
  Fuse = false
  MapMode = 5
  Objects = -> [Sketch101]
  Placement = pos=(0.5841,-5.7,0) rot=(0,0,1;1.5708rad)
  Scale = (1,1,1)
  Support = -> [XY_Plane085]
  expr: .AttachmentOffset.Base.x = <<vPicoW>>.DebugCenter.x - <<vPico>>.PinPitch
  expr: .AttachmentOffset.Base.y = <<vPicoW>>.DebugCenter.y
  expr: Label = <<EXTREF_Clone_>> + Objects[0].Label + <<_>> + <<GoldPads>>.Label
FEATURE [Sketcher::SketchObject] Sketch106  label="Sketch_Boards_GoldPads_PicoWMountingHoleRim"
  AttachmentOffset = pos=(-5.7,-23.5,0) rot=(0,0,1;0rad)
  FullyConstrained = true
  MapMode = 5
  Placement = pos=(-5.7,-23.5,0) rot=(0,0,1;0rad)
  Support = -> [XY_Plane085]
  expr: .AttachmentOffset.Base.x = -(<<vPico>>.BoardWidth / 2 - <<vPico>>.BoardMountingHoleInset.x)
  expr: .AttachmentOffset.Base.y = -(<<vPico>>.BoardLength / 2 - <<vPico>>.BoardMountingHoleInset.y)
  expr: Constraints[2] = <<vPico>>.BoardMountingHoleDiameter
  expr: Constraints[3] = <<vPicoW>>.LowerMountingHoleMarginDiameter
  expr: Label = <<Sketch_>> + <<Boards>>.Label + <<_>> + <<GoldPads>>.Label + <<_PicoWMountingHoleRim>>
  sketch-geometry (2):
    g0: Circle CenterX=0 CenterY=0 CenterZ=0 NormalX=0 NormalY=0 NormalZ=1 AngleXU=0 Radius=1.05
    g1: Circle CenterX=0 CenterY=0 CenterZ=0 NormalX=0 NormalY=0 NormalZ=1 AngleXU=0 Radius=1.5
  constraints (4):
    c: Coincident(g0,g-1)
    c: Coincident(g1,g0)
    c: Diameter(g0) = 2.1
    c: Diameter(g1) = 3
FEATURE [App::Link] Link221  label="Tool_Boards_SolderedPads_PicoH"
  LinkedObject = -> LinearPattern073
  expr: Label = <<Tool_>> + <<Boards>>.Label + <<_>> + <<SolderedPads>>.Label + <<_PicoH>>
FEATURE [App::Link] Link222  label="Tool_Boards_SolderedPads_PicoWH"
  LinkedObject = -> LinearPattern074
  expr: Label = <<Tool_>> + <<Boards>>.Label + <<_>> + <<SolderedPads>>.Label + <<_PicoWH>>
FEATURE [Sketcher::SketchObject] Sketch107  label="Sketch_Remove_Boards_SolderedPads_TPDebug_PicoH"
  AttachmentOffset = pos=(0,-23.9,0) rot=(0,0,1;0rad)
  FullyConstrained = true
  MapMode = 5
  Placement = pos=(0,-23.9,0) rot=(0,0,1;0rad)
  Support = -> [XY_Plane086]
  expr: .AttachmentOffset.Base = <<vPico>>.DebugCenter
  expr: Constraints[10] = (<<vPico>>.PinInset + <<vPico>>.PinPadWidth) * 2
  expr: Constraints[9] = <<vPico>>.PinPitch * 3 + <<vPico>>.PinPadWidth
  expr: Label = <<Sketch_Remove_>> + <<Boards>>.Label + <<_>> + <<SolderedPads>>.Label + <<_TPDebug_PicoH>>
  sketch-geometry (4):
    g0: LineSegment StartX=-4.61 StartY=3.21 StartZ=0 EndX=4.61 EndY=3.21 EndZ=0
    g1: LineSegment StartX=4.61 StartY=3.21 StartZ=0 EndX=4.61 EndY=-3.21 EndZ=0
    g2: LineSegment StartX=4.61 StartY=-3.21 StartZ=0 EndX=-4.61 EndY=-3.21 EndZ=0
    g3: LineSegment StartX=-4.61 StartY=-3.21 StartZ=0 EndX=-4.61 EndY=3.21 EndZ=0
  constraints (11):
    c: Coincident(g0,g1)
    c: Coincident(g1,g2)
    c: Coincident(g2,g3)
    c: Coincident(g3,g0)
    c: Horizontal(g0)
    c: Symmetric(g2,g0,g-1)
    c: Parallel(g0,g2)
    c: Parallel(g3,g1)
    c: Perpendicular(g3,g0)
    c: Distance(g0) = 9.22
    c: Distance(g3) = 6.42
FEATURE [App::Link] Link223  label="Tool_Boards_GoldPads_PicoW_MountingHoleRim"
  LinkedObject = -> Mirrored060
  expr: Label = <<Tool_>> + <<Boards>>.Label + <<_>> + <<GoldPads>>.Label + <<_PicoW_MountingHoleRim>>
FEATURE [App::Link] Link224  label="Tool_Boards_GoldPads_Pico"
  LinkedObject = -> Pocket039
  expr: Label = <<Tool_>> + <<Boards>>.Label + <<_>> + <<GoldPads>>.Label + <<_Pico>>
FEATURE [App::Link] Link225  label="Tool_Boards_GoldPads_PicoW"
  LinkedObject = -> Pad111
  expr: Label = <<Tool_>> + <<Boards>>.Label + <<_>> + <<GoldPads>>.Label + <<_PicoW>>
FEATURE [App::Link] Link226  label="Tool_Board_Pico_SolderedPads"
  LinkedObject = -> Link220
  expr: Label = <<Tool_Board_Pico_>> + <<SolderedPads>>.Label
FEATURE [App::Link] Link227  label="Tool_Board_PicoH_SolderedPads"
  LinkedObject = -> Link221
  expr: Label = <<Tool_Board_PicoH_>> + <<SolderedPads>>.Label
FEATURE [App::Link] Link228  label="Tool_Board_PicoW_SolderedPads"
  LinkedObject = -> Link220
  expr: Label = <<Tool_Board_PicoW_>> + <<SolderedPads>>.Label
FEATURE [App::Link] Link229  label="Tool_Board_PicoWH_SolderedPads"
  LinkedObject = -> Link222
  expr: Label = <<Tool_Board_PicoWH_>> + <<SolderedPads>>.Label
FEATURE [App::Link] Link230  label="Tool_Board_Pico_GoldPads"
  LinkedObject = -> Link224
  expr: Label = <<Tool_Board_Pico_>> + <<GoldPads>>.Label
FEATURE [App::Link] Link231  label="Tool_Board_PicoW_GoldPads"
  LinkedObject = -> Link225
  expr: Label = <<Tool_Board_PicoW_>> + <<GoldPads>>.Label
FEATURE [App::Link] Link232  label="Tool_Board_PicoW_GoldPads_MountingHoleRim"
  LinkedObject = -> Link223
  expr: Label = <<Tool_Board_PicoW_>> + <<GoldPads>>.Label + <<_MountingHoleRim>>
FEATURE [App::Link] Link233  label="Tool_Board_PicoWH_GoldPads_MountingHoleRim"
  LinkedObject = -> Link223
  expr: Label = <<Tool_Board_PicoWH_>> + <<GoldPads>>.Label + <<_MountingHoleRim>>
FEATURE [Part::MultiFuse] Fusion  label="Pico_Board"
  Shapes = -> [Cut001,Link226,Link230]
FEATURE [Part::MultiFuse] Fusion001  label="Pico_H_Board"
  Shapes = -> [Cut002,Link227]
FEATURE [Part::MultiFuse] Fusion003  label="Pico_WH_Board"
  Shapes = -> [Cut004,Link229,Link233]
FEATURE [Sketcher::SketchObject] Sketch108  label="Sketch_Boards_SolderedPads_Core_PicoWDebugClearance"
  AttachmentOffset = pos=(3.1241,-5.7,0) rot=(0,0,1;0rad)
  FullyConstrained = true
  MapMode = 5
  Placement = pos=(3.1241,-5.7,0) rot=(0,0,1;0rad)
  Support = -> [XY_Plane086]
  expr: .AttachmentOffset.Base.x = <<vPicoW>>.DebugCenter.x
  expr: .AttachmentOffset.Base.y = <<vPicoW>>.DebugCenter.y
  expr: Constraints[7] = <<vPico>>.PinPitch * 2
  expr: Constraints[8] = (<<vPico>>.PinHoleDiameter + <<vPico>>.PinPadWidth) / 2
  expr: Label = <<Sketch_>> + <<Boards>>.Label + <<_>> + <<SolderedPads>>.Label + <<_Core_PicoWDebugClearance>>
  sketch-geometry (5):
    g0: ArcOfCircle CenterX=-2.54 CenterY=-8e-16 CenterZ=0 NormalX=0 NormalY=0 NormalZ=1 AngleXU=0 Radius=0.65 StartAngle=1.5708 EndAngle=4.71239
    g1: ArcOfCircle CenterX=2.54 CenterY=8e-16 CenterZ=0 NormalX=0 NormalY=0 NormalZ=1 AngleXU=0 Radius=0.65 StartAngle=4.71239 EndAngle=7.85398
    g2: LineSegment StartX=-2.54 StartY=-0.65 StartZ=0 EndX=2.54 EndY=-0.65 EndZ=0
    g3: LineSegment StartX=2.54 StartY=0.65 StartZ=0 EndX=-2.54 EndY=0.65 EndZ=0
    g4: GeomPoint X=0 Y=0 Z=0
  constraints (10):
    c: Tangent(g0,g2) = -1.5708
    c: Tangent(g2,g1) = -1.5708
    c: Tangent(g1,g3) = -1.5708
    c: Tangent(g3,g0) = -1.5708
    c: Equal(g0,g1)
    c: Horizontal(g2)
    c: Symmetric(g0,g1,g4)
    c: Distance(g2) = 5.08
    c: Diameter(g0) = 1.3
    c: Coincident(g4,g-1)
FEATURE [PartDesign::Pocket] Pocket043  label="Pad_Boards_SolderedPads_Core_PicoWDebugClearance"
  BaseFeature = -> MultiTransform029
  Direction = (0,0,-1)
  Length = 5
  Length2 = 5
  Midplane = true
  Profile = -> Sketch108
  ReferenceAxis = -> Sketch108 [N_Axis]
  Type = 1
  expr: Label = <<Pad_>> + <<Boards>>.Label + <<_>> + <<SolderedPads>>.Label + <<_Core_PicoWDebugClearance>>
FEATURE [PartDesign::Pad] Pad097  label="Pad_Boards_SolderedPads_USBPins"
  BaseFeature = -> Pocket043
  Direction = (0,0,1)
  Length = 0.5
  Length2 = 10
  Profile = -> Sketch102
  ReferenceAxis = -> Sketch102 [N_Axis]
  Type = 0
  expr: Label = <<Pad_>> + <<Boards>>.Label + <<_>> + <<SolderedPads>>.Label + <<_USBPins>>
  expr: Length = <<vPico>>.BoardThickness / 2
FEATURE [PartDesign::Mirrored] Mirrored055  label="Mirror_Boards_SolderedPads_USBPins"
  BaseFeature = -> Pad097
  MirrorPlane = -> YZ_Plane086
  Originals = -> [Pad097]
  expr: Label = <<Mirror_>> + <<Boards>>.Label + <<_>> + <<SolderedPads>>.Label + <<_USBPins>>
FEATURE [PartDesign::Pad] Pad095  label="Pad_Boards_SolderedPads_PinPad_Round"
  BaseFeature = -> Mirrored055
  Direction = (0,0,1)
  Length = 1
  Length2 = 10
  Profile = -> Sketch100
  ReferenceAxis = -> Sketch100 [N_Axis]
  Type = 0
  expr: Label = <<Pad_>> + <<Boards>>.Label + <<_>> + <<SolderedPads>>.Label + <<_PinPad_Round>>
  expr: Length = <<vPico>>.BoardThickness
FEATURE [PartDesign::MultiTransform] MultiTransform030  label="MultiTransform_Boards_SolderedPads_PinPads_Round"
  BaseFeature = -> Pad095
  Originals = -> [Pad095]
  Transformations = -> [LinearPattern068,LinearPattern070,LinearPattern071,Mirrored053]
  expr: Label = <<MultiTransform_>> + <<Boards>>.Label + <<_>> + <<SolderedPads>>.Label + <<_PinPads_Round>>
FEATURE [PartDesign::Pad] Pad096  label="Pad_Boards_SolderedPads_PinPad_Square"
  BaseFeature = -> MultiTransform030
  Direction = (0,0,1)
  Length = 1
  Length2 = 10
  Profile = -> Sketch101
  ReferenceAxis = -> Sketch101 [N_Axis]
  Type = 0
  expr: Label = <<Pad_>> + <<Boards>>.Label + <<_>> + <<SolderedPads>>.Label + <<_PinPad_Square>>
  expr: Length = <<vPico>>.BoardThickness
FEATURE [PartDesign::MultiTransform] MultiTransform031  label="MultiTransform_Boards_SolderedPads_PinPads_Square"
  BaseFeature = -> Pad096
  Originals = -> [Pad096]
  Transformations = -> [LinearPattern069,Mirrored054]
  expr: Label = <<MultiTransform_>> + <<Boards>>.Label + <<_>> + <<SolderedPads>>.Label + <<_PinPads_Square>>
FEATURE [PartDesign::Pad] Pad099  label="Pad_Boards_SolderedPads_TP2"
  BaseFeature = -> MultiTransform031
  Direction = (0,0,1)
  Length = 0.5
  Length2 = 10
  Profile = -> Sketch103
  ReferenceAxis = -> Sketch103 [N_Axis]
  Type = 0
  expr: Label = <<Pad_>> + <<Boards>>.Label + <<_>> + <<SolderedPads>>.Label + <<_TP2>>
  expr: Length = <<vPico>>.BoardThickness / 2
FEATURE [PartDesign::Mirrored] Mirrored056  label="Mirror_Boards_SolderedPads_TP3"
  BaseFeature = -> Pad099
  MirrorPlane = -> YZ_Plane086
  Originals = -> [Pad099]
  expr: Label = <<Mirror_>> + <<Boards>>.Label + <<_>> + <<SolderedPads>>.Label + <<_TP3>>
FEATURE [PartDesign::Pad] Pad100  label="Pad_Boards_SolderedPads_TP1"
  BaseFeature = -> Mirrored056
  Direction = (0,0,1)
  Length = 0.5
  Length2 = 10
  Profile = -> Clone2D020
  ReferenceAxis = -> Clone2D020 [N_Axis]
  Type = 0
  expr: Label = <<Pad_>> + <<Boards>>.Label + <<_>> + <<SolderedPads>>.Label + <<_TP1>>
  expr: Length = <<vPico>>.BoardThickness / 2
FEATURE [PartDesign::Pad] Pad101  label="Pad_Boards_SolderedPads_TP4"
  BaseFeature = -> Pad100
  Direction = (0,0,1)
  Length = 0.5
  Length2 = 10
  Profile = -> Clone2D021
  ReferenceAxis = -> Clone2D021 [N_Axis]
  Type = 0
  expr: Label = <<Pad_>> + <<Boards>>.Label + <<_>> + <<SolderedPads>>.Label + <<_TP4>>
  expr: Length = <<vPico>>.BoardThickness / 2
FEATURE [PartDesign::LinearPattern] LinearPattern072  label="LinearPattern_Boards_SolderedPads_TPs"
  BaseFeature = -> Pad101
  Direction = -> Y_Axis086
  Length = 5
  Occurrences = 3
  Originals = -> [Pad101]
  Reversed = true
  expr: Label = <<LinearPattern_>> + <<Boards>>.Label + <<_>> + <<SolderedPads>>.Label + <<_TPs>>
  expr: Length = (<<vPico>>.TPPos4.y - <<vPico>>.TPPos5.y) * (Occurrences - 1)
FEATURE [PartDesign::Pad] Pad102  label="Pad_Boards_SolderedPads_TPDebug_PicoH"
  BaseFeature = -> LinearPattern072
  Direction = (0,0,1)
  Length = 0.5
  Length2 = 10
  Profile = -> Clone2D022
  ReferenceAxis = -> Clone2D022 [N_Axis]
  Type = 0
  expr: Label = <<Pad_>> + <<Boards>>.Label + <<_>> + <<SolderedPads>>.Label + <<_TPDebug_PicoH>>
  expr: Length = <<vPico>>.BoardThickness / 2
FEATURE [PartDesign::LinearPattern] LinearPattern073  label="LinearPattern_Boards_SolderedPads_TPDebug_PicoH"
  BaseFeature = -> Pad102
  Direction = -> X_Axis086
  Length = 5.08
  Occurrences = 3
  Originals = -> [Pad102]
  expr: Label = <<LinearPattern_>> + <<Boards>>.Label + <<_>> + <<SolderedPads>>.Label + <<_TPDebug_PicoH>>
  expr: Length = <<vPico>>.PinPitch * (Occurrences - 1)
FEATURE [Part::Part2DObjectPython] Clone2D032  label="EXTREF_Clone_Sketch_Boards_SolderedPads_Core_PicoWDebugClearance_GoldPads"  # Draft 2D object (typed FeaturePython)
  Fuse = false
  Objects = -> [Sketch108]
  Placement = pos=(3.1241,-5.7,0) rot=(0,0,1;0rad)
  Scale = (1,1,1)
  expr: Label = <<EXTREF_Clone_>> + Objects[0].Label + <<_>> + <<GoldPads>>.Label
FEATURE [PartDesign::Pocket] Pocket044  label="EXTREF_Pocket_Boards_GoldPads_Core_PicoWDebugClearance"
  BaseFeature = -> MultiTransform027
  Direction = (0,0,-1)
  Length = 5
  Length2 = 5
  Midplane = true
  Profile = -> Clone2D032
  ReferenceAxis = -> Clone2D032 [N_Axis]
  Type = 1
  expr: Label = <<EXTREF_Pocket_>> + <<Boards>>.Label + <<_>> + <<GoldPads>>.Label + <<_Core_PicoWDebugClearance>>
FEATURE [PartDesign::Pad] Pad112  label="Pad_Boards_GoldPads_PicoWMountingHoleRim"
  BaseFeature = -> Pocket044
  Direction = (0,0,1)
  Length = 1
  Length2 = 10
  Profile = -> Sketch106
  ReferenceAxis = -> Sketch106 [N_Axis]
  Type = 0
  expr: Label = <<Pad_>> + <<Boards>>.Label + <<_>> + <<GoldPads>>.Label + <<_PicoWMountingHoleRim>>
  expr: Length = <<vPico>>.BoardThickness
FEATURE [PartDesign::Mirrored] Mirrored060  label="Mirror_Boards_GoldPads_PicoWMountingHoleRim"
  BaseFeature = -> Pad112
  MirrorPlane = -> YZ_Plane085
  Originals = -> [Pad112]
  expr: Label = <<Mirror_>> + <<Boards>>.Label + <<_>> + <<GoldPads>>.Label + <<_PicoWMountingHoleRim>>
FEATURE [PartDesign::Pocket] Pocket040  label="Pocket_Remove_Boards_GoldPads_PicoWMountingHoleRim"
  BaseFeature = -> Mirrored060
  Direction = (0,0,-1)
  Length = 5
  Length2 = 5
  Midplane = true
  Profile = -> Sketch106
  ReferenceAxis = -> Sketch106 [N_Axis]
  Type = 1
  expr: Label = <<Pocket_Remove_>> + <<Boards>>.Label + <<_>> + <<GoldPads>>.Label + <<_PicoWMountingHoleRim>>
FEATURE [PartDesign::Mirrored] Mirrored061  label="Mirror_Remove_Boards_GoldPads_PicoWMountingHoleRim"
  BaseFeature = -> Pocket040
  MirrorPlane = -> YZ_Plane085
  Originals = -> [Pocket040]
  expr: Label = <<Mirror_Remove_>> + <<Boards>>.Label + <<_>> + <<GoldPads>>.Label + <<_PicoWMountingHoleRim>>
FEATURE [PartDesign::Pad] Pad093  label="Pad_Boards_GoldPads_PinPad_Round_Castellated"
  BaseFeature = -> Mirrored061
  Direction = (0,0,1)
  Length = 1
  Length2 = 10
  Profile = -> Sketch096
  ReferenceAxis = -> Sketch096 [N_Axis]
  Type = 0
  expr: Label = <<Pad_>> + <<Boards>>.Label + <<_>> + <<GoldPads>>.Label + <<_PinPad_Round_Castellated>>
  expr: Length = <<vPico>>.BoardThickness
FEATURE [PartDesign::MultiTransform] MultiTransform028  label="MultiTransform_Boards_GoldPads_PinPads_Round_Castellated"
  BaseFeature = -> Pad093
  Originals = -> [Pad093]
  Transformations = -> [LinearPattern067,LinearPattern076,LinearPattern077,Mirrored050]
  expr: Label = <<MultiTransform_>> + <<Boards>>.Label + <<_>> + <<GoldPads>>.Label + <<_PinPads_Round_Castellated>>
FEATURE [PartDesign::Pad] Pad107  label="Pad_Boards_GoldPads_PinPad_Square_Castellated"
  BaseFeature = -> MultiTransform028
  Direction = (0,0,1)
  Length = 1
  Length2 = 10
  Profile = -> Sketch104
  ReferenceAxis = -> Sketch104 [N_Axis]
  Type = 0
  expr: Label = <<Pad_>> + <<Boards>>.Label + <<_>> + <<GoldPads>>.Label + <<_PinPad_Square_Castellated>>
  expr: Length = <<vPico>>.BoardThickness
FEATURE [PartDesign::MultiTransform] MultiTransform032  label="MultiTransform_Boards_GoldPads_PinPad_Square_Castellated"
  BaseFeature = -> Pad107
  Originals = -> [Pad107]
  Transformations = -> [LinearPattern078,Mirrored058]
  expr: Label = <<MultiTransform_>> + <<Boards>>.Label + <<_>> + <<GoldPads>>.Label + <<_PinPad_Square_Castellated>>
FEATURE [PartDesign::Pad] Pad104  label="EXTREF_Pad_Boards_GoldPads_TP2"
  BaseFeature = -> MultiTransform032
  Direction = (0,0,1)
  Length = 0.5
  Length2 = 10
  Profile = -> Clone2D024
  ReferenceAxis = -> Clone2D024 [N_Axis]
  Type = 0
  expr: Label = <<EXTREF_Pad_>> + <<Boards>>.Label + <<_>> + <<GoldPads>>.Label + <<_TP2>>
  expr: Length = <<vPico>>.BoardThickness / 2
FEATURE [PartDesign::Mirrored] Mirrored057  label="Mirror_Boards_GoldPads_TP3"
  BaseFeature = -> Pad104
  MirrorPlane = -> YZ_Plane085
  Originals = -> [Pad104]
  expr: Label = <<Mirror_>> + <<Boards>>.Label + <<_>> + <<GoldPads>>.Label + <<_TP3>>
FEATURE [PartDesign::Pad] Pad105  label="EXTREF_Pad_Boards_GoldPads_TP1"
  BaseFeature = -> Mirrored057
  Direction = (0,0,1)
  Length = 0.5
  Length2 = 10
  Profile = -> Clone2D025
  ReferenceAxis = -> Clone2D025 [N_Axis]
  Type = 0
  expr: Label = <<EXTREF_Pad_>> + <<Boards>>.Label + <<_>> + <<GoldPads>>.Label + <<_TP1>>
  expr: Length = <<vPico>>.BoardThickness / 2
FEATURE [PartDesign::Pad] Pad106  label="EXTREF_Pad_Boards_GoldPads_TP4"
  BaseFeature = -> Pad105
  Direction = (0,0,1)
  Length = 0.5
  Length2 = 10
  Profile = -> Clone2D026
  ReferenceAxis = -> Clone2D026 [N_Axis]
  Type = 0
  expr: Label = <<EXTREF_Pad_>> + <<Boards>>.Label + <<_>> + <<GoldPads>>.Label + <<_TP4>>
  expr: Length = <<vPico>>.BoardThickness / 2
FEATURE [PartDesign::LinearPattern] LinearPattern075  label="LinearPattern_Boards_GoldPads_TPs"
  BaseFeature = -> Pad106
  Direction = -> Y_Axis085
  Length = 5
  Occurrences = 3
  Originals = -> [Pad106]
  Reversed = true
  expr: Label = <<LinearPattern_>> + <<Boards>>.Label + <<_>> + <<GoldPads>>.Label + <<_TPs>>
  expr: Length = (<<vPico>>.TPPos4.y - <<vPico>>.TPPos5.y) * (Occurrences - 1)
FEATURE [PartDesign::Pad] Pad108  label="Pad_Boards_GoldPads_PinPad_Round_Castellated_Debug"
  BaseFeature = -> LinearPattern075
  Direction = (0,0,1)
  Length = 1
  Length2 = 10
  Profile = -> Clone2D027
  ReferenceAxis = -> Clone2D027 [N_Axis]
  Type = 0
  expr: Label = <<Pad_>> + <<Boards>>.Label + <<_>> + <<GoldPads>>.Label + <<_PinPad_Round_Castellated_Debug>>
  expr: Length = <<vPico>>.BoardThickness
FEATURE [PartDesign::Mirrored] Mirrored059  label="Mirror_Boards_GoldPads_PinPad_Round_Castellated_Debug"
  BaseFeature = -> Pad108
  MirrorPlane = -> YZ_Plane085
  Originals = -> [Pad108]
  expr: Label = <<Mirror_>> + <<Boards>>.Label + <<_>> + <<GoldPads>>.Label + <<_PinPad_Round_Castellated_Debug>>
FEATURE [PartDesign::Pad] Pad109  label="Pad_Boards_GoldPads_PinPad_Square_Castellated_Debug"
  BaseFeature = -> Mirrored059
  Direction = (0,0,1)
  Length = 1
  Length2 = 10
  Profile = -> Clone2D028
  ReferenceAxis = -> Clone2D028 [N_Axis]
  Type = 0
  expr: Label = <<Pad_>> + <<Boards>>.Label + <<_>> + <<GoldPads>>.Label + <<_PinPad_Square_Castellated_Debug>>
  expr: Length = <<vPico>>.BoardThickness
FEATURE [PartDesign::Pocket] Pocket039  label="Pocket_Boards_GoldPads_CleanCastellatedDebugPins"
  BaseFeature = -> Pad109
  Direction = (0,0,-1)
  Length = 5
  Length2 = 5
  Midplane = true
  Profile = -> Sketch105
  ReferenceAxis = -> Sketch105 [N_Axis]
  Type = 1
  expr: Label = <<Pocket_>> + <<Boards>>.Label + <<_>> + <<GoldPads>>.Label + <<_CleanCastellatedDebugPins>>
FEATURE [Part::Part2DObjectPython] Clone2D033  label="Clone_Sketch_Boards_Substrate_PinHole_PicoWDebug"  # Draft 2D object (typed FeaturePython)
  AttachmentOffset = pos=(0.5841,-5.7,0) rot=(0,0,1;1.5708rad)
  Fuse = false
  MapMode = 5
  Objects = -> [Sketch086]
  Placement = pos=(0.5841,-5.7,0) rot=(0,0,1;1.5708rad)
  Scale = (1,1,1)
  Support = -> [XY_Plane081]
  expr: .AttachmentOffset.Base.x = <<vPicoW>>.DebugCenter.x - <<vPico>>.PinPitch
  expr: .AttachmentOffset.Base.y = <<vPicoW>>.DebugCenter.y
  expr: Label = <<Clone_>> + Objects[0].Label + <<_PicoWDebug>>
FEATURE [PartDesign::Pocket] Pocket045  label="Pocket_Boards_Substrate_PicoWDebugPinHole"
  BaseFeature = -> MultiTransform025
  Direction = (0,0,-1)
  Length = 5
  Length2 = 5
  Midplane = true
  Profile = -> Clone2D033
  ReferenceAxis = -> Clone2D033 [N_Axis]
  Type = 1
  expr: Label = <<Pocket_>> + <<Boards>>.Label + <<_>> + <<Substrate>>.Label + <<_PicoWDebugPinHole>>
FEATURE [PartDesign::LinearPattern] LinearPattern080  label="LinearPattern_Boards_Substrate_PicoWDebugPinHoles"
  BaseFeature = -> Pocket045
  Direction = -> X_Axis081
  Length = 5.08
  Occurrences = 3
  Originals = -> [Pocket045]
  expr: Label = <<LinearPattern_>> + <<Boards>>.Label + <<_>> + <<Substrate>>.Label + <<_PicoWDebugPinHoles>>
  expr: Length = <<vPico>>.PinPitch * (Occurrences - 1)
FEATURE [Sketcher::SketchObject] Sketch109  label="Sketch_Remove_Boards_Substrate_PicoWDebug"
  AttachmentOffset = pos=(3.1241,-5.7,0) rot=(0,0,1;0rad)
  FullyConstrained = true
  MapMode = 5
  Placement = pos=(3.1241,-5.7,0) rot=(0,0,1;0rad)
  Support = -> [XY_Plane081]
  expr: .AttachmentOffset.Base.x = <<vPicoW>>.DebugCenter.x
  expr: .AttachmentOffset.Base.y = <<vPicoW>>.DebugCenter.y
  expr: Constraints[7] = <<vPico>>.PinPitch * 2
  expr: Constraints[8] = (<<vPico>>.PinHoleDiameter + <<vPico>>.PinPadWidth) / 2
  expr: Label = <<Sketch_Remove_>> + <<Boards>>.Label + <<_>> + <<Substrate>>.Label + <<_PicoWDebug>>
  sketch-geometry (5):
    g0: ArcOfCircle CenterX=-2.54 CenterY=-8e-16 CenterZ=0 NormalX=0 NormalY=0 NormalZ=1 AngleXU=0 Radius=0.65 StartAngle=1.5708 EndAngle=4.71239
    g1: ArcOfCircle CenterX=2.54 CenterY=8e-16 CenterZ=0 NormalX=0 NormalY=0 NormalZ=1 AngleXU=0 Radius=0.65 StartAngle=4.71239 EndAngle=7.85398
    g2: LineSegment StartX=-2.54 StartY=-0.65 StartZ=0 EndX=2.54 EndY=-0.65 EndZ=0
    g3: LineSegment StartX=2.54 StartY=0.65 StartZ=0 EndX=-2.54 EndY=0.65 EndZ=0
    g4: GeomPoint X=0 Y=0 Z=0
  constraints (10):
    c: Tangent(g0,g2) = -1.5708
    c: Tangent(g2,g1) = -1.5708
    c: Tangent(g1,g3) = -1.5708
    c: Tangent(g3,g0) = -1.5708
    c: Equal(g0,g1)
    c: Horizontal(g2)
    c: Symmetric(g0,g1,g4)
    c: Distance(g2) = 5.08
    c: Diameter(g0) = 1.3
    c: Coincident(g4,g-1)
FEATURE [PartDesign::Pad] Pad113  label="Pad_Remove_Boards_Substrate_PicoWDebug"
  BaseFeature = -> LinearPattern080
  Direction = (0,0,1)
  Length = 1
  Length2 = 10
  Profile = -> Sketch109
  ReferenceAxis = -> Sketch109 [N_Axis]
  Refine = true
  Type = 0
  expr: Label = <<Pad_Remove_>> + <<Boards>>.Label + <<_>> + <<Substrate>>.Label + <<_PicoWDebug>>
  expr: Length = <<vPico>>.BoardThickness
FEATURE [PartDesign::Pocket] Pocket033  label="Pocket_Boards_Substrate_DebugPinHole"
  BaseFeature = -> Pad113
  Direction = (0,0,-1)
  Length = 5
  Length2 = 5
  Midplane = true
  Profile = -> Clone2D017
  ReferenceAxis = -> Clone2D017 [N_Axis]
  Type = 1
  expr: Label = <<Pocket_>> + <<Boards>>.Label + <<_>> + <<Substrate>>.Label + <<_DebugPinHole>>
FEATURE [PartDesign::MultiTransform] MultiTransform026  label="MultiLinearPattern_Boards_Substrate_CastellatedDebugPinHoles"
  BaseFeature = -> Pocket033
  Originals = -> [Pocket033]
  Transformations = -> [LinearPattern065,LinearPattern066]
  expr: Label = <<MultiLinearPattern_>> + <<Boards>>.Label + <<_>> + <<Substrate>>.Label + <<_CastellatedDebugPinHoles>>
FEATURE [PartDesign::Body] Body015  label="Boards_Substrate"
  Group = -> [DatumPoint,Sketch084,Pad084,Sketch085,Pocket029,MultiTransform023,Mirrored041,Mirrored042,Sketch086,Pocket030,MultiTransform024,LinearPattern063,Mirrored043,Clone2D015,Pocket031,MultiTransform025,LinearPattern064,Mirrored044,Clone2D033,Pocket045,LinearPattern080,Sketch109,Pad113,Clone2D017,Pocket033,MultiTransform026,LinearPattern065,LinearPattern066]
  Origin = -> Origin081
  Tip = -> MultiTransform026
  expr: Label = <<Boards>>.Label + <<_>> + <<Substrate>>.Label
FEATURE [Part::Part2DObjectPython] Clone2D034  label="EXTREF_Clone_Sketch_Remove_Boards_Substrate_PicoWDebug_SolderedPads"  # Draft 2D object (typed FeaturePython)
  Fuse = false
  Objects = -> [Sketch109]
  Placement = pos=(3.1241,-5.7,0) rot=(0,0,1;0rad)
  Scale = (1,1,1)
  expr: Label = <<EXTREF_Clone_>> + Objects[0].Label + <<_>> + <<SolderedPads>>.Label
FEATURE [PartDesign::Pocket] Pocket046  label="EXTREF_Pocket_Boards_SolderedPads_PicoWDebugPins"
  BaseFeature = -> LinearPattern073
  Direction = (0,0,-1)
  Length = 5
  Length2 = 5
  Midplane = true
  Profile = -> Clone2D034
  ReferenceAxis = -> Clone2D034 [N_Axis]
  Type = 1
  expr: Label = <<EXTREF_Pocket_>> + <<Boards>>.Label + <<_>> + <<SolderedPads>>.Label + <<_PicoWDebugPins>>
FEATURE [PartDesign::Pocket] Pocket041  label="Pocket_Remove_Boards_SolderedPads_TPDebug_PicoH"
  BaseFeature = -> Pocket046
  Direction = (0,0,-1)
  Length = 5
  Length2 = 5
  Midplane = true
  Profile = -> Sketch107
  ReferenceAxis = -> Sketch107 [N_Axis]
  Type = 1
  expr: Label = <<Pocket_Remove_>> + <<Boards>>.Label + <<_>> + <<SolderedPads>>.Label + <<_TPDebug_PicoH>>
FEATURE [PartDesign::Pad] Pad103  label="Pad_Boards_SolderedPads_TPDebug_PicoWH"
  BaseFeature = -> Pocket041
  Direction = (0,0,1)
  Length = 0.5
  Length2 = 10
  Profile = -> Clone2D023
  ReferenceAxis = -> Clone2D023 [N_Axis]
  Type = 0
  expr: Label = <<Pad_>> + <<Boards>>.Label + <<_>> + <<SolderedPads>>.Label + <<_TPDebug_PicoWH>>
  expr: Length = <<vPico>>.BoardThickness / 2
FEATURE [PartDesign::LinearPattern] LinearPattern074  label="LinearPattern_Boards_SolderedPads_TPDebug_PicoWH"
  BaseFeature = -> Pad103
  Direction = -> X_Axis086
  Length = 5.08
  Occurrences = 3
  Originals = -> [Pad103]
  expr: Label = <<LinearPattern_>> + <<Boards>>.Label + <<_>> + <<SolderedPads>>.Label + <<_TPDebug_PicoWH>>
  expr: Length = <<vPico>>.PinPitch * (Occurrences - 1)
FEATURE [PartDesign::Body] Body020  label="Boards_SolderedPads"
  Group = -> [DatumPoint009,Sketch099,Pad094,MultiTransform029,Mirrored051,Mirrored052,Sketch108,Pocket043,Sketch102,Pad097,Mirrored055,Sketch100,Pad095,LinearPattern068,LinearPattern070,LinearPattern071,Mirrored053,MultiTransform030,Sketch101,Pad096,LinearPattern069,Mirrored054,MultiTransform031,Local_CS,Sketch103,Pad099,Mirrored056,Clone2D020,Pad100,Clone2D021,Pad101,LinearPattern072,Clone2D022,Pad102,+8 more]
  Origin = -> Origin086
  Tip = -> LinearPattern074
  expr: Label = <<Boards>>.Label + <<_>> + <<SolderedPads>>.Label
FEATURE [App::Link] Link234  label="Tool_Boards_Substrate_PicoW"
  LinkedObject = -> LinearPattern080
  expr: Label = <<Tool_>> + <<Boards>>.Label + <<_>> + <<Substrate>>.Label + <<_PicoW>>
FEATURE [App::DocumentObjectGroup] Group047  label="Intermediary Construction Elements"
  Group = -> [Link211,Link209,Link234,Compound020,Compound021,Link220,Link221,Link222,Link224,Link225,Link223]
FEATURE [Sketcher::SketchObject] Sketch110
  AttachmentOffset = pos=(0,-25.5,0) rot=(0,0,1;0rad)
  FullyConstrained = true
  MapMode = 5
  Placement = pos=(0,-25.5,0) rot=(0,0,1;0rad)
  Support = -> [XY_Plane085]
  expr: .AttachmentOffset.Base.y = -<<vPico>>.BoardLength / 2
  expr: Constraints[8] = (<<vPico>>.PinInset + <<vPico>>.PinPadWidth) * 2
  expr: Constraints[9] = <<vPico>>.PinPitch * 3 + <<vPico>>.PinPadWidth
  sketch-geometry (4):
    g0: LineSegment StartX=-4.61 StartY=3.21 StartZ=0 EndX=4.61 EndY=3.21 EndZ=0
    g1: LineSegment StartX=4.61 StartY=3.21 StartZ=0 EndX=4.61 EndY=-3.21 EndZ=0
    g2: LineSegment StartX=4.61 StartY=-3.21 StartZ=0 EndX=-4.61 EndY=-3.21 EndZ=0
    g3: LineSegment StartX=-4.61 StartY=-3.21 StartZ=0 EndX=-4.61 EndY=3.21 EndZ=0
  constraints (10):
    c: Coincident(g0,g1)
    c: Coincident(g1,g2)
    c: Coincident(g2,g3)
    c: Coincident(g3,g0)
    c: Symmetric(g0,g0,g-2)
    c: Symmetric(g0,g1,g-1)
    c: Parallel(g3,g1)
    c: Parallel(g0,g2)
    c: Distance(g3) = 6.42
    c: Distance(g2) = 9.22
FEATURE [PartDesign::Pocket] Pocket047  label="Pocket_Remove_Boards_GoldPads_Debug_Pico"
  BaseFeature = -> Pocket039
  Direction = (0,0,-1)
  Length = 5
  Length2 = 5
  Midplane = true
  Profile = -> Sketch110
  ReferenceAxis = -> Sketch110 [N_Axis]
  Type = 1
  expr: Label = <<Pocket_Remove_>> + <<Boards>>.Label + <<_>> + <<GoldPads>>.Label + <<_Debug_Pico>>
FEATURE [PartDesign::Pad] Pad110  label="Pad_Boards_GoldPads_PicoWDebug_Round"
  BaseFeature = -> Pocket047
  Direction = (0,0,1)
  Length = 1
  Length2 = 10
  Profile = -> Clone2D029
  ReferenceAxis = -> Clone2D029 [N_Axis]
  Type = 0
  expr: Label = <<Pad_>> + <<Boards>>.Label + <<_>> + <<GoldPads>>.Label + <<_PicoWDebug_Round>>
  expr: Length = <<vPico>>.BoardThickness
FEATURE [PartDesign::LinearPattern] LinearPattern079  label="LinearPattern_Boards_GoldPads_PicoWDebug_Round"
  BaseFeature = -> Pad110
  Direction = -> X_Axis085
  Length = 2.54
  Occurrences = 2
  Originals = -> [Pad110]
  expr: Label = <<LinearPattern_>> + <<Boards>>.Label + <<_>> + <<GoldPads>>.Label + <<_PicoWDebug_Round>>
  expr: Length = <<vPico>>.PinPitch * (Occurrences - 1)
FEATURE [PartDesign::Pad] Pad111  label="Pad_Boards_GoldPads_PicoWDebug_Square"
  BaseFeature = -> LinearPattern079
  Direction = (0,0,1)
  Length = 1
  Length2 = 10
  Profile = -> Clone2D030
  ReferenceAxis = -> Clone2D030 [N_Axis]
  Type = 0
  expr: Label = <<Pad_>> + <<Boards>>.Label + <<_>> + <<GoldPads>>.Label + <<_PicoWDebug_Square>>
  expr: Length = <<vPico>>.BoardThickness
FEATURE [PartDesign::Body] Body019  label="Boards_GoldPads"
  Group = -> [DatumPoint008,Clone2D019,Pad098,MultiTransform027,Sketch096,Mirrored048,Mirrored049,Clone2D032,Pocket044,Sketch106,Pad112,Mirrored060,Pocket040,Mirrored061,Pad093,MultiTransform028,LinearPattern067,Mirrored050,Clone2D024,LinearPattern076,LinearPattern077,Sketch104,Pad107,MultiTransform032,LinearPattern078,Mirrored058,Local_CS001,Pad104,Mirrored057,Clone2D025,Pad105,Clone2D026,Pad106,+15 more]
  Origin = -> Origin085
  Tip = -> Pad111
  expr: Label = <<Boards>>.Label + <<_>> + <<GoldPads>>.Label
FEATURE [App::DocumentObjectGroup] Group046  label="Parametric Board Colour Sources"
  Group = -> [Body015,Body016,Body020,Body019]
FEATURE [App::Link] Link235  label="Tool_Boards_Substrate_PicoW001"
  LinkedObject = -> Link234
FEATURE [Part::Cut] Cut003  label="Tool_Board_PicoW_NoPads"
  Base = -> Link235
  Tool = -> Link217
FEATURE [Part::MultiFuse] Fusion002  label="Pico_W_Board"
  Shapes = -> [Cut003,Link228,Link231,Link232]
FEATURE [App::Part] Part020  label="Boards_Source"
  Group = -> [Spreadsheet001,Spreadsheet005,Spreadsheet004,Spreadsheet006,Group016,Body019,Body020,Body015,Body016,Group046,Link205,Link207,Link209,Link206,Link208,Link211,Link220,Compound021,Compound020,Link221,Link223,Link224,Link222,Link225,Group047,Link213,Link212,Cut001,Link226,Link230,Fusion,Link214,Link215,Cut002,Link227,Fusion001,Link234,Link235,Link217,Cut003,Link228,Link231,Link232,Fusion002,Link219,+5 more]
  License = MIT-0 (Public-domain-equivalent)
  LicenseURL = https://spdx.org/licenses/MIT-0.html
  Origin = -> Origin030
  expr: Label = <<Boards>>.Label + <<_Source>>
FEATURE [Sketcher::SketchObject] Sketch111  label="Sketch_D1_Lead"
  FullyConstrained = true
  MapMode = 5
  Placement = pos=(0,0,0) rot=(0.57735,0.57735,0.57735;2.0944rad)
  Support = -> [YZ_Plane087]
  expr: Constraints[17] = <<vPico>>.D1LeadSize.z
  expr: Constraints[18] = <<vPico>>.D1LeadSize.y
  expr: Constraints[20] = <<vPico>>.D1LeadOffset.y
  expr: Label = <<Sketch_>> + <<D1>> + <<_Lead>>
  sketch-geometry (8):
    g0: LineSegment StartX=-1.8 StartY=0 StartZ=0 EndX=-1.35 EndY=0 EndZ=0
    g1: LineSegment StartX=-1.8 StartY=0 StartZ=0 EndX=-1.8 EndY=0.15 EndZ=0
    g2: LineSegment StartX=-1.8 StartY=0.15 StartZ=0 EndX=0 EndY=0.15 EndZ=0
    g3: LineSegment StartX=0 StartY=0.075 StartZ=0 EndX=-1.35 EndY=0.075 EndZ=0
    g4: LineSegment StartX=-1.35 StartY=0.075 StartZ=0 EndX=-1.35 EndY=0 EndZ=0
    g5: LineSegment StartX=0 StartY=0.15 StartZ=0 EndX=0 EndY=0.075 EndZ=0
    g6: LineSegment StartX=-1.35 StartY=0.075 StartZ=0 EndX=-1.35 EndY=0.15 EndZ=0
    g7: GeomPoint X=-1.575 Y=0 Z=0
  constraints (22):
    c: PointOnObject(g0,g-1)
    c: PointOnObject(g0,g-1)
    c: Coincident(g1,g0)
    c: Coincident(g2,g1)
    c: Perpendicular(g0,g1)
    c: Coincident(g4,g3)
    c: Coincident(g4,g0)
    c: Perpendicular(g0,g4)
    c: PointOnObject(g3,g-2)
    c: PointOnObject(g2,g-2)
    c: Coincident(g5,g2)
    c: Coincident(g5,g3)
    c: Parallel(g3,g0)
    c: Coincident(g6,g3)
    c: PointOnObject(g6,g2)
    c: PointOnObject(g6,g4)
    c: Equal(g6,g4)
    c: Distance(g1) = 0.15
    c: Distance(g0) = 0.45
    c: Symmetric(g0,g0,g7)
    c: Distance(g7,g-2) = 1.575
    c: Parallel(g2,g0)
FEATURE [PartDesign::Pad] Pad114  label="Pad_D1_Lead"
  Direction = (1,-2e-16,3e-16)
  Length = 0.9
  Length2 = 10
  Midplane = true
  Placement = pos=(0,0,0) rot=(0.57735,0.57735,0.57735;2.0944rad)
  Profile = -> Sketch111
  ReferenceAxis = -> Sketch111 [N_Axis]
  Type = 0
  expr: Label = <<Pad_>> + <<D1>>.Label + <<_Lead>>
  expr: Length = <<vPico>>.D1LeadSize.x
FEATURE [PartDesign::Mirrored] Mirrored062  label="Mirror_D1_Lead"
  BaseFeature = -> Pad114
  MirrorPlane = -> XZ_Plane087
  Originals = -> [Pad114]
  Placement = pos=(0,0,0) rot=(0.57735,0.57735,0.57735;2.0944rad)
  expr: Label = <<Mirror_>> + <<D1>>.Label + <<_Lead>>
FEATURE [PartDesign::Body] Body021  label="Leads_D1"
  Group = -> [Sketch111,Pad114,Mirrored062]
  Origin = -> Origin087
  Tip = -> Mirrored062
  expr: Label = <<Leads_>> + <<D1>>.Label
FEATURE [Part::MultiFuse] Fusion004  label="D1_Fusion"
  Shapes = -> [Body011,Body021]
  expr: Label = <<D1>>.Label + <<_Fusion>>
FEATURE [Part::Compound] Compound007  label="D1_MBR120VLSFT1G"
  Links = -> [Group008,Fusion004]
  Placement = pos=(6,18.9,0) rot=(0,0,1;0rad)
  expr: Label = <<D1>>.Label + <<_>> + <<D1>>.Metadata_PartName
  expr: Placement = <<D1>>.Metadata_Placement
FEATURE [App::Part] Part003  label="Pico_Components_Source"
  Group = -> [Box004,Group005,Compound006,Group038,Box025,Compound008,Group039,Box026,Compound009,Body011,Group008,Compound007,Part013,Body005,Group014,Compound,Thickness,Box016,Group015,Compound010,Box010,Group011,Compound011,Box006,Group007,Compound012,Box014,Group013,Compound013,Body004,Group010,Compound014,Box,Group001,Compound015,Box001,Group002,Compound016,Group025,Box017,Compound017,Box002,Group003,+6 more]
  License = MIT-0 (Public-domain-equivalent)
  LicenseURL = https://spdx.org/licenses/MIT-0.html
  Origin = -> Origin010
  Placement = pos=(0,0,1) rot=(0,0,1;0rad)
  expr: .Placement.Base.z = <<vPico>>.BoardThickness
FEATURE [App::Link] Link238  label="SIP-20_Socket_Left001"
  LinkTransform = true
  LinkedObject = -> Part048 [Link.]
FEATURE [App::Link] Link239  label="SIP-20_Socket_Right001"
  LinkTransform = true
  LinkedObject = -> Part048 [Link491.]
FEATURE [Part::Compound] Compound022  label="DIP-40_W17.78mm_H8.51mm_Socket_Compound"
  Links = -> [Link238,Link239]
FEATURE [App::Link] Link240  label="Pico_Board_Link001"
  LinkTransform = true
  LinkedObject = -> Part024 [Link097.]
FEATURE [App::Link] Link241  label="Pico_C1_47u001"
  LinkTransform = true
  LinkedObject = -> Part024 [Part030.Link096.]
FEATURE [App::Link] Link242  label="Pico_C2_47u001"
  LinkTransform = true
  LinkedObject = -> Part024 [Part030.Link098.]
FEATURE [App::Link] Link243  label="Pico_D1_MBR120VLSFT1G001"
  LinkTransform = true
  LinkedObject = -> Part024 [Part030.Link100.]
FEATURE [App::Link] Link244  label="D2_QSME-C194_Base001"
  LinkTransform = true
  LinkedObject = -> Part024 [Part030.Link101.Body010.]
FEATURE [App::Link] Link246  label="D2_QSME-C194_Phosphor001"
  LinkTransform = true
  LinkedObject = -> Part024 [Part030.Link101.Link092.]
FEATURE [App::Link] Link247  label="Pico_J1_690T505-x62-01x001"
  LinkTransform = true
  LinkedObject = -> Part024 [Part030.Link102.]
FEATURE [App::Link] Link248  label="Pico_L1_2u003"
  LinkTransform = true
  LinkedObject = -> Part024 [Part030.Link104.]
FEATURE [App::Link] Link249  label="Pico_Q1_DMG1012T001"
  LinkTransform = true
  LinkedObject = -> Part024 [Part030.Link105.]
FEATURE [App::Link] Link250  label="Pico_SW1_TP-1221U-K9K5326"
  LinkTransform = true
  LinkedObject = -> Part024 [Part030.Link107.]
FEATURE [App::Link] Link251  label="Pico_U1_RP2041"
  LinkTransform = true
  LinkedObject = -> Part024 [Part030.Link108.]
FEATURE [App::Link] Link252  label="Pico_U2_RT6150B-33GQW001"
  LinkTransform = true
  LinkedObject = -> Part024 [Part030.Link109.]
FEATURE [App::Link] Link253  label="Pico_U3_W25Q16JVUXIQ001"
  LinkTransform = true
  LinkedObject = -> Part024 [Part030.Link111.]
FEATURE [App::Link] Link254  label="Pico_X1_X12M000000S097"
  LinkTransform = true
  LinkedObject = -> Part024 [Part030.Link112.]
FEATURE [App::Link] Link245  label="D2_QSME-C194_Lens001"
  LinkTransform = true
  LinkedObject = -> Part024 [Part030.Link101.Box024.]
FEATURE [Part::Compound] Compound023  label="RaspberryPi_Pico_Compound"
  Links = -> [Link240,Link241,Link242,Link243,Link244,Link245,Link246,Link247,Link248,Link249,Link250,Link251,Link252,Link253,Link254]
FEATURE [App::Link] Link255  label="Pico_H_DIP-40_W17.78mm_Header001"
  LinkTransform = true
  LinkedObject = -> Part049 [Link487.]
FEATURE [App::Link] Link256  label="Pico_H_Board_Link001"
  LinkTransform = true
  LinkedObject = -> Part049 [Part051.Link115.]
FEATURE [App::Link] Link257  label="Pico_H_C1_47u001"
  LinkTransform = true
  LinkedObject = -> Part049 [Part051.Part050.Link114.]
FEATURE [App::Link] Link258  label="Pico_H_C2_47u001"
  LinkTransform = true
  LinkedObject = -> Part049 [Part051.Part050.Link116.]
FEATURE [App::Link] Link259  label="Pico_H_D1_MBR120VLSFT1G001"
  LinkTransform = true
  LinkedObject = -> Part049 [Part051.Part050.Link118.]
FEATURE [App::Link] Link260  label="D2_QSME-C194_Base002"
  LinkTransform = true
  LinkedObject = -> Part049 [Part051.Part050.Link119.Body010.]
FEATURE [App::Link] Link261  label="D2_QSME-C194_Lens002"
  LinkTransform = true
  LinkedObject = -> Part049 [Part051.Part050.Link119.Box024.]
FEATURE [App::Link] Link262  label="D2_QSME-C194_Phosphor_Link001"
  LinkTransform = true
  LinkedObject = -> Part049 [Part051.Part050.Link119.Link092.]
FEATURE [App::Link] Link263  label="Pico_H_J1_690T505-x62-01x001"
  LinkTransform = true
  LinkedObject = -> Part049 [Part051.Part050.Link120.]
FEATURE [App::Link] Link264  label="Pico_H_J2_BM03B-SRSS-TB001"
  LinkTransform = true
  LinkedObject = -> Part049 [Part051.Part050.Link121.]
FEATURE [App::Link] Link265  label="Pico_H_L1_2u003"
  LinkTransform = true
  LinkedObject = -> Part049 [Part051.Part050.Link122.]
FEATURE [App::Link] Link266  label="Pico_H_Q1_DMG1012T001"
  LinkTransform = true
  LinkedObject = -> Part049 [Part051.Part050.Link123.]
FEATURE [App::Link] Link267  label="Pico_H_SW1_TP-1221U-K9K5326"
  LinkTransform = true
  LinkedObject = -> Part049 [Part051.Part050.Link125.]
FEATURE [App::Link] Link268  label="Pico_H_U1_RP2041"
  LinkTransform = true
  LinkedObject = -> Part049 [Part051.Part050.Link126.]
FEATURE [App::Link] Link269  label="Pico_H_U2_RT6150B-33GQW001"
  LinkTransform = true
  LinkedObject = -> Part049 [Part051.Part050.Link127.]
FEATURE [App::Link] Link270  label="Pico_H_U3_W25Q16JVUXIQ001"
  LinkTransform = true
  LinkedObject = -> Part049 [Part051.Part050.Link129.]
FEATURE [App::Link] Link271  label="Pico_H_X1_X12M000000S097"
  LinkTransform = true
  LinkedObject = -> Part049 [Part051.Part050.Link130.]
FEATURE [Part::Compound] Compound024  label="RaspberryPi_Pico_H_Compound"
  Links = -> [Link255,Link256,Link257,Link258,Link259,Link260,Link261,Link262,Link263,Link264,Link265,Link266,Link267,Link268,Link269,Link270,Link271]
FEATURE [App::Link] Link272  label="Pico_H_Socketed_DIP-40_W17.78mm_Header001"
  LinkTransform = true
  LinkedObject = -> Part052 [Link488.]
FEATURE [App::Link] Link273  label="Pico_H_Socketed_Board_Link001"
  LinkTransform = true
  LinkedObject = -> Part052 [Part054.Link133.]
FEATURE [App::Link] Link274  label="Pico_H_Socketed_C1_47u001"
  LinkTransform = true
  LinkedObject = -> Part052 [Part054.Part053.Link132.]
FEATURE [App::Link] Link275  label="Pico_H_Socketed_C2_47u001"
  LinkTransform = true
  LinkedObject = -> Part052 [Part054.Part053.Link134.]
FEATURE [App::Link] Link276  label="Pico_H_Socketed_D1_MBR120VLSFT1G001"
  LinkTransform = true
  LinkedObject = -> Part052 [Part054.Part053.Link136.]
FEATURE [App::Link] Link277  label="D2_QSME-C194_Base003"
  LinkTransform = true
  LinkedObject = -> Part052 [Part054.Part053.Link137.Body010.]
FEATURE [App::Link] Link278  label="D2_QSME-C194_Lens003"
  LinkTransform = true
  LinkedObject = -> Part052 [Part054.Part053.Link137.Box024.]
FEATURE [App::Link] Link279  label="D2_QSME-C194_Phosphor_Link002"
  LinkTransform = true
  LinkedObject = -> Part052 [Part054.Part053.Link137.Link092.]
FEATURE [App::Link] Link280  label="Pico_H_Socketed_J1_690T505-x62-01x001"
  LinkTransform = true
  LinkedObject = -> Part052 [Part054.Part053.Link138.]
FEATURE [App::Link] Link281  label="Pico_H_Socketed_J2_BM03B-SRSS-TB001"
  LinkTransform = true
  LinkedObject = -> Part052 [Part054.Part053.Link139.]
FEATURE [App::Link] Link282  label="Pico_H_Socketed_L1_2u003"
  LinkTransform = true
  LinkedObject = -> Part052 [Part054.Part053.Link140.]
FEATURE [App::Link] Link283  label="Pico_H_Socketed_Q1_DMG1012T001"
  LinkTransform = true
  LinkedObject = -> Part052 [Part054.Part053.Link141.]
FEATURE [App::Link] Link284  label="Pico_H_Socketed_SW1_TP-1221U-K9K5326"
  LinkTransform = true
  LinkedObject = -> Part052 [Part054.Part053.Link143.]
FEATURE [App::Link] Link285  label="Pico_H_Socketed_U1_RP2041"
  LinkTransform = true
  LinkedObject = -> Part052 [Part054.Part053.Link144.]
FEATURE [App::Link] Link286  label="Pico_H_Socketed_U2_RT6150B-33GQW001"
  LinkTransform = true
  LinkedObject = -> Part052 [Part054.Part053.Link145.]
FEATURE [App::Link] Link287  label="Pico_H_Socketed_U3_W25Q16JVUXIQ001"
  LinkTransform = true
  LinkedObject = -> Part052 [Part054.Part053.Link147.]
FEATURE [App::Link] Link288  label="Pico_H_Socketed_X1_X12M000000S097"
  LinkTransform = true
  LinkedObject = -> Part052 [Part054.Part053.Link148.]
FEATURE [Part::Compound] Compound025  label="RaspberryPi_Pico_H_Socketed_Compound"
  Links = -> [Link272,Link273,Link274,Link275,Link276,Link277,Link278,Link279,Link280,Link281,Link282,Link283,Link284,Link285,Link286,Link287,Link288]
FEATURE [App::Link] Link289  label="Pico_W_Board_Link001"
  LinkTransform = true
  LinkedObject = -> Part055 [Link151.]
FEATURE [App::Link] Link290  label="Pico_W_C1_47u001"
  LinkTransform = true
  LinkedObject = -> Part055 [Part056.Link150.]
FEATURE [App::Link] Link291  label="Pico_W_C2_47u001"
  LinkTransform = true
  LinkedObject = -> Part055 [Part056.Link152.]
FEATURE [App::Link] Link292  label="Pico_W_C21_47u001"
  LinkTransform = true
  LinkedObject = -> Part055 [Part056.Link153.]
FEATURE [App::Link] Link293  label="Pico_W_D1_MBR120VLSFT1G001"
  LinkTransform = true
  LinkedObject = -> Part055 [Part056.Link154.]
FEATURE [App::Link] Link294  label="D2_QSME-C194_Base004"
  LinkTransform = true
  LinkedObject = -> Part055 [Part056.Link155.Body010.]
FEATURE [App::Link] Link295  label="D2_QSME-C194_Lens004"
  LinkTransform = true
  LinkedObject = -> Part055 [Part056.Link155.Box024.]
FEATURE [App::Link] Link296  label="D2_QSME-C194_Phosphor_Link003"
  LinkTransform = true
  LinkedObject = -> Part055 [Part056.Link155.Link092.]
FEATURE [App::Link] Link297  label="Pico_W_J1_690T505-x62-01x001"
  LinkTransform = true
  LinkedObject = -> Part055 [Part056.Link156.]
FEATURE [App::Link] Link298  label="Pico_W_L1_2u003"
  LinkTransform = true
  LinkedObject = -> Part055 [Part056.Link158.]
FEATURE [App::Link] Link299  label="Pico_W_Q1_DMG1012T001"
  LinkTransform = true
  LinkedObject = -> Part055 [Part056.Link159.]
FEATURE [App::Link] Link300  label="Pico_W_SH1_CYW43440"
  LinkTransform = true
  LinkedObject = -> Part055 [Part056.Link160.]
FEATURE [App::Link] Link301  label="Pico_W_SW1_TP-1221U-K9K5326"
  LinkTransform = true
  LinkedObject = -> Part055 [Part056.Link161.]
FEATURE [App::Link] Link302  label="Pico_W_U1_RP2041"
  LinkTransform = true
  LinkedObject = -> Part055 [Part056.Link162.]
FEATURE [App::Link] Link303  label="Pico_W_U2_RT6154AGQW001"
  LinkTransform = true
  LinkedObject = -> Part055 [Part056.Link164.]
FEATURE [App::Link] Link304  label="Pico_W_U3_W25Q16JVUXIQ001"
  LinkTransform = true
  LinkedObject = -> Part055 [Part056.Link165.]
FEATURE [App::Link] Link305  label="Pico_W_X1_X12M000000S097"
  LinkTransform = true
  LinkedObject = -> Part055 [Part056.Link166.]
FEATURE [Part::Compound] Compound026  label="RaspberryPi_Pico_W_Compound"
  Links = -> [Link289,Link290,Link291,Link292,Link293,Link294,Link295,Link296,Link297,Link298,Link299,Link300,Link301,Link302,Link303,Link304,Link305]
FEATURE [App::Link] Link306  label="Pico_WH_DIP-40_W17.78mm_Header001"
  LinkTransform = true
  LinkedObject = -> Part057 [Link489.]
FEATURE [App::Link] Link307  label="Pico_WH_Board_Link001"
  LinkTransform = true
  LinkedObject = -> Part057 [Part059.Link168.]
FEATURE [App::Link] Link308  label="Pico_WH_C1_47u001"
  LinkTransform = true
  LinkedObject = -> Part057 [Part059.Part058.Link167.]
FEATURE [App::Link] Link309  label="Pico_WH_C2_47u001"
  LinkTransform = true
  LinkedObject = -> Part057 [Part059.Part058.Link169.]
FEATURE [App::Link] Link310  label="Pico_WH_C21_47u001"
  LinkTransform = true
  LinkedObject = -> Part057 [Part059.Part058.Link170.]
FEATURE [App::Link] Link311  label="Pico_WH_D1_MBR120VLSFT1G001"
  LinkTransform = true
  LinkedObject = -> Part057 [Part059.Part058.Link171.]
FEATURE [App::Link] Link312  label="D2_QSME-C194_Base005"
  LinkTransform = true
  LinkedObject = -> Part057 [Part059.Part058.Link172.Body010.]
FEATURE [App::Link] Link313  label="D2_QSME-C194_Lens005"
  LinkTransform = true
  LinkedObject = -> Part057 [Part059.Part058.Link172.Box024.]
FEATURE [App::Link] Link314  label="D2_QSME-C194_Phosphor_Link004"
  LinkTransform = true
  LinkedObject = -> Part057 [Part059.Part058.Link172.Link092.]
FEATURE [App::Link] Link315  label="Pico_WH_J1_690T505-x62-01x001"
  LinkTransform = true
  LinkedObject = -> Part057 [Part059.Part058.Link173.]
FEATURE [App::Link] Link316  label="Pico_WH_J2_BM03B-SRSS-TB001"
  LinkTransform = true
  LinkedObject = -> Part057 [Part059.Part058.Link174.]
FEATURE [App::Link] Link317  label="Pico_WH_L1_2u003"
  LinkTransform = true
  LinkedObject = -> Part057 [Part059.Part058.Link175.]
FEATURE [App::Link] Link318  label="Pico_WH_Q1_DMG1012T001"
  LinkTransform = true
  LinkedObject = -> Part057 [Part059.Part058.Link176.]
FEATURE [App::Link] Link319  label="Pico_WH_SH1_CYW43440"
  LinkTransform = true
  LinkedObject = -> Part057 [Part059.Part058.Link177.]
FEATURE [App::Link] Link320  label="Pico_WH_SW1_TP-1221U-K9K5326"
  LinkTransform = true
  LinkedObject = -> Part057 [Part059.Part058.Link178.]
FEATURE [App::Link] Link321  label="Pico_WH_U1_RP2041"
  LinkTransform = true
  LinkedObject = -> Part057 [Part059.Part058.Link179.]
FEATURE [App::Link] Link322  label="Pico_WH_U2_RT6154AGQW001"
  LinkTransform = true
  LinkedObject = -> Part057 [Part059.Part058.Link181.]
FEATURE [App::Link] Link323  label="Pico_WH_U3_W25Q16JVUXIQ001"
  LinkTransform = true
  LinkedObject = -> Part057 [Part059.Part058.Link182.]
FEATURE [App::Link] Link324  label="Pico_WH_X1_X12M000000S097"
  LinkTransform = true
  LinkedObject = -> Part057 [Part059.Part058.Link183.]
FEATURE [Part::Compound] Compound027  label="RaspberryPi_Pico_WH_Compound"
  Links = -> [Link306,Link307,Link308,Link309,Link310,Link311,Link312,Link313,Link314,Link315,Link316,Link317,Link318,Link319,Link320,Link321,Link322,Link323,Link324]
FEATURE [App::Link] Link325  label="Pico_WH_Socketed_DIP-40_W17.78mm_Header001"
  LinkTransform = true
  LinkedObject = -> Part060 [Link490.]
FEATURE [App::Link] Link326  label="Pico_WH_Socketed_Board_Link001"
  LinkTransform = true
  LinkedObject = -> Part060 [Part062.Link186.]
FEATURE [App::Link] Link327  label="Pico_WH_Socketed_C1_47u001"
  LinkTransform = true
  LinkedObject = -> Part060 [Part062.Part061.Link185.]
FEATURE [App::Link] Link328  label="Pico_WH_Socketed_C2_47u001"
  LinkTransform = true
  LinkedObject = -> Part060 [Part062.Part061.Link187.]
FEATURE [App::Link] Link329  label="Pico_WH_Socketed_C21_47u001"
  LinkTransform = true
  LinkedObject = -> Part060 [Part062.Part061.Link188.]
FEATURE [App::Link] Link330  label="Pico_WH_Socketed_D1_MBR120VLSFT1G001"
  LinkTransform = true
  LinkedObject = -> Part060 [Part062.Part061.Link189.]
FEATURE [App::Link] Link331  label="D2_QSME-C194_Base006"
  LinkTransform = true
  LinkedObject = -> Part060 [Part062.Part061.Link190.Body010.]
FEATURE [App::Link] Link332  label="D2_QSME-C194_Lens006"
  LinkTransform = true
  LinkedObject = -> Part060 [Part062.Part061.Link190.Box024.]
FEATURE [App::Link] Link333  label="D2_QSME-C194_Phosphor_Link005"
  LinkTransform = true
  LinkedObject = -> Part060 [Part062.Part061.Link190.Link092.]
FEATURE [App::Link] Link334  label="Pico_WH_Socketed_J1_690T505-x62-01x001"
  LinkTransform = true
  LinkedObject = -> Part060 [Part062.Part061.Link191.]
FEATURE [App::Link] Link335  label="Pico_WH_Socketed_J2_BM03B-SRSS-TB001"
  LinkTransform = true
  LinkedObject = -> Part060 [Part062.Part061.Link192.]
FEATURE [App::Link] Link336  label="Pico_WH_Socketed_L1_2u003"
  LinkTransform = true
  LinkedObject = -> Part060 [Part062.Part061.Link193.]
FEATURE [App::Link] Link337  label="Pico_WH_Socketed_Q1_DMG1012T001"
  LinkTransform = true
  LinkedObject = -> Part060 [Part062.Part061.Link194.]
FEATURE [App::Link] Link338  label="Pico_WH_Socketed_SH1_CYW43440"
  LinkTransform = true
  LinkedObject = -> Part060 [Part062.Part061.Link195.]
FEATURE [App::Link] Link339  label="Pico_WH_Socketed_SW1_TP-1221U-K9K5326"
  LinkTransform = true
  LinkedObject = -> Part060 [Part062.Part061.Link196.]
FEATURE [App::Link] Link340  label="Pico_WH_Socketed_U1_RP2041"
  LinkTransform = true
  LinkedObject = -> Part060 [Part062.Part061.Link197.]
FEATURE [App::Link] Link341  label="Pico_WH_Socketed_U2_RT6154AGQW001"
  LinkTransform = true
  LinkedObject = -> Part060 [Part062.Part061.Link199.]
FEATURE [App::Link] Link342  label="Pico_WH_Socketed_U3_W25Q16JVUXIQ001"
  LinkTransform = true
  LinkedObject = -> Part060 [Part062.Part061.Link200.]
FEATURE [App::Link] Link343  label="Pico_WH_Socketed_X1_X12M000000S097"
  LinkTransform = true
  LinkedObject = -> Part060 [Part062.Part061.Link201.]
FEATURE [Part::Compound] Compound028  label="RaspberryPi_Pico_WH_Socketed_Compound"
  Links = -> [Link325,Link326,Link327,Link328,Link329,Link330,Link331,Link332,Link333,Link334,Link335,Link336,Link337,Link338,Link339,Link340,Link341,Link342,Link343]
FEATURE [Spreadsheet::Sheet] Spreadsheet  label="vHeaderBreakaway"
  cells = A1='Corner Size; B1(CornerSize)=0.254; D1='Part Name; E1(PartName)='Header_Breakaway; D2='Breakaway Body Name; E2(BreakawayBodyName)='Body; D3='Pin Body Name; E3(PinBodyName)='Pin
FEATURE [Sketcher::SketchObject] Sketch116  label="Sketch_Header_Breakaway_Body_Segment"
  AttachmentOffset = pos=(-8.89,24.13,0) rot=(0,0,1;0rad)
  FullyConstrained = true
  MapMode = 5
  Placement = pos=(-8.89,24.13,0) rot=(0,0,1;0rad)
  Support = -> [XY_Plane091]
  expr: .AttachmentOffset.Base.x = -(<<vPico>>.BoardWidth / 2 - <<vPico>>.PinInset)
  expr: .AttachmentOffset.Base.y = (<<vPico>>.PinDIPCount / 4 - 0.5) * <<vPico>>.PinPitch
  expr: Constraints[9] = <<vHeader>>.InsulationWidth
  expr: Label = <<Sketch_>> + <<vHeaderBreakaway>>.PartName + <<_>> + <<vHeaderBreakaway>>.BreakawayBodyName + <<_Segment>>
  sketch-geometry (4):
    g0: LineSegment StartX=-1.27 StartY=1.27 StartZ=0 EndX=1.27 EndY=1.27 EndZ=0
    g1: LineSegment StartX=1.27 StartY=1.27 StartZ=0 EndX=1.27 EndY=-1.27 EndZ=0
    g2: LineSegment StartX=1.27 StartY=-1.27 StartZ=0 EndX=-1.27 EndY=-1.27 EndZ=0
    g3: LineSegment StartX=-1.27 StartY=-1.27 StartZ=0 EndX=-1.27 EndY=1.27 EndZ=0
  constraints (11):
    c: Coincident(g0,g1)
    c: Coincident(g1,g2)
    c: Coincident(g2,g3)
    c: Coincident(g3,g0)
    c: Vertical(g3)
    c: Parallel(g1,g3)
    c: Parallel(g0,g2)
    c: Perpendicular(g2,g3)
    c: Symmetric(g2,g0,g-1)
    c: Distance(g2) = 2.54
    c: Equal(g2,g3)
FEATURE [PartDesign::Pad] Pad119  label="Pad_Header_Breakaway_Body_Segment"
  Direction = (0,0,1)
  Length = 2.54
  Length2 = 10
  Profile = -> Sketch116
  ReferenceAxis = -> Sketch116 [N_Axis]
  Type = 0
  expr: Label = <<Pad_>> + <<vHeaderBreakaway>>.PartName + <<_>> + <<vHeaderBreakaway>>.BreakawayBodyName + <<_Segment>>
  expr: Length = <<vHeader>>.InsulationThickness
FEATURE [PartDesign::Chamfer] Chamfer  label="Chamfer_Header_Breakaway_Body_Segment"
  Angle = 45
  Base = -> Pad119 [Edge5,Edge2,Edge1,Edge8]
  BaseFeature = -> Pad119
  ChamferType = 0
  FlipDirection = false
  Size = 0.254
  Size2 = 1
  SupportTransform = false
  UseAllEdges = false
  expr: Label = <<Chamfer_>> + <<vHeaderBreakaway>>.PartName + <<_>> + <<vHeaderBreakaway>>.BreakawayBodyName + <<_Segment>>
  expr: Size = <<vHeaderBreakaway>>.CornerSize
FEATURE [PartDesign::LinearPattern] LinearPattern082  label="LinearPattern_Header_Breakaway_Body_Segments"
  BaseFeature = -> Chamfer
  Direction = -> Y_Axis091
  Length = 48.26
  Occurrences = 20
  Originals = -> [Pad119,Chamfer]
  Refine = true
  Reversed = true
  expr: Label = <<LinearPattern_>> + <<vHeaderBreakaway>>.PartName + <<_>> + <<vHeaderBreakaway>>.BreakawayBodyName + <<_Segments>>
  expr: Length = <<vPico>>.PinPitch * (Occurrences - 1)
  expr: Occurrences = <<vPico>>.PinDIPCount / 2
FEATURE [PartDesign::Body] Body024  label="Header_Breakaway_Body"
  Group = -> [Sketch116,Pad119,Chamfer,LinearPattern082]
  Origin = -> Origin091
  Tip = -> LinearPattern082
  expr: Label = <<vHeaderBreakaway>>.PartName + <<_>> + <<vHeaderBreakaway>>.BreakawayBodyName
FEATURE [Sketcher::SketchObject] Sketch118  label="Sketch_Header_Breakaway_Pin_Pin"
  AttachmentOffset = pos=(-8.89,24.13,0) rot=(0,0,1;0rad)
  FullyConstrained = true
  MapMode = 5
  Placement = pos=(-8.89,24.13,0) rot=(0,0,1;0rad)
  Support = -> [XY_Plane093]
  expr: .AttachmentOffset.Base.x = -(<<vPico>>.BoardWidth / 2 - <<vPico>>.PinInset)
  expr: .AttachmentOffset.Base.y = (<<vPico>>.PinDIPCount / 4 - 0.5) * <<vPico>>.PinPitch
  expr: Constraints[9] = <<vHeader>>.PinWidth
  expr: Label = <<Sketch_>> + <<vHeaderBreakaway>>.PartName + <<_>> + <<vHeaderBreakaway>>.PinBodyName + <<_Pin>>
  sketch-geometry (4):
    g0: LineSegment StartX=-0.3175 StartY=0.3175 StartZ=0 EndX=0.3175 EndY=0.3175 EndZ=0
    g1: LineSegment StartX=0.3175 StartY=0.3175 StartZ=0 EndX=0.3175 EndY=-0.3175 EndZ=0
    g2: LineSegment StartX=0.3175 StartY=-0.3175 StartZ=0 EndX=-0.3175 EndY=-0.3175 EndZ=0
    g3: LineSegment StartX=-0.3175 StartY=-0.3175 StartZ=0 EndX=-0.3175 EndY=0.3175 EndZ=0
  constraints (11):
    c: Coincident(g0,g1)
    c: Coincident(g1,g2)
    c: Coincident(g2,g3)
    c: Coincident(g3,g0)
    c: Vertical(g3)
    c: Parallel(g1,g3)
    c: Parallel(g0,g2)
    c: Perpendicular(g2,g3)
    c: Symmetric(g2,g0,g-1)
    c: Distance(g2) = 0.635
    c: Equal(g2,g3)
FEATURE [PartDesign::Pad] Pad121  label="Pad_Header_Breakaway_Pin"
  Direction = (0,0,1)
  Length = 4.175
  Length2 = 6.35
  Profile = -> Sketch118
  ReferenceAxis = -> Sketch118 [N_Axis]
  Type = 4
  expr: Label = <<Pad_>> + <<vHeaderBreakaway>>.PartName + <<_>> + <<vHeaderBreakaway>>.PinBodyName
  expr: Length = <<vHeader>>.PinLength - <<vHeader>>.PinInterfaceLength
  expr: Length2 = <<vHeader>>.PinInterfaceLength
FEATURE [PartDesign::Chamfer] Chamfer004  label="Chamfer_Header_Breakaway_Pin"
  Angle = 45
  Base = -> Pad121 [Face6,Face5]
  BaseFeature = -> Pad121
  ChamferType = 1
  FlipDirection = false
  Size = 0.15875
  Size2 = 0.635
  SupportTransform = false
  UseAllEdges = false
  expr: Label = <<Chamfer_>> + <<vHeaderBreakaway>>.PartName + <<_>> + <<vHeaderBreakaway>>.PinBodyName
  expr: Size = (<<vHeader>>.PinWidth - <<vHeader>>.PinBaseWidth) / 2
  expr: Size2 = <<vHeader>>.PinTipLength
FEATURE [PartDesign::Body] Body026  label="Header_Breakaway_Pin"
  Group = -> [Sketch118,Pad121,Chamfer004]
  Origin = -> Origin093
  Tip = -> Chamfer004
  expr: Label = <<vHeaderBreakaway>>.PartName + <<_>> + <<vHeaderBreakaway>>.PinBodyName
FEATURE [App::DocumentObjectGroup] Group049  label="Pico_AddedHeaders"
FEATURE [App::DocumentObjectGroup] Group050  label="Pico_AddedHeaders_Socketed"
FEATURE [App::DocumentObjectGroup] Group051  label="Pico_W_AddedHeaders"
FEATURE [App::DocumentObjectGroup] Group052  label="Pico_W_AddedHeaders_Socketed"
FEATURE [App::Link] Link344  label="Pico_AddedHeaders_C1_47u"
  LinkPlacement = pos=(2.9,17.1,0) rot=(0,0,1;0rad)
  LinkedObject = -> Compound006
  Placement = pos=(2.9,17.1,0) rot=(0,0,1;0rad)
  expr: Label = <<Pico_AddedHeaders>>.Label + <<_>> + .LinkedObject.Label
  expr: Placement = <<vPico>>.C1Placement
FEATURE [App::Link] Link345  label="Pico_AddedHeaders_Board_Link"
  LinkedObject = -> Fusion
  expr: Label = <<Pico_AddedHeaders>>.Label + <<_Board>> + <<_Link>>
FEATURE [App::Link] Link346  label="Pico_AddedHeaders_C2_47u"
  LinkPlacement = pos=(2.9,12.1,0) rot=(0,0,1;0rad)
  LinkedObject = -> Compound008
  Placement = pos=(2.9,12.1,0) rot=(0,0,1;0rad)
  expr: Label = <<Pico_AddedHeaders>>.Label + <<_>> + .LinkedObject.Label
  expr: Placement = <<vPico>>.C2Placement
FEATURE [App::Link] Link347  label="Pico_AddedHeaders_D1_MBR120VLSFT1G"
  LinkPlacement = pos=(6,18.9,0) rot=(0,0,1;0rad)
  LinkedObject = -> Compound007
  Placement = pos=(6,18.9,0) rot=(0,0,1;0rad)
  expr: Label = <<Pico_AddedHeaders>>.Label + <<_>> + .LinkedObject.Label
  expr: Placement = <<vPico>>.D1Placement
FEATURE [App::Link] Link348  label="Pico_AddedHeaders_D2_QSME-C194"
  LinkPlacement = pos=(-5.7,20.7,0) rot=(0,0,1;0rad)
  LinkedObject = -> Part013
  Placement = pos=(-5.7,20.7,0) rot=(0,0,1;0rad)
  expr: Label = <<Pico_AddedHeaders>>.Label + <<_>> + .LinkedObject.Label
  expr: Placement = <<vPico>>.D2Placement
FEATURE [App::Link] Link349  label="Pico_AddedHeaders_J1_690T505-x62-01x"
  LinkPlacement = pos=(0,23.7,0) rot=(0,0,1;0rad)
  LinkedObject = -> Compound
  Placement = pos=(0,23.7,0) rot=(0,0,1;0rad)
  expr: Label = <<Pico_AddedHeaders>>.Label + <<_>> + .LinkedObject.Label
  expr: Placement = <<vPico>>.J1Placement
FEATURE [App::Link] Link351  label="Pico_AddedHeaders_L1_2u2"
  LinkPlacement = pos=(6,14.6,0) rot=(0,0,1;0rad)
  LinkedObject = -> Compound011
  Placement = pos=(6,14.6,0) rot=(0,0,1;0rad)
  expr: Label = <<Pico_AddedHeaders>>.Label + <<_>> + .LinkedObject.Label
  expr: Placement = <<vPico>>.L1Placement
FEATURE [App::Link] Link352  label="Pico_AddedHeaders_Q1_DMG1012T"
  LinkPlacement = pos=(6.4,7.2,0) rot=(0,0,1;0rad)
  LinkedObject = -> Compound012
  Placement = pos=(6.4,7.2,0) rot=(0,0,1;0rad)
  expr: Label = <<Pico_AddedHeaders>>.Label + <<_>> + .LinkedObject.Label
  expr: Placement = <<vPico>>.Q1Placement
FEATURE [App::Link] Link353  label="Pico_AddedHeaders_SW1_TP-1221U-K9K5325"
  LinkPlacement = pos=(-3.5,13.5,0) rot=(0,0,1;0rad)
  LinkedObject = -> Compound014
  Placement = pos=(-3.5,13.5,0) rot=(0,0,1;0rad)
  expr: Label = <<Pico_AddedHeaders>>.Label + <<_>> + .LinkedObject.Label
  expr: Placement = <<vPico>>.SW1Placement
FEATURE [App::Link] Link354  label="Pico_AddedHeaders_U1_RP2040"
  LinkPlacement = pos=(0,-0.5,0) rot=(0,0,1;0rad)
  LinkedObject = -> Compound015
  Placement = pos=(0,-0.5,0) rot=(0,0,1;0rad)
  expr: Label = <<Pico_AddedHeaders>>.Label + <<_>> + .LinkedObject.Label
  expr: Placement = <<vPico>>.U1Placement
FEATURE [App::Link] Link355  label="Pico_AddedHeaders_U2_RT6150B-33GQW"
  LinkPlacement = pos=(2.9,14.6,0) rot=(0,0,1;3.14159rad)
  LinkedObject = -> Compound016
  Placement = pos=(2.9,14.6,0) rot=(0,0,1;3.14159rad)
  expr: Label = <<Pico_AddedHeaders>>.Label + <<_>> + .LinkedObject.Label
  expr: Placement = <<vPico>>.U2Placement
FEATURE [App::Link] Link356  label="Pico_AddedHeaders_U3_W25Q16JVUXIQ"
  LinkPlacement = pos=(-3.8,6.4,0) rot=(0,0,1;1.5708rad)
  LinkedObject = -> Compound018
  Placement = pos=(-3.8,6.4,0) rot=(0,0,1;1.5708rad)
  expr: Label = <<Pico_AddedHeaders>>.Label + <<_>> + .LinkedObject.Label
  expr: Placement = <<vPico>>.U3Placement
FEATURE [App::Link] Link357  label="Pico_AddedHeaders_X1_X12M000000S096"
  LinkPlacement = pos=(-2.3,-9.05,0) rot=(0,0,1;0rad)
  LinkedObject = -> Compound019
  Placement = pos=(-2.3,-9.05,0) rot=(0,0,1;0rad)
  expr: Label = <<Pico_AddedHeaders>>.Label + <<_>> + .LinkedObject.Label
  expr: Placement = <<vPico>>.X1Placement
FEATURE [App::Link] Link359  label="Pico_AddedHeaders_Socketed_C1_47u"
  LinkPlacement = pos=(2.9,17.1,0) rot=(0,0,1;0rad)
  LinkedObject = -> Compound006
  Placement = pos=(2.9,17.1,0) rot=(0,0,1;0rad)
  expr: Label = <<Pico_AddedHeaders_Socketed>>.Label + <<_>> + .LinkedObject.Label
  expr: Placement = <<vPico>>.C1Placement
FEATURE [App::Link] Link360  label="Pico_AddedHeaders_Socketed_Board_Link"
  LinkedObject = -> Part020 [Fusion.]
  expr: Label = <<Pico_AddedHeaders_Socketed>>.Label + <<_Board>> + <<_Link>>
FEATURE [App::Link] Link361  label="Pico_AddedHeaders_Socketed_C2_47u"
  LinkPlacement = pos=(2.9,12.1,0) rot=(0,0,1;0rad)
  LinkedObject = -> Compound008
  Placement = pos=(2.9,12.1,0) rot=(0,0,1;0rad)
  expr: Label = <<Pico_AddedHeaders_Socketed>>.Label + <<_>> + .LinkedObject.Label
  expr: Placement = <<vPico>>.C2Placement
FEATURE [App::Link] Link362  label="Pico_AddedHeaders_Socketed_D1_MBR120VLSFT1G"
  LinkPlacement = pos=(6,18.9,0) rot=(0,0,1;0rad)
  LinkedObject = -> Compound007
  Placement = pos=(6,18.9,0) rot=(0,0,1;0rad)
  expr: Label = <<Pico_AddedHeaders_Socketed>>.Label + <<_>> + .LinkedObject.Label
  expr: Placement = <<vPico>>.D1Placement
FEATURE [App::Link] Link363  label="Pico_AddedHeaders_Socketed_D2_QSME-C194"
  LinkPlacement = pos=(-5.7,20.7,0) rot=(0,0,1;0rad)
  LinkedObject = -> Part013
  Placement = pos=(-5.7,20.7,0) rot=(0,0,1;0rad)
  expr: Label = <<Pico_AddedHeaders_Socketed>>.Label + <<_>> + .LinkedObject.Label
  expr: Placement = <<vPico>>.D2Placement
FEATURE [App::Link] Link364  label="Pico_AddedHeaders_Socketed_J1_690T505-x62-01x"
  LinkPlacement = pos=(0,23.7,0) rot=(0,0,1;0rad)
  LinkedObject = -> Compound
  Placement = pos=(0,23.7,0) rot=(0,0,1;0rad)
  expr: Label = <<Pico_AddedHeaders_Socketed>>.Label + <<_>> + .LinkedObject.Label
  expr: Placement = <<vPico>>.J1Placement
FEATURE [App::Link] Link366  label="Pico_AddedHeaders_Socketed_L1_2u2"
  LinkPlacement = pos=(6,14.6,0) rot=(0,0,1;0rad)
  LinkedObject = -> Compound011
  Placement = pos=(6,14.6,0) rot=(0,0,1;0rad)
  expr: Label = <<Pico_AddedHeaders_Socketed>>.Label + <<_>> + .LinkedObject.Label
  expr: Placement = <<vPico>>.L1Placement
FEATURE [App::Link] Link367  label="Pico_AddedHeaders_Socketed_Q1_DMG1012T"
  LinkPlacement = pos=(6.4,7.2,0) rot=(0,0,1;0rad)
  LinkedObject = -> Compound012
  Placement = pos=(6.4,7.2,0) rot=(0,0,1;0rad)
  expr: Label = <<Pico_AddedHeaders_Socketed>>.Label + <<_>> + .LinkedObject.Label
  expr: Placement = <<vPico>>.Q1Placement
FEATURE [App::Link] Link368  label="Pico_AddedHeaders_Socketed_SW1_TP-1221U-K9K5325"
  LinkPlacement = pos=(-3.5,13.5,0) rot=(0,0,1;0rad)
  LinkedObject = -> Compound014
  Placement = pos=(-3.5,13.5,0) rot=(0,0,1;0rad)
  expr: Label = <<Pico_AddedHeaders_Socketed>>.Label + <<_>> + .LinkedObject.Label
  expr: Placement = <<vPico>>.SW1Placement
FEATURE [App::Link] Link369  label="Pico_AddedHeaders_Socketed_U1_RP2040"
  LinkPlacement = pos=(0,-0.5,0) rot=(0,0,1;0rad)
  LinkedObject = -> Compound015
  Placement = pos=(0,-0.5,0) rot=(0,0,1;0rad)
  expr: Label = <<Pico_AddedHeaders_Socketed>>.Label + <<_>> + .LinkedObject.Label
  expr: Placement = <<vPico>>.U1Placement
FEATURE [App::Link] Link370  label="Pico_AddedHeaders_Socketed_U2_RT6150B-33GQW"
  LinkPlacement = pos=(2.9,14.6,0) rot=(0,0,1;3.14159rad)
  LinkedObject = -> Compound016
  Placement = pos=(2.9,14.6,0) rot=(0,0,1;3.14159rad)
  expr: Label = <<Pico_AddedHeaders_Socketed>>.Label + <<_>> + .LinkedObject.Label
  expr: Placement = <<vPico>>.U2Placement
FEATURE [App::Link] Link371  label="Pico_AddedHeaders_Socketed_U3_W25Q16JVUXIQ"
  LinkPlacement = pos=(-3.8,6.4,0) rot=(0,0,1;1.5708rad)
  LinkedObject = -> Compound018
  Placement = pos=(-3.8,6.4,0) rot=(0,0,1;1.5708rad)
  expr: Label = <<Pico_AddedHeaders_Socketed>>.Label + <<_>> + .LinkedObject.Label
  expr: Placement = <<vPico>>.U3Placement
FEATURE [App::Link] Link372  label="Pico_AddedHeaders_Socketed_X1_X12M000000S096"
  LinkPlacement = pos=(-2.3,-9.05,0) rot=(0,0,1;0rad)
  LinkedObject = -> Compound019
  Placement = pos=(-2.3,-9.05,0) rot=(0,0,1;0rad)
  expr: Label = <<Pico_AddedHeaders_Socketed>>.Label + <<_>> + .LinkedObject.Label
  expr: Placement = <<vPico>>.X1Placement
FEATURE [App::Link] Link374  label="Pico_W_AddedHeaders_C1_47u"
  LinkPlacement = pos=(1.9,18.07,0) rot=(0,0,1;0rad)
  LinkedObject = -> Compound006
  Placement = pos=(1.9,18.07,0) rot=(0,0,1;0rad)
  expr: Label = <<Pico_W_AddedHeaders>>.Label + <<_>> + .LinkedObject.Label
  expr: Placement = <<vPicoW>>.C1Placement
FEATURE [App::Link] Link375  label="Pico_W_AddedHeaders_Board_Link"
  LinkedObject = -> Fusion002
  expr: Label = <<Pico_W_AddedHeaders>>.Label + <<_Board>> + <<_Link>>
FEATURE [App::Link] Link376  label="Pico_W_AddedHeaders_C2_47u"
  LinkPlacement = pos=(2.01,10.79,0) rot=(0,0,1;0rad)
  LinkedObject = -> Compound008
  Placement = pos=(2.01,10.79,0) rot=(0,0,1;0rad)
  expr: Label = <<Pico_W_AddedHeaders>>.Label + <<_>> + .LinkedObject.Label
  expr: Placement = <<vPicoW>>.C2Placement
FEATURE [App::Link] Link377  label="Pico_W_AddedHeaders_C21_47u"
  LinkPlacement = pos=(2.01,9.07,0) rot=(0,0,1;0rad)
  LinkedObject = -> Compound009
  Placement = pos=(2.01,9.07,0) rot=(0,0,1;0rad)
  expr: Label = <<Pico_W_AddedHeaders>>.Label + <<_>> + .LinkedObject.Label
  expr: Placement = <<vPicoW>>.C21Placement
FEATURE [App::Link] Link378  label="Pico_W_AddedHeaders_D1_MBR120VLSFT1G"
  LinkPlacement = pos=(6,18.9,0) rot=(0,0,1;0rad)
  LinkedObject = -> Compound007
  Placement = pos=(6,18.9,0) rot=(0,0,1;0rad)
  expr: Label = <<Pico_W_AddedHeaders>>.Label + <<_>> + .LinkedObject.Label
  expr: Placement = <<vPico>>.D1Placement
FEATURE [App::Link] Link379  label="Pico_W_AddedHeaders_D2_QSME-C194"
  LinkPlacement = pos=(-5.7,20.7,0) rot=(0,0,1;0rad)
  LinkedObject = -> Part013
  Placement = pos=(-5.7,20.7,0) rot=(0,0,1;0rad)
  expr: Label = <<Pico_W_AddedHeaders>>.Label + <<_>> + .LinkedObject.Label
  expr: Placement = <<vPico>>.D2Placement
FEATURE [App::Link] Link380  label="Pico_W_AddedHeaders_J1_690T505-x62-01x"
  LinkPlacement = pos=(0,23.7,0) rot=(0,0,1;0rad)
  LinkedObject = -> Compound
  Placement = pos=(0,23.7,0) rot=(0,0,1;0rad)
  expr: Label = <<Pico_W_AddedHeaders>>.Label + <<_>> + .LinkedObject.Label
  expr: Placement = <<vPico>>.J1Placement
FEATURE [App::Link] Link382  label="Pico_W_AddedHeaders_L1_2u2"
  LinkPlacement = pos=(6,14.6,0) rot=(0,0,1;0rad)
  LinkedObject = -> Compound011
  Placement = pos=(6,14.6,0) rot=(0,0,1;0rad)
  expr: Label = <<Pico_W_AddedHeaders>>.Label + <<_>> + .LinkedObject.Label
  expr: Placement = <<vPico>>.L1Placement
FEATURE [App::Link] Link383  label="Pico_W_AddedHeaders_Q1_DMG1012T"
  LinkPlacement = pos=(6.49,7.76,0) rot=(0,0,1;0rad)
  LinkedObject = -> Compound012
  Placement = pos=(6.49,7.76,0) rot=(0,0,1;0rad)
  expr: Label = <<Pico_W_AddedHeaders>>.Label + <<_>> + .LinkedObject.Label
  expr: Placement = <<vPicoW>>.Q1Placement
FEATURE [App::Link] Link384  label="Pico_W_AddedHeaders_SH1_CYW43439"
  LinkPlacement = pos=(0,-12.3,0) rot=(0,0,1;0rad)
  LinkedObject = -> Compound013
  Placement = pos=(0,-12.3,0) rot=(0,0,1;0rad)
  expr: Label = <<Pico_W_AddedHeaders>>.Label + <<_>> + .LinkedObject.Label
  expr: Placement = <<vPicoW>>.SH1Placement
FEATURE [App::Link] Link385  label="Pico_W_AddedHeaders_SW1_TP-1221U-K9K5325"
  LinkPlacement = pos=(-3.5,13.5,0) rot=(0,0,1;0rad)
  LinkedObject = -> Compound014
  Placement = pos=(-3.5,13.5,0) rot=(0,0,1;0rad)
  expr: Label = <<Pico_W_AddedHeaders>>.Label + <<_>> + .LinkedObject.Label
  expr: Placement = <<vPico>>.SW1Placement
FEATURE [App::Link] Link386  label="Pico_W_AddedHeaders_U1_RP2040"
  LinkPlacement = pos=(0,1.55,0) rot=(0,0,1;0rad)
  LinkedObject = -> Compound015
  Placement = pos=(0,1.55,0) rot=(0,0,1;0rad)
  expr: Label = <<Pico_W_AddedHeaders>>.Label + <<_>> + .LinkedObject.Label
  expr: Placement = <<vPicoW>>.U1Placement
FEATURE [App::Link] Link387  label="Pico_W_AddedHeaders_U2_RT6154AGQW"
  LinkPlacement = pos=(2.3,14.6,0) rot=(0,0,1;1.5708rad)
  LinkedObject = -> Compound017
  Placement = pos=(2.3,14.6,0) rot=(0,0,1;1.5708rad)
  expr: Label = <<Pico_W_AddedHeaders>>.Label + <<_>> + .LinkedObject.Label
  expr: Placement = <<vPicoW>>.U2Placement
FEATURE [App::Link] Link388  label="Pico_W_AddedHeaders_U3_W25Q16JVUXIQ"
  LinkPlacement = pos=(-3.32,8.69,0) rot=(0,0,1;0rad)
  LinkedObject = -> Compound018
  Placement = pos=(-3.32,8.69,0) rot=(0,0,1;0rad)
  expr: Label = <<Pico_W_AddedHeaders>>.Label + <<_>> + .LinkedObject.Label
  expr: Placement = <<vPicoW>>.U3Placement
FEATURE [App::Link] Link389  label="Pico_W_AddedHeaders_X1_X12M000000S096"
  LinkPlacement = pos=(-4.7,-4.91,0) rot=(0,0,1;0rad)
  LinkedObject = -> Compound019
  Placement = pos=(-4.7,-4.91,0) rot=(0,0,1;0rad)
  expr: Label = <<Pico_W_AddedHeaders>>.Label + <<_>> + .LinkedObject.Label
  expr: Placement = <<vPicoW>>.X1Placement
FEATURE [App::Link] Link391  label="Pico_W_AddedHeaders_Socketed_C1_47u"
  LinkPlacement = pos=(1.9,18.07,0) rot=(0,0,1;0rad)
  LinkedObject = -> Compound006
  Placement = pos=(1.9,18.07,0) rot=(0,0,1;0rad)
  expr: Label = <<Pico_W_AddedHeaders_Socketed>>.Label + <<_>> + .LinkedObject.Label
  expr: Placement = <<vPicoW>>.C1Placement
FEATURE [App::Link] Link392  label="Pico_W_AddedHeaders_Socketed_Board_Link"
  LinkedObject = -> Fusion002
  expr: Label = <<Pico_W_AddedHeaders_Socketed>>.Label + <<_Board>> + <<_Link>>
FEATURE [App::Link] Link393  label="Pico_W_AddedHeaders_Socketed_C2_47u"
  LinkPlacement = pos=(2.01,10.79,0) rot=(0,0,1;0rad)
  LinkedObject = -> Compound008
  Placement = pos=(2.01,10.79,0) rot=(0,0,1;0rad)
  expr: Label = <<Pico_W_AddedHeaders_Socketed>>.Label + <<_>> + .LinkedObject.Label
  expr: Placement = <<vPicoW>>.C2Placement
FEATURE [App::Link] Link394  label="Pico_W_AddedHeaders_Socketed_C21_47u"
  LinkPlacement = pos=(2.01,9.07,0) rot=(0,0,1;0rad)
  LinkedObject = -> Compound009
  Placement = pos=(2.01,9.07,0) rot=(0,0,1;0rad)
  expr: Label = <<Pico_W_AddedHeaders_Socketed>>.Label + <<_>> + .LinkedObject.Label
  expr: Placement = <<vPicoW>>.C21Placement
FEATURE [App::Link] Link395  label="Pico_W_AddedHeaders_Socketed_D1_MBR120VLSFT1G"
  LinkPlacement = pos=(6,18.9,0) rot=(0,0,1;0rad)
  LinkedObject = -> Compound007
  Placement = pos=(6,18.9,0) rot=(0,0,1;0rad)
  expr: Label = <<Pico_W_AddedHeaders_Socketed>>.Label + <<_>> + .LinkedObject.Label
  expr: Placement = <<vPico>>.D1Placement
FEATURE [App::Link] Link396  label="Pico_W_AddedHeaders_Socketed_D2_QSME-C194"
  LinkPlacement = pos=(-5.7,20.7,0) rot=(0,0,1;0rad)
  LinkedObject = -> Part013
  Placement = pos=(-5.7,20.7,0) rot=(0,0,1;0rad)
  expr: Label = <<Pico_W_AddedHeaders_Socketed>>.Label + <<_>> + .LinkedObject.Label
  expr: Placement = <<vPico>>.D2Placement
FEATURE [App::Link] Link397  label="Pico_W_AddedHeaders_Socketed_J1_690T505-x62-01x"
  LinkPlacement = pos=(0,23.7,0) rot=(0,0,1;0rad)
  LinkedObject = -> Compound
  Placement = pos=(0,23.7,0) rot=(0,0,1;0rad)
  expr: Label = <<Pico_W_AddedHeaders_Socketed>>.Label + <<_>> + .LinkedObject.Label
  expr: Placement = <<vPico>>.J1Placement
FEATURE [App::Link] Link399  label="Pico_W_AddedHeaders_Socketed_L1_2u2"
  LinkPlacement = pos=(6,14.6,0) rot=(0,0,1;0rad)
  LinkedObject = -> Compound011
  Placement = pos=(6,14.6,0) rot=(0,0,1;0rad)
  expr: Label = <<Pico_W_AddedHeaders_Socketed>>.Label + <<_>> + .LinkedObject.Label
  expr: Placement = <<vPico>>.L1Placement
FEATURE [App::Link] Link400  label="Pico_W_AddedHeaders_Socketed_Q1_DMG1012T"
  LinkPlacement = pos=(6.4,7.2,0) rot=(0,0,1;0rad)
  LinkedObject = -> Compound012
  Placement = pos=(6.4,7.2,0) rot=(0,0,1;0rad)
  expr: Label = <<Pico_W_AddedHeaders_Socketed>>.Label + <<_>> + .LinkedObject.Label
FEATURE [App::Link] Link401  label="Pico_W_AddedHeaders_Socketed_SH1_CYW43439"
  LinkPlacement = pos=(0,-12.3,0) rot=(0,0,1;0rad)
  LinkedObject = -> Compound013
  Placement = pos=(0,-12.3,0) rot=(0,0,1;0rad)
  expr: Label = <<Pico_W_AddedHeaders_Socketed>>.Label + <<_>> + .LinkedObject.Label
  expr: Placement = <<vPicoW>>.SH1Placement
FEATURE [App::Link] Link402  label="Pico_W_AddedHeaders_Socketed_SW1_TP-1221U-K9K5325"
  LinkPlacement = pos=(-3.5,13.5,0) rot=(0,0,1;0rad)
  LinkedObject = -> Compound014
  Placement = pos=(-3.5,13.5,0) rot=(0,0,1;0rad)
  expr: Label = <<Pico_W_AddedHeaders_Socketed>>.Label + <<_>> + .LinkedObject.Label
  expr: Placement = <<vPico>>.SW1Placement
FEATURE [App::Link] Link403  label="Pico_W_AddedHeaders_Socketed_U1_RP2040"
  LinkPlacement = pos=(0,1.55,0) rot=(0,0,1;0rad)
  LinkedObject = -> Compound015
  Placement = pos=(0,1.55,0) rot=(0,0,1;0rad)
  expr: Label = <<Pico_W_AddedHeaders_Socketed>>.Label + <<_>> + .LinkedObject.Label
  expr: Placement = <<vPicoW>>.U1Placement
FEATURE [App::Link] Link404  label="Pico_W_AddedHeaders_Socketed_U2_RT6154AGQW"
  LinkPlacement = pos=(2.3,14.6,0) rot=(0,0,1;1.5708rad)
  LinkedObject = -> Compound017
  Placement = pos=(2.3,14.6,0) rot=(0,0,1;1.5708rad)
  expr: Label = <<Pico_W_AddedHeaders_Socketed>>.Label + <<_>> + .LinkedObject.Label
  expr: Placement = <<vPicoW>>.U2Placement
FEATURE [App::Link] Link405  label="Pico_W_AddedHeaders_Socketed_U3_W25Q16JVUXIQ"
  LinkPlacement = pos=(-3.32,8.69,0) rot=(0,0,1;0rad)
  LinkedObject = -> Compound018
  Placement = pos=(-3.32,8.69,0) rot=(0,0,1;0rad)
  expr: Label = <<Pico_W_AddedHeaders_Socketed>>.Label + <<_>> + .LinkedObject.Label
  expr: Placement = <<vPicoW>>.U3Placement
FEATURE [App::Link] Link406  label="Pico_W_AddedHeaders_Socketed_X1_X12M000000S096"
  LinkPlacement = pos=(-4.7,-4.91,0) rot=(0,0,1;0rad)
  LinkedObject = -> Compound019
  Placement = pos=(-4.7,-4.91,0) rot=(0,0,1;0rad)
  expr: Label = <<Pico_W_AddedHeaders_Socketed>>.Label + <<_>> + .LinkedObject.Label
  expr: Placement = <<vPicoW>>.X1Placement
FEATURE [App::Part] Part065  label="Pico_AddedHeaders_Components"
  Group = -> [Link344,Link346,Link347,Link348,Link349,Link351,Link352,Link353,Link354,Link355,Link356,Link357]
  Origin = -> Origin095
  Placement = pos=(0,0,1) rot=(0,0,1;0rad)
  expr: .Placement.Base.z = <<vPico>>.BoardThickness
  expr: Label = <<Pico_AddedHeaders>>.Label + <<_Components>>
FEATURE [App::Part] Part066  label="Pico_AddedHeaders_Module"
  Group = -> [Link345,Part065]
  Origin = -> Origin096
  Placement = pos=(0,0,2.54) rot=(0,0,1;0rad)
  expr: .Placement.Base.z = <<vHeader>>.InsulationThickness
  expr: Label = <<Pico_AddedHeaders>>.Label + <<_Module>>
FEATURE [App::Part] Part068  label="Pico_AddedHeaders_Socketed_Components"
  Group = -> [Link359,Link361,Link362,Link363,Link364,Link366,Link367,Link368,Link369,Link370,Link371,Link372]
  Origin = -> Origin098
  Placement = pos=(0,0,1) rot=(0,0,1;0rad)
  expr: .Placement.Base.z = <<vPico>>.BoardThickness
  expr: Label = <<Pico_AddedHeaders_Socketed>>.Label + <<_Components>>
FEATURE [App::Part] Part069  label="Pico_AddedHeaders_Socketed_Module"
  Group = -> [Link360,Part068]
  Origin = -> Origin099
  Placement = pos=(0,0,11) rot=(0,0,1;0rad)
  expr: .Placement.Base.z = <<vHeader>>.InsulationThickness + <<vSocket>>.BodyHeight
  expr: Label = <<Pico_AddedHeaders_Socketed>>.Label + <<_Module>>
FEATURE [App::Part] Part071  label="Pico_W_AddedHeaders_Components"
  Group = -> [Link374,Link376,Link377,Link378,Link379,Link380,Link382,Link383,Link384,Link385,Link386,Link387,Link388,Link389]
  Origin = -> Origin101
  Placement = pos=(0,0,1) rot=(0,0,1;0rad)
  expr: .Placement.Base.z = <<vPico>>.BoardThickness
  expr: Label = <<Pico_W_AddedHeaders>>.Label + <<_Components>>
FEATURE [App::Part] Part072  label="Pico_W_AddedHeaders_Module"
  Group = -> [Link375,Part071]
  Origin = -> Origin102
  Placement = pos=(0,0,2.54) rot=(0,0,1;0rad)
  expr: .Placement.Base.z = <<vHeader>>.InsulationThickness
  expr: Label = <<Pico_W_AddedHeaders>>.Label + <<_Module>>
FEATURE [App::Part] Part074  label="Pico_W_AddedHeaders_Socketed_Components"
  Group = -> [Link391,Link393,Link394,Link395,Link396,Link397,Link399,Link400,Link401,Link402,Link403,Link404,Link405,Link406]
  Origin = -> Origin104
  Placement = pos=(0,0,1) rot=(0,0,1;0rad)
  expr: .Placement.Base.z = <<vPico>>.BoardThickness
  expr: Label = <<Pico_W_AddedHeaders_Socketed>>.Label + <<_Components>>
FEATURE [App::Part] Part075  label="Pico_W_AddedHeaders_Socketed_Module"
  Group = -> [Link392,Part074]
  Origin = -> Origin105
  Placement = pos=(0,0,11) rot=(0,0,1;0rad)
  expr: .Placement.Base.z = <<vHeader>>.InsulationThickness + <<vSocket>>.BodyHeight
  expr: Label = <<Pico_W_AddedHeaders_Socketed>>.Label + <<_Module>>
FEATURE [App::Link] Link415  label="Pico_AddedHeaders_SIP-20_Header_Left001"
  LinkTransform = true
  LinkedObject = -> Part064 [Link492.]
FEATURE [App::Link] Link416  label="Pico_AddedHeaders_SIP-20_Header_Right001"
  LinkTransform = true
  LinkedObject = -> Part064 [Link493.]
FEATURE [App::Link] Link417  label="Pico_AddedHeaders_Board_Link001"
  LinkTransform = true
  LinkedObject = -> Part064 [Part066.Link345.]
FEATURE [App::Link] Link418  label="Pico_AddedHeaders_C1_47u001"
  LinkTransform = true
  LinkedObject = -> Part064 [Part066.Part065.Link344.]
FEATURE [App::Link] Link419  label="Pico_AddedHeaders_C2_47u001"
  LinkTransform = true
  LinkedObject = -> Part064 [Part066.Part065.Link346.]
FEATURE [App::Link] Link420  label="Pico_AddedHeaders_D1_MBR120VLSFT1G001"
  LinkTransform = true
  LinkedObject = -> Part064 [Part066.Part065.Link347.]
FEATURE [App::Link] Link421  label="D2_QSME-C194_Base007"
  LinkTransform = true
  LinkedObject = -> Part064 [Part066.Part065.Link348.Body010.]
FEATURE [App::Link] Link422  label="D2_QSME-C194_Lens007"
  LinkTransform = true
  LinkedObject = -> Part064 [Part066.Part065.Link348.Box024.]
FEATURE [App::Link] Link423  label="D2_QSME-C194_Phosphor_Link006"
  LinkTransform = true
  LinkedObject = -> Part064 [Part066.Part065.Link348.Link092.]
FEATURE [App::Link] Link424  label="Pico_AddedHeaders_J1_690T505-x62-01x001"
  LinkTransform = true
  LinkedObject = -> Part064 [Part066.Part065.Link349.]
FEATURE [App::Link] Link425  label="Pico_AddedHeaders_L1_2u003"
  LinkTransform = true
  LinkedObject = -> Part064 [Part066.Part065.Link351.]
FEATURE [App::Link] Link426  label="Pico_AddedHeaders_Q1_DMG1012T001"
  LinkTransform = true
  LinkedObject = -> Part064 [Part066.Part065.Link352.]
FEATURE [App::Link] Link427  label="Pico_AddedHeaders_SW1_TP-1221U-K9K5326"
  LinkTransform = true
  LinkedObject = -> Part064 [Part066.Part065.Link353.]
FEATURE [App::Link] Link428  label="Pico_AddedHeaders_U1_RP2041"
  LinkTransform = true
  LinkedObject = -> Part064 [Part066.Part065.Link354.]
FEATURE [App::Link] Link429  label="Pico_AddedHeaders_U2_RT6150B-33GQW001"
  LinkTransform = true
  LinkedObject = -> Part064 [Part066.Part065.Link355.]
FEATURE [App::Link] Link430  label="Pico_AddedHeaders_U3_W25Q16JVUXIQ001"
  LinkTransform = true
  LinkedObject = -> Part064 [Part066.Part065.Link356.]
FEATURE [App::Link] Link431  label="Pico_AddedHeaders_X1_X12M000000S097"
  LinkTransform = true
  LinkedObject = -> Part064 [Part066.Part065.Link357.]
FEATURE [Part::Compound] Compound029  label="RaspberryPi_Pico_AddedHeaders_Compound"
  Links = -> [Link415,Link416,Link417,Link418,Link419,Link420,Link421,Link422,Link423,Link424,Link425,Link426,Link427,Link428,Link429,Link430,Link431]
FEATURE [App::Link] Link432  label="Pico_AddedHeaders_Socketed_SIP-20_Header_Left001"
  LinkTransform = true
  LinkedObject = -> Part067 [Link494.]
FEATURE [App::Link] Link433  label="Pico_AddedHeaders_Socketed_SIP-20_Header_Right001"
  LinkTransform = true
  LinkedObject = -> Part067 [Link495.]
FEATURE [App::Link] Link434  label="Pico_AddedHeaders_Socketed_Board_Link001"
  LinkTransform = true
  LinkedObject = -> Part067 [Part069.Link360.]
FEATURE [App::Link] Link435  label="Pico_AddedHeaders_Socketed_C1_47u001"
  LinkTransform = true
  LinkedObject = -> Part067 [Part069.Part068.Link359.]
FEATURE [App::Link] Link436  label="Pico_AddedHeaders_Socketed_C2_47u001"
  LinkTransform = true
  LinkedObject = -> Part067 [Part069.Part068.Link361.]
FEATURE [App::Link] Link437  label="Pico_AddedHeaders_Socketed_D1_MBR120VLSFT1G001"
  LinkTransform = true
  LinkedObject = -> Part067 [Part069.Part068.Link362.]
FEATURE [App::Link] Link438  label="D2_QSME-C194_Base008"
  LinkTransform = true
  LinkedObject = -> Part067 [Part069.Part068.Link363.Body010.]
FEATURE [App::Link] Link439  label="D2_QSME-C194_Lens008"
  LinkTransform = true
  LinkedObject = -> Part067 [Part069.Part068.Link363.Box024.]
FEATURE [App::Link] Link440  label="D2_QSME-C194_Phosphor_Link007"
  LinkTransform = true
  LinkedObject = -> Part067 [Part069.Part068.Link363.Link092.]
FEATURE [App::Link] Link441  label="Pico_AddedHeaders_Socketed_J1_690T505-x62-01x001"
  LinkTransform = true
  LinkedObject = -> Part067 [Part069.Part068.Link364.]
FEATURE [App::Link] Link442  label="Pico_AddedHeaders_Socketed_L1_2u003"
  LinkTransform = true
  LinkedObject = -> Part067 [Part069.Part068.Link366.]
FEATURE [App::Link] Link443  label="Pico_AddedHeaders_Socketed_Q1_DMG1012T001"
  LinkTransform = true
  LinkedObject = -> Part067 [Part069.Part068.Link367.]
FEATURE [App::Link] Link444  label="Pico_AddedHeaders_Socketed_SW1_TP-1221U-K9K5326"
  LinkTransform = true
  LinkedObject = -> Part067 [Part069.Part068.Link368.]
FEATURE [App::Link] Link445  label="Pico_AddedHeaders_Socketed_U1_RP2041"
  LinkTransform = true
  LinkedObject = -> Part067 [Part069.Part068.Link369.]
FEATURE [App::Link] Link446  label="Pico_AddedHeaders_Socketed_U2_RT6150B-33GQW001"
  LinkTransform = true
  LinkedObject = -> Part067 [Part069.Part068.Link370.]
FEATURE [App::Link] Link447  label="Pico_AddedHeaders_Socketed_U3_W25Q16JVUXIQ001"
  LinkTransform = true
  LinkedObject = -> Part067 [Part069.Part068.Link371.]
FEATURE [App::Link] Link448  label="Pico_AddedHeaders_Socketed_X1_X12M000000S097"
  LinkTransform = true
  LinkedObject = -> Part067 [Part069.Part068.Link372.]
FEATURE [Part::Compound] Compound030  label="RaspberryPi_Pico_AddedHeaders_Socketed_Compound"
  Links = -> [Link432,Link433,Link434,Link435,Link436,Link437,Link438,Link439,Link440,Link441,Link442,Link443,Link444,Link445,Link446,Link447,Link448]
FEATURE [App::Link] Link449  label="Pico_W_AddedHeaders_SIP-20_Header_Left001"
  LinkTransform = true
  LinkedObject = -> Part070 [Link496.]
FEATURE [App::Link] Link450  label="Pico_W_AddedHeaders_SIP-20_Header_Right001"
  LinkTransform = true
  LinkedObject = -> Part070 [Link497.]
FEATURE [App::Link] Link451  label="Pico_W_AddedHeaders_Board_Link001"
  LinkTransform = true
  LinkedObject = -> Part070 [Part072.Link375.]
FEATURE [App::Link] Link452  label="Pico_W_AddedHeaders_C1_47u001"
  LinkTransform = true
  LinkedObject = -> Part070 [Part072.Part071.Link374.]
FEATURE [App::Link] Link453  label="Pico_W_AddedHeaders_C2_47u001"
  LinkTransform = true
  LinkedObject = -> Part070 [Part072.Part071.Link376.]
FEATURE [App::Link] Link454  label="Pico_W_AddedHeaders_C21_47u001"
  LinkTransform = true
  LinkedObject = -> Part070 [Part072.Part071.Link377.]
FEATURE [App::Link] Link455  label="Pico_W_AddedHeaders_D1_MBR120VLSFT1G001"
  LinkTransform = true
  LinkedObject = -> Part070 [Part072.Part071.Link378.]
FEATURE [App::Link] Link456  label="D2_QSME-C194_Base009"
  LinkTransform = true
  LinkedObject = -> Part070 [Part072.Part071.Link379.Body010.]
FEATURE [App::Link] Link457  label="D2_QSME-C194_Lens009"
  LinkTransform = true
  LinkedObject = -> Part070 [Part072.Part071.Link379.Box024.]
FEATURE [App::Link] Link458  label="D2_QSME-C194_Phosphor_Link008"
  LinkTransform = true
  LinkedObject = -> Part070 [Part072.Part071.Link379.Link092.]
FEATURE [App::Link] Link459  label="Pico_W_AddedHeaders_J1_690T505-x62-01x001"
  LinkTransform = true
  LinkedObject = -> Part070 [Part072.Part071.Link380.]
FEATURE [App::Link] Link460  label="Pico_W_AddedHeaders_L1_2u003"
  LinkTransform = true
  LinkedObject = -> Part070 [Part072.Part071.Link382.]
FEATURE [App::Link] Link461  label="Pico_W_AddedHeaders_Q1_DMG1012T001"
  LinkTransform = true
  LinkedObject = -> Part070 [Part072.Part071.Link383.]
FEATURE [App::Link] Link462  label="Pico_W_AddedHeaders_SH1_CYW43440"
  LinkTransform = true
  LinkedObject = -> Part070 [Part072.Part071.Link384.]
FEATURE [App::Link] Link463  label="Pico_W_AddedHeaders_SW1_TP-1221U-K9K5326"
  LinkTransform = true
  LinkedObject = -> Part070 [Part072.Part071.Link385.]
FEATURE [App::Link] Link464  label="Pico_W_AddedHeaders_U1_RP2041"
  LinkTransform = true
  LinkedObject = -> Part070 [Part072.Part071.Link386.]
FEATURE [App::Link] Link465  label="Pico_W_AddedHeaders_U2_RT6154AGQW001"
  LinkTransform = true
  LinkedObject = -> Part070 [Part072.Part071.Link387.]
FEATURE [App::Link] Link466  label="Pico_W_AddedHeaders_U3_W25Q16JVUXIQ001"
  LinkTransform = true
  LinkedObject = -> Part070 [Part072.Part071.Link388.]
FEATURE [App::Link] Link467  label="Pico_W_AddedHeaders_X1_X12M000000S097"
  LinkTransform = true
  LinkedObject = -> Part070 [Part072.Part071.Link389.]
FEATURE [Part::Compound] Compound031  label="RaspberryPi_Pico_W_AddedHeaders_Compound"
  Links = -> [Link449,Link450,Link451,Link452,Link453,Link454,Link455,Link456,Link457,Link458,Link459,Link460,Link461,Link462,Link463,Link464,Link465,Link466,Link467]
FEATURE [App::Link] Link468  label="Pico_W_AddedHeaders_Socketed_SIP-20_Header_Left001"
  LinkTransform = true
  LinkedObject = -> Part073 [Link498.]
FEATURE [App::Link] Link469  label="Pico_W_AddedHeaders_Socketed_SIP-20_Header_Right001"
  LinkTransform = true
  LinkedObject = -> Part073 [Link499.]
FEATURE [App::Link] Link470  label="Pico_W_AddedHeaders_Socketed_Board_Link001"
  LinkTransform = true
  LinkedObject = -> Part073 [Part075.Link392.]
FEATURE [App::Link] Link471  label="Pico_W_AddedHeaders_Socketed_C1_47u001"
  LinkTransform = true
  LinkedObject = -> Part073 [Part075.Part074.Link391.]
FEATURE [App::Link] Link472  label="Pico_W_AddedHeaders_Socketed_C2_47u001"
  LinkTransform = true
  LinkedObject = -> Part073 [Part075.Part074.Link393.]
FEATURE [App::Link] Link473  label="Pico_W_AddedHeaders_Socketed_C21_47u001"
  LinkTransform = true
  LinkedObject = -> Part073 [Part075.Part074.Link394.]
FEATURE [App::Link] Link474  label="Pico_W_AddedHeaders_Socketed_D1_MBR120VLSFT1G001"
  LinkTransform = true
  LinkedObject = -> Part073 [Part075.Part074.Link395.]
FEATURE [App::Link] Link475  label="D2_QSME-C194_Base010"
  LinkTransform = true
  LinkedObject = -> Part073 [Part075.Part074.Link396.Body010.]
FEATURE [App::Link] Link476  label="D2_QSME-C194_Lens010"
  LinkTransform = true
  LinkedObject = -> Part073 [Part075.Part074.Link396.Box024.]
FEATURE [App::Link] Link477  label="D2_QSME-C194_Phosphor_Link009"
  LinkTransform = true
  LinkedObject = -> Part073 [Part075.Part074.Link396.Link092.]
FEATURE [App::Link] Link478  label="Pico_W_AddedHeaders_Socketed_J1_690T505-x62-01x001"
  LinkTransform = true
  LinkedObject = -> Part073 [Part075.Part074.Link397.]
FEATURE [App::Link] Link479  label="Pico_W_AddedHeaders_Socketed_L1_2u003"
  LinkTransform = true
  LinkedObject = -> Part073 [Part075.Part074.Link399.]
FEATURE [App::Link] Link480  label="Pico_W_AddedHeaders_Socketed_Q1_DMG1012T001"
  LinkTransform = true
  LinkedObject = -> Part073 [Part075.Part074.Link400.]
FEATURE [App::Link] Link481  label="Pico_W_AddedHeaders_Socketed_SH1_CYW43440"
  LinkTransform = true
  LinkedObject = -> Part073 [Part075.Part074.Link401.]
FEATURE [App::Link] Link482  label="Pico_W_AddedHeaders_Socketed_SW1_TP-1221U-K9K5326"
  LinkTransform = true
  LinkedObject = -> Part073 [Part075.Part074.Link402.]
FEATURE [App::Link] Link483  label="Pico_W_AddedHeaders_Socketed_U1_RP2041"
  LinkTransform = true
  LinkedObject = -> Part073 [Part075.Part074.Link403.]
FEATURE [App::Link] Link484  label="Pico_W_AddedHeaders_Socketed_U2_RT6154AGQW001"
  LinkTransform = true
  LinkedObject = -> Part073 [Part075.Part074.Link404.]
FEATURE [App::Link] Link485  label="Pico_W_AddedHeaders_Socketed_U3_W25Q16JVUXIQ001"
  LinkTransform = true
  LinkedObject = -> Part073 [Part075.Part074.Link405.]
FEATURE [App::Link] Link486  label="Pico_W_AddedHeaders_Socketed_X1_X12M000000S097"
  LinkTransform = true
  LinkedObject = -> Part073 [Part075.Part074.Link406.]
FEATURE [Part::Compound] Compound032  label="RaspberryPi_Pico_W_AddedHeaders_Socketed_Compound"
  Links = -> [Link468,Link469,Link470,Link471,Link472,Link473,Link474,Link475,Link476,Link477,Link478,Link479,Link480,Link481,Link482,Link483,Link484,Link485,Link486]
FEATURE [PartDesign::LinearPattern] LinearPattern085  label="LinearPattern_Socket_Holes"
  BaseFeature = -> Pocket
  Direction = -> Y_Axis007
  Length = 48.26
  Occurrences = 20
  Originals = -> [Pocket]
  Placement = pos=(0,0,0) rot=(1,0,0;1.5708rad)
  Reversed = true
  expr: Length = <<vPico>>.PinPitch * (<<vPico>>.PinDIPCount / 2 - 1)
FEATURE [PartDesign::SubtractiveWedge] Wedge  label="SubtractiveWedge_HoleMargin"
  AttacherType = Attacher::AttachEngine3D
  AttachmentOffset = pos=(0,0,0) rot=(-1,0,0;1.5708rad)
  BaseFeature = -> LinearPattern085
  MapMode = 2
  Placement = pos=(-8.89,24.13,8.46) rot=(-1,0,0;1.5708rad)
  Support = -> [Sketch003]
  X2max = 0
  X2min = 0
  Xmax = 0.825
  Xmin = -0.825
  Ymax = 0.825
  Ymin = 0
  Z2max = 0
  Z2min = 0
  Zmax = 0.825
  Zmin = -0.825
  expr: X2max = 0
  expr: Xmax = <<vSocket>>.HoleMargin + <<vSocket>>.HoleWidth / 2
  expr: Xmin = -Xmax
  expr: Ymax = Xmax
  expr: Z2max = 0
  expr: Zmax = Xmax
  expr: Zmin = -Zmax
FEATURE [PartDesign::LinearPattern] LinearPattern001  label="LinearPattern_Socket_HoleMargins"
  BaseFeature = -> Wedge
  Direction = -> Y_Axis007
  Length = 48.26
  Occurrences = 20
  Originals = -> [Wedge]
  Placement = pos=(-8.89,24.13,8.46) rot=(-1,0,0;1.5708rad)
  Reversed = true
  expr: Length = <<vPico>>.PinPitch * (<<vPico>>.PinDIPCount / 2 - 1)
  expr: Occurrences = <<vPico>>.PinDIPCount / 2
FEATURE [PartDesign::Body] Body002  label="Socket_Body"
  Group = -> [Sketch002,Pad002,Sketch003,Pocket,LinearPattern085,Wedge,LinearPattern001]
  Origin = -> Origin007
  Tip = -> LinearPattern001
FEATURE [App::Link] Link487  label="Pico_H_DIP-40_W17.78mm_Header"
  LinkedObject = -> Compound033
  expr: Label = <<Pico_H>>.Label + <<_>> + .LinkedObject.Label
FEATURE [App::Part] Part049  label="RaspberryPi_Pico_H_STEP"
  Group = -> [Group040,Part051,Link487]
  License = MIT-0 (Public-domain-equivalent)
  LicenseURL = https://spdx.org/licenses/MIT-0.html
  Origin = -> Origin067
  expr: Label = <<RaspberryPi_>> + <<Pico_H>>.Label + <<_STEP>>
FEATURE [App::Link] Link488  label="Pico_H_Socketed_DIP-40_W17.78mm_Header"
  LinkPlacement = pos=(0,0,8.46) rot=(0,0,1;0rad)
  LinkedObject = -> Compound033
  Placement = pos=(0,0,8.46) rot=(0,0,1;0rad)
  expr: .Placement.Base.z = <<vSocket>>.BodyHeight
  expr: Label = <<Pico_H_Socketed>>.Label + <<_>> + .LinkedObject.Label
FEATURE [App::Part] Part052  label="RaspberryPi_Pico_H_Socketed_STEP"
  Group = -> [Group041,Part054,Link488]
  License = MIT-0 (Public-domain-equivalent)
  LicenseURL = https://spdx.org/licenses/MIT-0.html
  Origin = -> Origin070
  expr: Label = <<RaspberryPi_>> + <<Pico_H_Socketed>>.Label + <<_STEP>>
FEATURE [App::Link] Link489  label="Pico_WH_DIP-40_W17.78mm_Header"
  LinkedObject = -> Compound033
  expr: Label = <<Pico_WH>>.Label + <<_>> + .LinkedObject.Label
FEATURE [App::Part] Part057  label="RaspberryPi_Pico_WH_STEP"
  Group = -> [Group043,Part059,Link489]
  License = MIT-0 (Public-domain-equivalent)
  LicenseURL = https://spdx.org/licenses/MIT-0.html
  Origin = -> Origin075
  expr: Label = <<RaspberryPi_>> + <<Pico_WH>>.Label + <<_STEP>>
FEATURE [App::Link] Link490  label="Pico_WH_Socketed_DIP-40_W17.78mm_Header"
  LinkPlacement = pos=(0,0,8.46) rot=(0,0,1;0rad)
  LinkedObject = -> Compound033
  Placement = pos=(0,0,8.46) rot=(0,0,1;0rad)
  expr: .Placement.Base.z = <<vSocket>>.BodyHeight
  expr: Label = <<Pico_WH_Socketed>>.Label + <<_>> + .LinkedObject.Label
FEATURE [App::Part] Part060  label="RaspberryPi_Pico_WH_Socketed_STEP"
  Group = -> [Group044,Part062,Link490]
  License = MIT-0 (Public-domain-equivalent)
  LicenseURL = https://spdx.org/licenses/MIT-0.html
  Origin = -> Origin078
  expr: Label = <<RaspberryPi_>> + <<Pico_WH_Socketed>>.Label + <<_STEP>>
FEATURE [App::Link] Link  label="Socket_Left"
  LinkedObject = -> Compound034
  expr: Label = .LinkedObject.Label + <<_Left>>
FEATURE [App::Link] Link491  label="Socket_Right"
  LinkPlacement = pos=(17.78,0,0) rot=(0,0,1;0rad)
  LinkedObject = -> Compound034
  Placement = pos=(17.78,0,0) rot=(0,0,1;0rad)
  expr: .Placement.Base.x = <<vPico>>.BoardWidth - <<vPico>>.PinInset * 2
  expr: Label = .LinkedObject.Label + <<_Right>>
FEATURE [App::Part] Part048  label="DIP-40_W17.78mm_H8.51mm_Socket_STEP"
  Group = -> [Group034,Link,Link491]
  License = MIT-0 (Public-domain-equivalent)
  LicenseURL = https://spdx.org/licenses/MIT-0.html
  Origin = -> Origin066
  expr: Label = <<DIP-40_W17.78mm_H8.51mm>>.Label + <<_Socket>> + <<_STEP>>
FEATURE [App::Link] Link492  label="Pico_AddedHeaders_Header_Breakaway_Left"
  LinkedObject = -> Compound035
  expr: Label = <<Pico_AddedHeaders>>.Label + <<_>> + .LinkedObject.Label + <<_Left>>
FEATURE [App::Link] Link493  label="Pico_AddedHeaders_Header_Breakaway_Right"
  LinkPlacement = pos=(17.78,0,0) rot=(0,0,1;0rad)
  LinkedObject = -> Compound035
  Placement = pos=(17.78,0,0) rot=(0,0,1;0rad)
  expr: .Placement.Base.x = <<vPico>>.BoardWidth - <<vPico>>.PinInset * 2
  expr: Label = <<Pico_AddedHeaders>>.Label + <<_>> + .LinkedObject.Label + <<_Right>>
FEATURE [App::Part] Part064  label="RaspberryPi_Pico_AddedHeaders_STEP"
  Group = -> [Group049,Part066,Link492,Link493]
  License = MIT-0 (Public-domain-equivalent)
  LicenseURL = https://spdx.org/licenses/MIT-0.html
  Origin = -> Origin094
  expr: Label = <<RaspberryPi_>> + <<Pico_AddedHeaders>>.Label + <<_STEP>>
FEATURE [App::Link] Link494  label="Pico_AddedHeaders_Socketed_Header_Breakaway_Left"
  LinkPlacement = pos=(0,0,8.46) rot=(0,0,1;0rad)
  LinkedObject = -> Compound035
  Placement = pos=(0,0,8.46) rot=(0,0,1;0rad)
  expr: .Placement.Base.z = <<vSocket>>.BodyHeight
  expr: Label = <<Pico_AddedHeaders_Socketed>>.Label + <<_>> + .LinkedObject.Label + <<_Left>>
FEATURE [App::Link] Link495  label="Pico_AddedHeaders_Socketed_Header_Breakaway_Right"
  LinkPlacement = pos=(17.78,0,8.46) rot=(0,0,1;0rad)
  LinkedObject = -> Compound035
  Placement = pos=(17.78,0,8.46) rot=(0,0,1;0rad)
  expr: .Placement.Base.x = <<vPico>>.BoardWidth - <<vPico>>.PinInset * 2
  expr: .Placement.Base.z = <<vSocket>>.BodyHeight
  expr: Label = <<Pico_AddedHeaders_Socketed>>.Label + <<_>> + .LinkedObject.Label + <<_Right>>
FEATURE [App::Part] Part067  label="RaspberryPi_Pico_AddedHeaders_Socketed_STEP"
  Group = -> [Group050,Part069,Link494,Link495]
  License = MIT-0 (Public-domain-equivalent)
  LicenseURL = https://spdx.org/licenses/MIT-0.html
  Origin = -> Origin097
  expr: Label = <<RaspberryPi_>> + <<Pico_AddedHeaders_Socketed>>.Label + <<_STEP>>
FEATURE [App::Link] Link496  label="Pico_W_AddedHeaders_Header_Breakaway_Left"
  LinkedObject = -> Compound035
  expr: Label = <<Pico_W_AddedHeaders>>.Label + <<_>> + .LinkedObject.Label + <<_Left>>
FEATURE [App::Link] Link497  label="Pico_W_AddedHeaders_Header_Breakaway_Right"
  LinkPlacement = pos=(17.78,0,0) rot=(0,0,1;0rad)
  LinkedObject = -> Compound035
  Placement = pos=(17.78,0,0) rot=(0,0,1;0rad)
  expr: .Placement.Base.x = <<vPico>>.BoardWidth - <<vPico>>.PinInset * 2
  expr: Label = <<Pico_W_AddedHeaders>>.Label + <<_>> + .LinkedObject.Label + <<_Right>>
FEATURE [App::Part] Part070  label="RaspberryPi_Pico_W_AddedHeaders_STEP"
  Group = -> [Group051,Part072,Link496,Link497]
  License = MIT-0 (Public-domain-equivalent)
  LicenseURL = https://spdx.org/licenses/MIT-0.html
  Origin = -> Origin100
  expr: Label = <<RaspberryPi_>> + <<Pico_W_AddedHeaders>>.Label + <<_STEP>>
FEATURE [App::Link] Link498  label="Pico_W_AddedHeaders_Socketed_Header_Breakaway_Left"
  LinkPlacement = pos=(0,0,8.46) rot=(0,0,1;0rad)
  LinkedObject = -> Compound035
  Placement = pos=(0,0,8.46) rot=(0,0,1;0rad)
  expr: .Placement.Base.z = <<vSocket>>.BodyHeight
  expr: Label = <<Pico_W_AddedHeaders_Socketed>>.Label + <<_>> + .LinkedObject.Label + <<_Left>>
FEATURE [App::Link] Link499  label="Pico_W_AddedHeaders_Socketed_Header_Breakaway_Right"
  LinkPlacement = pos=(17.78,0,8.46) rot=(0,0,1;0rad)
  LinkedObject = -> Compound035
  Placement = pos=(17.78,0,8.46) rot=(0,0,1;0rad)
  expr: .Placement.Base.x = <<vPico>>.BoardWidth - <<vPico>>.PinInset * 2
  expr: .Placement.Base.z = <<vSocket>>.BodyHeight
  expr: Label = <<Pico_W_AddedHeaders_Socketed>>.Label + <<_>> + .LinkedObject.Label + <<_Right>>
FEATURE [App::Part] Part073  label="RaspberryPi_Pico_W_AddedHeaders_Socketed_STEP"
  Group = -> [Group052,Part075,Link498,Link499]
  License = MIT-0 (Public-domain-equivalent)
  LicenseURL = https://spdx.org/licenses/MIT-0.html
  Origin = -> Origin103
  expr: Label = <<RaspberryPi_>> + <<Pico_W_AddedHeaders_Socketed>>.Label + <<_STEP>>
FEATURE [App::LinkElement] Array_i0
  LinkedObject = -> Body023
  _LinkOwner = 8570
FEATURE [App::LinkElement] Array_i1
  LinkPlacement = pos=(0,-2.54,0) rot=(0,0,1;0rad)
  LinkedObject = -> Body023
  Placement = pos=(0,-2.54,0) rot=(0,0,1;0rad)
  _LinkOwner = 8570
FEATURE [App::LinkElement] Array_i2
  LinkPlacement = pos=(0,-5.08,0) rot=(0,0,1;0rad)
  LinkedObject = -> Body023
  Placement = pos=(0,-5.08,0) rot=(0,0,1;0rad)
  _LinkOwner = 8570
FEATURE [App::LinkElement] Array_i3
  LinkPlacement = pos=(0,-7.62,0) rot=(0,0,1;0rad)
  LinkedObject = -> Body023
  Placement = pos=(0,-7.62,0) rot=(0,0,1;0rad)
  _LinkOwner = 8570
FEATURE [App::LinkElement] Array_i4
  LinkPlacement = pos=(0,-10.16,0) rot=(0,0,1;0rad)
  LinkedObject = -> Body023
  Placement = pos=(0,-10.16,0) rot=(0,0,1;0rad)
  _LinkOwner = 8570
FEATURE [App::LinkElement] Array_i5
  LinkPlacement = pos=(0,-12.7,0) rot=(0,0,1;0rad)
  LinkedObject = -> Body023
  Placement = pos=(0,-12.7,0) rot=(0,0,1;0rad)
  _LinkOwner = 8570
FEATURE [App::LinkElement] Array_i6
  LinkPlacement = pos=(0,-15.24,0) rot=(0,0,1;0rad)
  LinkedObject = -> Body023
  Placement = pos=(0,-15.24,0) rot=(0,0,1;0rad)
  _LinkOwner = 8570
FEATURE [App::LinkElement] Array_i7
  LinkPlacement = pos=(0,-17.78,0) rot=(0,0,1;0rad)
  LinkedObject = -> Body023
  Placement = pos=(0,-17.78,0) rot=(0,0,1;0rad)
  _LinkOwner = 8570
FEATURE [App::LinkElement] Array_i8
  LinkPlacement = pos=(0,-20.32,0) rot=(0,0,1;0rad)
  LinkedObject = -> Body023
  Placement = pos=(0,-20.32,0) rot=(0,0,1;0rad)
  _LinkOwner = 8570
FEATURE [App::LinkElement] Array_i9
  LinkPlacement = pos=(0,-22.86,0) rot=(0,0,1;0rad)
  LinkedObject = -> Body023
  Placement = pos=(0,-22.86,0) rot=(0,0,1;0rad)
  _LinkOwner = 8570
FEATURE [App::LinkElement] Array_i10
  LinkPlacement = pos=(0,-25.4,0) rot=(0,0,1;0rad)
  LinkedObject = -> Body023
  Placement = pos=(0,-25.4,0) rot=(0,0,1;0rad)
  _LinkOwner = 8570
FEATURE [App::LinkElement] Array_i11
  LinkPlacement = pos=(0,-27.94,0) rot=(0,0,1;0rad)
  LinkedObject = -> Body023
  Placement = pos=(0,-27.94,0) rot=(0,0,1;0rad)
  _LinkOwner = 8570
FEATURE [App::LinkElement] Array_i12
  LinkPlacement = pos=(0,-30.48,0) rot=(0,0,1;0rad)
  LinkedObject = -> Body023
  Placement = pos=(0,-30.48,0) rot=(0,0,1;0rad)
  _LinkOwner = 8570
FEATURE [App::LinkElement] Array_i13
  LinkPlacement = pos=(0,-33.02,0) rot=(0,0,1;0rad)
  LinkedObject = -> Body023
  Placement = pos=(0,-33.02,0) rot=(0,0,1;0rad)
  _LinkOwner = 8570
FEATURE [App::LinkElement] Array_i14
  LinkPlacement = pos=(0,-35.56,0) rot=(0,0,1;0rad)
  LinkedObject = -> Body023
  Placement = pos=(0,-35.56,0) rot=(0,0,1;0rad)
  _LinkOwner = 8570
FEATURE [App::LinkElement] Array_i15
  LinkPlacement = pos=(0,-38.1,0) rot=(0,0,1;0rad)
  LinkedObject = -> Body023
  Placement = pos=(0,-38.1,0) rot=(0,0,1;0rad)
  _LinkOwner = 8570
FEATURE [App::LinkElement] Array_i16
  LinkPlacement = pos=(0,-40.64,0) rot=(0,0,1;0rad)
  LinkedObject = -> Body023
  Placement = pos=(0,-40.64,0) rot=(0,0,1;0rad)
  _LinkOwner = 8570
FEATURE [App::LinkElement] Array_i17
  LinkPlacement = pos=(0,-43.18,0) rot=(0,0,1;0rad)
  LinkedObject = -> Body023
  Placement = pos=(0,-43.18,0) rot=(0,0,1;0rad)
  _LinkOwner = 8570
FEATURE [App::LinkElement] Array_i18
  LinkPlacement = pos=(0,-45.72,0) rot=(0,0,1;0rad)
  LinkedObject = -> Body023
  Placement = pos=(0,-45.72,0) rot=(0,0,1;0rad)
  _LinkOwner = 8570
FEATURE [App::LinkElement] Array_i19
  LinkPlacement = pos=(0,-48.26,0) rot=(0,0,1;0rad)
  LinkedObject = -> Body023
  Placement = pos=(0,-48.26,0) rot=(0,0,1;0rad)
  _LinkOwner = 8570
FEATURE [Part::Compound] Compound034  label="Socket"
  Links = -> [Body002,Array_i0,Array_i1,Array_i2,Array_i3,Array_i4,Array_i5,Array_i6,Array_i7,Array_i8,Array_i9,Array_i10,Array_i11,Array_i12,Array_i13,Array_i14,Array_i15,Array_i16,Array_i17,Array_i18,Array_i19]
FEATURE [App::LinkElement] Array001_i0
  LinkedObject = -> Body022
  _LinkOwner = 8592
FEATURE [App::LinkElement] Array001_i1
  LinkPlacement = pos=(0,-2.54,0) rot=(0,0,1;0rad)
  LinkedObject = -> Body022
  Placement = pos=(0,-2.54,0) rot=(0,0,1;0rad)
  _LinkOwner = 8592
FEATURE [App::LinkElement] Array001_i2
  LinkPlacement = pos=(0,-5.08,0) rot=(0,0,1;0rad)
  LinkedObject = -> Body022
  Placement = pos=(0,-5.08,0) rot=(0,0,1;0rad)
  _LinkOwner = 8592
FEATURE [App::LinkElement] Array001_i3
  LinkPlacement = pos=(0,-7.62,0) rot=(0,0,1;0rad)
  LinkedObject = -> Body022
  Placement = pos=(0,-7.62,0) rot=(0,0,1;0rad)
  _LinkOwner = 8592
FEATURE [App::LinkElement] Array001_i4
  LinkPlacement = pos=(0,-10.16,0) rot=(0,0,1;0rad)
  LinkedObject = -> Body022
  Placement = pos=(0,-10.16,0) rot=(0,0,1;0rad)
  _LinkOwner = 8592
FEATURE [App::LinkElement] Array001_i5
  LinkPlacement = pos=(0,-12.7,0) rot=(0,0,1;0rad)
  LinkedObject = -> Body022
  Placement = pos=(0,-12.7,0) rot=(0,0,1;0rad)
  _LinkOwner = 8592
FEATURE [App::LinkElement] Array001_i6
  LinkPlacement = pos=(0,-15.24,0) rot=(0,0,1;0rad)
  LinkedObject = -> Body022
  Placement = pos=(0,-15.24,0) rot=(0,0,1;0rad)
  _LinkOwner = 8592
FEATURE [App::LinkElement] Array001_i7
  LinkPlacement = pos=(0,-17.78,0) rot=(0,0,1;0rad)
  LinkedObject = -> Body022
  Placement = pos=(0,-17.78,0) rot=(0,0,1;0rad)
  _LinkOwner = 8592
FEATURE [App::LinkElement] Array001_i8
  LinkPlacement = pos=(0,-20.32,0) rot=(0,0,1;0rad)
  LinkedObject = -> Body022
  Placement = pos=(0,-20.32,0) rot=(0,0,1;0rad)
  _LinkOwner = 8592
FEATURE [App::LinkElement] Array001_i9
  LinkPlacement = pos=(0,-22.86,0) rot=(0,0,1;0rad)
  LinkedObject = -> Body022
  Placement = pos=(0,-22.86,0) rot=(0,0,1;0rad)
  _LinkOwner = 8592
FEATURE [App::LinkElement] Array001_i10
  LinkPlacement = pos=(0,-25.4,0) rot=(0,0,1;0rad)
  LinkedObject = -> Body022
  Placement = pos=(0,-25.4,0) rot=(0,0,1;0rad)
  _LinkOwner = 8592
FEATURE [App::LinkElement] Array001_i11
  LinkPlacement = pos=(0,-27.94,0) rot=(0,0,1;0rad)
  LinkedObject = -> Body022
  Placement = pos=(0,-27.94,0) rot=(0,0,1;0rad)
  _LinkOwner = 8592
FEATURE [App::LinkElement] Array001_i12
  LinkPlacement = pos=(0,-30.48,0) rot=(0,0,1;0rad)
  LinkedObject = -> Body022
  Placement = pos=(0,-30.48,0) rot=(0,0,1;0rad)
  _LinkOwner = 8592
FEATURE [App::LinkElement] Array001_i13
  LinkPlacement = pos=(0,-33.02,0) rot=(0,0,1;0rad)
  LinkedObject = -> Body022
  Placement = pos=(0,-33.02,0) rot=(0,0,1;0rad)
  _LinkOwner = 8592
FEATURE [App::LinkElement] Array001_i14
  LinkPlacement = pos=(0,-35.56,0) rot=(0,0,1;0rad)
  LinkedObject = -> Body022
  Placement = pos=(0,-35.56,0) rot=(0,0,1;0rad)
  _LinkOwner = 8592
FEATURE [App::LinkElement] Array001_i15
  LinkPlacement = pos=(0,-38.1,0) rot=(0,0,1;0rad)
  LinkedObject = -> Body022
  Placement = pos=(0,-38.1,0) rot=(0,0,1;0rad)
  _LinkOwner = 8592
FEATURE [App::LinkElement] Array001_i16
  LinkPlacement = pos=(0,-40.64,0) rot=(0,0,1;0rad)
  LinkedObject = -> Body022
  Placement = pos=(0,-40.64,0) rot=(0,0,1;0rad)
  _LinkOwner = 8592
FEATURE [App::LinkElement] Array001_i17
  LinkPlacement = pos=(0,-43.18,0) rot=(0,0,1;0rad)
  LinkedObject = -> Body022
  Placement = pos=(0,-43.18,0) rot=(0,0,1;0rad)
  _LinkOwner = 8592
FEATURE [App::LinkElement] Array001_i18
  LinkPlacement = pos=(0,-45.72,0) rot=(0,0,1;0rad)
  LinkedObject = -> Body022
  Placement = pos=(0,-45.72,0) rot=(0,0,1;0rad)
  _LinkOwner = 8592
FEATURE [App::LinkElement] Array001_i19
  LinkPlacement = pos=(0,-48.26,0) rot=(0,0,1;0rad)
  LinkedObject = -> Body022
  Placement = pos=(0,-48.26,0) rot=(0,0,1;0rad)
  _LinkOwner = 8592
FEATURE [App::LinkElement] Array001_i20
  LinkPlacement = pos=(17.78,0,0) rot=(0,0,1;0rad)
  LinkedObject = -> Body022
  Placement = pos=(17.78,0,0) rot=(0,0,1;0rad)
  _LinkOwner = 8592
FEATURE [App::LinkElement] Array001_i21
  LinkPlacement = pos=(17.78,-2.54,0) rot=(0,0,1;0rad)
  LinkedObject = -> Body022
  Placement = pos=(17.78,-2.54,0) rot=(0,0,1;0rad)
  _LinkOwner = 8592
FEATURE [App::LinkElement] Array001_i22
  LinkPlacement = pos=(17.78,-5.08,0) rot=(0,0,1;0rad)
  LinkedObject = -> Body022
  Placement = pos=(17.78,-5.08,0) rot=(0,0,1;0rad)
  _LinkOwner = 8592
FEATURE [App::LinkElement] Array001_i23
  LinkPlacement = pos=(17.78,-7.62,0) rot=(0,0,1;0rad)
  LinkedObject = -> Body022
  Placement = pos=(17.78,-7.62,0) rot=(0,0,1;0rad)
  _LinkOwner = 8592
FEATURE [App::LinkElement] Array001_i24
  LinkPlacement = pos=(17.78,-10.16,0) rot=(0,0,1;0rad)
  LinkedObject = -> Body022
  Placement = pos=(17.78,-10.16,0) rot=(0,0,1;0rad)
  _LinkOwner = 8592
FEATURE [App::LinkElement] Array001_i25
  LinkPlacement = pos=(17.78,-12.7,0) rot=(0,0,1;0rad)
  LinkedObject = -> Body022
  Placement = pos=(17.78,-12.7,0) rot=(0,0,1;0rad)
  _LinkOwner = 8592
FEATURE [App::LinkElement] Array001_i26
  LinkPlacement = pos=(17.78,-15.24,0) rot=(0,0,1;0rad)
  LinkedObject = -> Body022
  Placement = pos=(17.78,-15.24,0) rot=(0,0,1;0rad)
  _LinkOwner = 8592
FEATURE [App::LinkElement] Array001_i27
  LinkPlacement = pos=(17.78,-17.78,0) rot=(0,0,1;0rad)
  LinkedObject = -> Body022
  Placement = pos=(17.78,-17.78,0) rot=(0,0,1;0rad)
  _LinkOwner = 8592
FEATURE [App::LinkElement] Array001_i28
  LinkPlacement = pos=(17.78,-20.32,0) rot=(0,0,1;0rad)
  LinkedObject = -> Body022
  Placement = pos=(17.78,-20.32,0) rot=(0,0,1;0rad)
  _LinkOwner = 8592
FEATURE [App::LinkElement] Array001_i29
  LinkPlacement = pos=(17.78,-22.86,0) rot=(0,0,1;0rad)
  LinkedObject = -> Body022
  Placement = pos=(17.78,-22.86,0) rot=(0,0,1;0rad)
  _LinkOwner = 8592
FEATURE [App::LinkElement] Array001_i30
  LinkPlacement = pos=(17.78,-25.4,0) rot=(0,0,1;0rad)
  LinkedObject = -> Body022
  Placement = pos=(17.78,-25.4,0) rot=(0,0,1;0rad)
  _LinkOwner = 8592
FEATURE [App::LinkElement] Array001_i31
  LinkPlacement = pos=(17.78,-27.94,0) rot=(0,0,1;0rad)
  LinkedObject = -> Body022
  Placement = pos=(17.78,-27.94,0) rot=(0,0,1;0rad)
  _LinkOwner = 8592
FEATURE [App::LinkElement] Array001_i32
  LinkPlacement = pos=(17.78,-30.48,0) rot=(0,0,1;0rad)
  LinkedObject = -> Body022
  Placement = pos=(17.78,-30.48,0) rot=(0,0,1;0rad)
  _LinkOwner = 8592
FEATURE [App::LinkElement] Array001_i33
  LinkPlacement = pos=(17.78,-33.02,0) rot=(0,0,1;0rad)
  LinkedObject = -> Body022
  Placement = pos=(17.78,-33.02,0) rot=(0,0,1;0rad)
  _LinkOwner = 8592
FEATURE [App::LinkElement] Array001_i34
  LinkPlacement = pos=(17.78,-35.56,0) rot=(0,0,1;0rad)
  LinkedObject = -> Body022
  Placement = pos=(17.78,-35.56,0) rot=(0,0,1;0rad)
  _LinkOwner = 8592
FEATURE [App::LinkElement] Array001_i35
  LinkPlacement = pos=(17.78,-38.1,0) rot=(0,0,1;0rad)
  LinkedObject = -> Body022
  Placement = pos=(17.78,-38.1,0) rot=(0,0,1;0rad)
  _LinkOwner = 8592
FEATURE [App::LinkElement] Array001_i36
  LinkPlacement = pos=(17.78,-40.64,0) rot=(0,0,1;0rad)
  LinkedObject = -> Body022
  Placement = pos=(17.78,-40.64,0) rot=(0,0,1;0rad)
  _LinkOwner = 8592
FEATURE [App::LinkElement] Array001_i37
  LinkPlacement = pos=(17.78,-43.18,0) rot=(0,0,1;0rad)
  LinkedObject = -> Body022
  Placement = pos=(17.78,-43.18,0) rot=(0,0,1;0rad)
  _LinkOwner = 8592
FEATURE [App::LinkElement] Array001_i38
  LinkPlacement = pos=(17.78,-45.72,0) rot=(0,0,1;0rad)
  LinkedObject = -> Body022
  Placement = pos=(17.78,-45.72,0) rot=(0,0,1;0rad)
  _LinkOwner = 8592
FEATURE [App::LinkElement] Array001_i39
  LinkPlacement = pos=(17.78,-48.26,0) rot=(0,0,1;0rad)
  LinkedObject = -> Body022
  Placement = pos=(17.78,-48.26,0) rot=(0,0,1;0rad)
  _LinkOwner = 8592
FEATURE [Part::Compound] Compound033  label="DIP-40_W17.78mm_Header"
  Links = -> [Body,Array001_i0,Array001_i1,Array001_i2,Array001_i3,Array001_i4,Array001_i5,Array001_i6,Array001_i7,Array001_i8,Array001_i9,Array001_i10,Array001_i11,Array001_i12,Array001_i13,Array001_i14,Array001_i15,Array001_i16,Array001_i17,Array001_i18,Array001_i19,Array001_i20,Array001_i21,Array001_i22,Array001_i23,Array001_i24,Array001_i25,Array001_i26,Array001_i27,Array001_i28,Array001_i29,Array001_i30,+9 more]
FEATURE [Sketcher::SketchObject] Sketch113  label="Sketch_Header_Pin"
  AttachmentOffset = pos=(-8.89,24.13,0) rot=(0,0,1;0rad)
  FullyConstrained = true
  MapMode = 5
  Placement = pos=(-8.89,24.13,0) rot=(0,0,1;0rad)
  Support = -> [XY_Plane088]
  expr: .AttachmentOffset.Base.x = -(<<vPico>>.BoardWidth / 2 - <<vPico>>.PinInset)
  expr: .AttachmentOffset.Base.y = (<<vPico>>.PinDIPCount / 4 - 0.5) * <<vPico>>.PinPitch
  expr: .Placement.Base.x = -(<<vPico>>.BoardWidth / 2 - <<vPico>>.PinInset)
  expr: .Placement.Base.y = (<<vPico>>.PinDIPCount / 4 - 0.5) * <<vPico>>.PinPitch
  expr: Constraints[5] = <<vHeader>>.PinWidth
  sketch-geometry (5):
    g0: LineSegment StartX=0.3175 StartY=0.3175 StartZ=0 EndX=-0.3175 EndY=0.3175 EndZ=0
    g1: LineSegment StartX=-0.3175 StartY=0.3175 StartZ=0 EndX=-0.3175 EndY=-0.3175 EndZ=0
    g2: LineSegment StartX=-0.3175 StartY=-0.3175 StartZ=0 EndX=0.3175 EndY=-0.3175 EndZ=0
    g3: LineSegment StartX=0.3175 StartY=-0.3175 StartZ=0 EndX=0.3175 EndY=0.3175 EndZ=0
    g4: GeomPoint X=0 Y=0 Z=0
  constraints (12):
    c: Coincident(g0,g1)
    c: Coincident(g1,g2)
    c: Coincident(g2,g3)
    c: Coincident(g3,g0)
    c: Equal(g0,g3)
    c: Distance(g0) = 0.635
    c: Parallel(g0,g2)
    c: Parallel(g3,g1)
    c: Perpendicular(g3,g0)
    c: Vertical(g3)
    c: Symmetric(g1,g0,g4)
    c: Coincident(g4,g-1)
FEATURE [PartDesign::Pad] Pad116  label="Pad_Header_Pin"
  Direction = (0,0,1)
  Length = 4.175
  Length2 = 6.35
  Profile = -> Sketch113
  ReferenceAxis = -> Sketch113 [N_Axis]
  Type = 4
  expr: Length = <<vHeader>>.PinLength - <<vHeader>>.PinInterfaceLength
  expr: Length2 = <<vHeader>>.PinInterfaceLength
FEATURE [PartDesign::Chamfer] Chamfer002  label="Chamfer_Header_Pin"
  Angle = 45
  Base = -> Pad116 [Face6,Face5]
  BaseFeature = -> Pad116
  ChamferType = 1
  FlipDirection = false
  Size = 0.15875
  Size2 = 0.635
  SupportTransform = false
  UseAllEdges = false
  expr: Size = (<<vHeader>>.PinWidth - <<vHeader>>.PinBaseWidth) / 2
  expr: Size2 = <<vHeader>>.PinTipLength
FEATURE [PartDesign::Body] Body022  label="Header_Pin"
  Group = -> [Sketch113,Pad116,Chamfer002]
  Origin = -> Origin088
  Tip = -> Chamfer002
FEATURE [Part::FeaturePython] Array001  label="Header_Pins"  # Draft array (typed FeaturePython)
  AlwaysSyncPlacement = false
  Angle = 360
  ArrayType = 0
  Axis = (0,0,1)
  Base = -> Body022
  Center = (0,0,0)
  Count = 40
  ElementList = -> [Array001_i0,Array001_i1,Array001_i2,Array001_i3,Array001_i4,Array001_i5,Array001_i6,Array001_i7,Array001_i8,Array001_i9,Array001_i10,Array001_i11,Array001_i12,Array001_i13,Array001_i14,Array001_i15,Array001_i16,Array001_i17,Array001_i18,Array001_i19,Array001_i20,Array001_i21,Array001_i22,Array001_i23,Array001_i24,Array001_i25,Array001_i26,Array001_i27,Array001_i28,Array001_i29,Array001_i30,+9 more]
  ExpandArray = true
  Fuse = false
  IntervalAxis = (0,0,0)
  IntervalX = (17.78,0,0)
  IntervalY = (0,-2.54,0)
  IntervalZ = (0,0,0)
  NumberCircles = 3
  NumberPolar = 5
  NumberX = 2
  NumberY = 20
  NumberZ = 1
  RadialDistance = 50
  Symmetry = 1
  TangentialDistance = 25
  expr: .IntervalX.x = <<vPico>>.BoardWidth - <<vPico>>.PinInset * 2
  expr: .IntervalY.y = -<<vPico>>.PinPitch
  expr: NumberY = <<vPico>>.PinDIPCount / 2
FEATURE [App::Part] Part001  label="Header_DIP_Source"
  Group = -> [Spreadsheet002,Body022,Array001,Body,Array001_i17,Array001_i19,Array001_i21,Array001_i24,Array001_i16,Array001_i26,Array001_i20,Array001_i25,Array001_i18,Array001_i22,Array001_i23,Array001_i27,Array001_i29,Array001_i32,Array001_i37,Array001_i33,Array001_i35,Array001_i34,Array001_i28,Array001_i30,Array001_i31,Array001_i36,Array001_i38,Array001_i39,Array001_i3,Array001_i1,Array001_i8,Array001_i2,+13 more]
  License = MIT-0 (Public-domain-equivalent)
  LicenseURL = https://spdx.org/licenses/MIT-0.html
  Origin = -> Origin006
FEATURE [Sketcher::SketchObject] Sketch115  label="Sketch_Socket_Pin"
  AttachmentOffset = pos=(24.13,0,-8.89) rot=(0,0,1;0rad)
  FullyConstrained = true
  MapMode = 5
  Placement = pos=(-8.89,24.13,-7.3e-15) rot=(0.57735,0.57735,0.57735;2.0944rad)
  Support = -> [YZ_Plane089]
  expr: .AttachmentOffset.Base.x = (<<vPico>>.PinDIPCount / 4 - 0.5) * <<vPico>>.PinPitch
  expr: .AttachmentOffset.Base.z = -(<<vPico>>.BoardWidth / 2 - <<vPico>>.PinInset)
  expr: Constraints[10] = <<vSocket>>.PinWidth
  expr: Constraints[11] = <<vSocket>>.PinBaseWidth
  expr: Constraints[12] = <<vSocket>>.PinBaseHeight
  expr: Constraints[13] = <<vSocket>>.PinLength
  expr: Constraints[14] = (<<vSocket>>.StandoffDepth + <<vSocket>>.BodyHeight - <<vSocket>>.InsertionDepth) / 2
  sketch-geometry (6):
    g0: LineSegment StartX=-0.3175 StartY=1.3725 StartZ=0 EndX=-0.3175 EndY=-2.8575 EndZ=0
    g1: LineSegment StartX=-0.3175 StartY=-2.8575 StartZ=0 EndX=-0.15875 EndY=-3.175 EndZ=0
    g2: LineSegment StartX=-0.15875 StartY=-3.175 StartZ=0 EndX=0.15875 EndY=-3.175 EndZ=0
    g3: LineSegment StartX=0.15875 StartY=-3.175 StartZ=0 EndX=0.3175 EndY=-2.8575 EndZ=0
    g4: LineSegment StartX=0.3175 StartY=-2.8575 StartZ=0 EndX=0.3175 EndY=1.3725 EndZ=0
    g5: LineSegment StartX=0.3175 StartY=1.3725 StartZ=0 EndX=-0.3175 EndY=1.3725 EndZ=0
  constraints (15):
    c: Coincident(g1,g0)
    c: Coincident(g2,g1)
    c: Coincident(g3,g2)
    c: Coincident(g4,g3)
    c: Coincident(g5,g4)
    c: Coincident(g5,g0)
    c: Vertical(g0)
    c: Symmetric(g0,g4,g-2)
    c: Symmetric(g0,g3,g-2)
    c: Symmetric(g1,g2,g-2)
    c: Distance(g5) = 0.635
    c: Distance(g2) = 0.3175
    c: Distance(g3,g2) = 0.3175
    c: Distance(g-1,g2) = 3.175
    c: Distance(g4,g-1) = 1.3725
FEATURE [PartDesign::Pad] Pad118  label="Pad_Socket_Pin"
  Direction = (1,-2e-16,3e-16)
  Length = 0.4
  Length2 = 10
  Midplane = true
  Placement = pos=(0,0,0) rot=(0.57735,0.57735,0.57735;2.0944rad)
  Profile = -> Sketch115
  ReferenceAxis = -> Sketch115 [N_Axis]
  Type = 0
  expr: Length = <<vSocket>>.PinThickness
FEATURE [PartDesign::Body] Body023  label="Socket_Pin"
  Group = -> [Sketch115,Pad118]
  Origin = -> Origin089
  Tip = -> Pad118
FEATURE [Part::FeaturePython] Array  label="Socket_Pins"  # Draft array (typed FeaturePython)
  AlwaysSyncPlacement = false
  Angle = 360
  ArrayType = 0
  Axis = (0,0,1)
  Base = -> Body023
  Center = (0,0,0)
  Count = 20
  ElementList = -> [Array_i0,Array_i1,Array_i2,Array_i3,Array_i4,Array_i5,Array_i6,Array_i7,Array_i8,Array_i9,Array_i10,Array_i11,Array_i12,Array_i13,Array_i14,Array_i15,Array_i16,Array_i17,Array_i18,Array_i19]
  ExpandArray = true
  Fuse = false
  IntervalAxis = (0,0,0)
  IntervalX = (0,0,0)
  IntervalY = (0,-2.54,0)
  IntervalZ = (0,0,0)
  NumberCircles = 3
  NumberPolar = 5
  NumberX = 1
  NumberY = 20
  NumberZ = 1
  RadialDistance = 50
  Symmetry = 1
  TangentialDistance = 25
  expr: .IntervalY.y = -<<vPico>>.PinPitch
  expr: NumberY = <<vPico>>.PinDIPCount / 2
FEATURE [App::Part] Part  label="Socket_Source"
  Group = -> [Spreadsheet003,Body023,Array,Body002,Array_i12,Array_i10,Array_i16,Array_i8,Array_i11,Array_i7,Array_i15,Array_i9,Array_i13,Array_i14,Array_i17,Array_i19,Array_i18,Array_i0,Array_i1,Array_i2,Array_i3,Array_i4,Array_i5,Array_i6,Compound034]
  License = MIT-0 (Public-domain-equivalent)
  LicenseURL = https://spdx.org/licenses/MIT-0.html
  Origin = -> Origin
FEATURE [App::LinkElement] Array002_i0
  LinkedObject = -> Body026
  _LinkOwner = 8675
FEATURE [App::LinkElement] Array002_i1
  LinkPlacement = pos=(0,-2.54,0) rot=(0,0,1;0rad)
  LinkedObject = -> Body026
  Placement = pos=(0,-2.54,0) rot=(0,0,1;0rad)
  _LinkOwner = 8675
FEATURE [App::LinkElement] Array002_i2
  LinkPlacement = pos=(0,-5.08,0) rot=(0,0,1;0rad)
  LinkedObject = -> Body026
  Placement = pos=(0,-5.08,0) rot=(0,0,1;0rad)
  _LinkOwner = 8675
FEATURE [App::LinkElement] Array002_i3
  LinkPlacement = pos=(0,-7.62,0) rot=(0,0,1;0rad)
  LinkedObject = -> Body026
  Placement = pos=(0,-7.62,0) rot=(0,0,1;0rad)
  _LinkOwner = 8675
FEATURE [App::LinkElement] Array002_i4
  LinkPlacement = pos=(0,-10.16,0) rot=(0,0,1;0rad)
  LinkedObject = -> Body026
  Placement = pos=(0,-10.16,0) rot=(0,0,1;0rad)
  _LinkOwner = 8675
FEATURE [App::LinkElement] Array002_i5
  LinkPlacement = pos=(0,-12.7,0) rot=(0,0,1;0rad)
  LinkedObject = -> Body026
  Placement = pos=(0,-12.7,0) rot=(0,0,1;0rad)
  _LinkOwner = 8675
FEATURE [App::LinkElement] Array002_i6
  LinkPlacement = pos=(0,-15.24,0) rot=(0,0,1;0rad)
  LinkedObject = -> Body026
  Placement = pos=(0,-15.24,0) rot=(0,0,1;0rad)
  _LinkOwner = 8675
FEATURE [App::LinkElement] Array002_i7
  LinkPlacement = pos=(0,-17.78,0) rot=(0,0,1;0rad)
  LinkedObject = -> Body026
  Placement = pos=(0,-17.78,0) rot=(0,0,1;0rad)
  _LinkOwner = 8675
FEATURE [App::LinkElement] Array002_i8
  LinkPlacement = pos=(0,-20.32,0) rot=(0,0,1;0rad)
  LinkedObject = -> Body026
  Placement = pos=(0,-20.32,0) rot=(0,0,1;0rad)
  _LinkOwner = 8675
FEATURE [App::LinkElement] Array002_i9
  LinkPlacement = pos=(0,-22.86,0) rot=(0,0,1;0rad)
  LinkedObject = -> Body026
  Placement = pos=(0,-22.86,0) rot=(0,0,1;0rad)
  _LinkOwner = 8675
FEATURE [App::LinkElement] Array002_i10
  LinkPlacement = pos=(0,-25.4,0) rot=(0,0,1;0rad)
  LinkedObject = -> Body026
  Placement = pos=(0,-25.4,0) rot=(0,0,1;0rad)
  _LinkOwner = 8675
FEATURE [App::LinkElement] Array002_i11
  LinkPlacement = pos=(0,-27.94,0) rot=(0,0,1;0rad)
  LinkedObject = -> Body026
  Placement = pos=(0,-27.94,0) rot=(0,0,1;0rad)
  _LinkOwner = 8675
FEATURE [App::LinkElement] Array002_i12
  LinkPlacement = pos=(0,-30.48,0) rot=(0,0,1;0rad)
  LinkedObject = -> Body026
  Placement = pos=(0,-30.48,0) rot=(0,0,1;0rad)
  _LinkOwner = 8675
FEATURE [App::LinkElement] Array002_i13
  LinkPlacement = pos=(0,-33.02,0) rot=(0,0,1;0rad)
  LinkedObject = -> Body026
  Placement = pos=(0,-33.02,0) rot=(0,0,1;0rad)
  _LinkOwner = 8675
FEATURE [App::LinkElement] Array002_i14
  LinkPlacement = pos=(0,-35.56,0) rot=(0,0,1;0rad)
  LinkedObject = -> Body026
  Placement = pos=(0,-35.56,0) rot=(0,0,1;0rad)
  _LinkOwner = 8675
FEATURE [App::LinkElement] Array002_i15
  LinkPlacement = pos=(0,-38.1,0) rot=(0,0,1;0rad)
  LinkedObject = -> Body026
  Placement = pos=(0,-38.1,0) rot=(0,0,1;0rad)
  _LinkOwner = 8675
FEATURE [App::LinkElement] Array002_i16
  LinkPlacement = pos=(0,-40.64,0) rot=(0,0,1;0rad)
  LinkedObject = -> Body026
  Placement = pos=(0,-40.64,0) rot=(0,0,1;0rad)
  _LinkOwner = 8675
FEATURE [App::LinkElement] Array002_i17
  LinkPlacement = pos=(0,-43.18,0) rot=(0,0,1;0rad)
  LinkedObject = -> Body026
  Placement = pos=(0,-43.18,0) rot=(0,0,1;0rad)
  _LinkOwner = 8675
FEATURE [App::LinkElement] Array002_i18
  LinkPlacement = pos=(0,-45.72,0) rot=(0,0,1;0rad)
  LinkedObject = -> Body026
  Placement = pos=(0,-45.72,0) rot=(0,0,1;0rad)
  _LinkOwner = 8675
FEATURE [App::LinkElement] Array002_i19
  LinkPlacement = pos=(0,-48.26,0) rot=(0,0,1;0rad)
  LinkedObject = -> Body026
  Placement = pos=(0,-48.26,0) rot=(0,0,1;0rad)
  _LinkOwner = 8675
FEATURE [Part::Compound] Compound035  label="Header_Breakaway"
  Links = -> [Body024,Array002_i0,Array002_i1,Array002_i2,Array002_i3,Array002_i4,Array002_i5,Array002_i6,Array002_i7,Array002_i8,Array002_i9,Array002_i10,Array002_i11,Array002_i12,Array002_i13,Array002_i14,Array002_i15,Array002_i16,Array002_i17,Array002_i18,Array002_i19]
FEATURE [Part::FeaturePython] Array002  label="Header_Breakaway_Pins"  # Draft array (typed FeaturePython)
  AlwaysSyncPlacement = false
  Angle = 360
  ArrayType = 0
  Axis = (0,0,1)
  Base = -> Body026
  Center = (0,0,0)
  Count = 20
  ElementList = -> [Array002_i0,Array002_i1,Array002_i2,Array002_i3,Array002_i4,Array002_i5,Array002_i6,Array002_i7,Array002_i8,Array002_i9,Array002_i10,Array002_i11,Array002_i12,Array002_i13,Array002_i14,Array002_i15,Array002_i16,Array002_i17,Array002_i18,Array002_i19]
  ExpandArray = true
  Fuse = false
  IntervalAxis = (0,0,0)
  IntervalX = (0,0,0)
  IntervalY = (0,-2.54,0)
  IntervalZ = (0,0,0)
  NumberCircles = 3
  NumberPolar = 5
  NumberX = 1
  NumberY = 20
  NumberZ = 1
  RadialDistance = 50
  Symmetry = 1
  TangentialDistance = 25
  expr: .IntervalY.y = -<<vPico>>.PinPitch
  expr: Label = <<vHeaderBreakaway>>.PartName + <<_>> + <<vHeaderBreakaway>>.PinBodyName + <<s>>
  expr: NumberY = <<vPico>>.PinDIPCount / 2
FEATURE [App::Part] Part063  label="Header_Breakaway_Source"
  Group = -> [Spreadsheet,Body026,Array002,Array002_i1,Array002_i4,Array002_i0,Array002_i2,Array002_i3,Array002_i5,Body024,Array002_i13,Array002_i9,Array002_i11,Array002_i7,Array002_i8,Array002_i6,Array002_i10,Array002_i12,Array002_i15,Array002_i14,Array002_i17,Array002_i16,Array002_i18,Array002_i19,Compound035]
  Origin = -> Origin090
  expr: Label = <<vHeaderBreakaway>>.PartName + <<_Source>>
FEATURE [App::DocumentObjectGroup] Group  label="Parametric_Source"
  Group = -> [Part020,Part003,Part001,Part,Part063]
FEATURE [Part::FeaturePython] Clone  label="DIP-40_W17.78mm_H8.51mm_Socket"  # Draft clone (typed FeaturePython)
  AttacherType = Attacher::AttachEngine3D
  Fuse = false
  Objects = -> [Compound022]
  Scale = (1,1,1)
FEATURE [Part::FeaturePython] Clone001  label="RaspberryPi_Pico"  # Draft clone (typed FeaturePython)
  AttacherType = Attacher::AttachEngine3D
  Fuse = false
  Objects = -> [Compound023]
  Scale = (1,1,1)
FEATURE [Part::FeaturePython] Clone002  label="RaspberryPi_Pico_AddedHeaders"  # Draft clone (typed FeaturePython)
  AttacherType = Attacher::AttachEngine3D
  Fuse = false
  Objects = -> [Compound029]
  Scale = (1,1,1)
FEATURE [Part::FeaturePython] Clone003  label="RaspberryPi_Pico_AddedHeaders_Socketed"  # Draft clone (typed FeaturePython)
  AttacherType = Attacher::AttachEngine3D
  Fuse = false
  Objects = -> [Compound030]
  Scale = (1,1,1)
FEATURE [Part::FeaturePython] Clone004  label="RaspberryPi_Pico_H"  # Draft clone (typed FeaturePython)
  AttacherType = Attacher::AttachEngine3D
  Fuse = false
  Objects = -> [Compound024]
  Scale = (1,1,1)
FEATURE [Part::FeaturePython] Clone005  label="RaspberryPi_Pico_H_Socketed"  # Draft clone (typed FeaturePython)
  AttacherType = Attacher::AttachEngine3D
  Fuse = false
  Objects = -> [Compound025]
  Scale = (1,1,1)
FEATURE [Part::FeaturePython] Clone006  label="RaspberryPi_Pico_W"  # Draft clone (typed FeaturePython)
  AttacherType = Attacher::AttachEngine3D
  Fuse = false
  Objects = -> [Compound026]
  Scale = (1,1,1)
FEATURE [Part::FeaturePython] Clone007  label="RaspberryPi_Pico_W_AddedHeaders"  # Draft clone (typed FeaturePython)
  AttacherType = Attacher::AttachEngine3D
  Fuse = false
  Objects = -> [Compound031]
  Scale = (1,1,1)
FEATURE [Part::FeaturePython] Clone008  label="RaspberryPi_Pico_W_AddedHeaders_Socketed"  # Draft clone (typed FeaturePython)
  AttacherType = Attacher::AttachEngine3D
  Fuse = false
  Objects = -> [Compound032]
  Scale = (1,1,1)
FEATURE [Part::FeaturePython] Clone009  label="RaspberryPi_Pico_WH"  # Draft clone (typed FeaturePython)
  AttacherType = Attacher::AttachEngine3D
  Fuse = false
  Objects = -> [Compound027]
  Scale = (1,1,1)
FEATURE [Part::FeaturePython] Clone010  label="RaspberryPi_Pico_WH_Socketed"  # Draft clone (typed FeaturePython)
  AttacherType = Attacher::AttachEngine3D
  Fuse = false
  Objects = -> [Compound028]
  Scale = (1,1,1)
FEATURE [App::DocumentObjectGroup] Group054  label="PinSocket"
FEATURE [App::Link] Link500  label="PinSocket_1x20"
  LinkPlacement = pos=(8.89,-24.13,0) rot=(0,0,1;0rad)
  LinkedObject = -> Compound034
  Placement = pos=(8.89,-24.13,0) rot=(0,0,1;0rad)
  expr: .Placement.Base.x = <<vPico>>.BoardWidth / 2 - <<vPico>>.PinInset
  expr: .Placement.Base.y = -<<vPico>>.PinPitch * (<<vPico>>.PinDIPCount / 4 - 0.5)
  expr: Label = <<PinSocket>>.Label + <<_1x20>>
FEATURE [App::Part] Part076  label="PinSocket_1x20_H8.51mm_P2.54mm_Vertical_STEP"
  Group = -> [Group054,Link500]
  Origin = -> Origin106
FEATURE [App::DocumentObjectGroup] Group036  label="STEP Assembly (for built-in export to preserve hierarchy naming)"
  Group = -> [Part048,Part024,Part064,Part067,Part049,Part052,Part055,Part070,Part073,Part057,Part060,Part076]
FEATURE [App::Link] Link501  label="PinSocket_1x021"
  LinkTransform = true
  LinkedObject = -> Link500
FEATURE [Part::Compound] Compound036  label="PinSocket_1x20_H8.51mm_P2.54mm_Vertical_Compound"
  Links = -> [Link501]
FEATURE [App::DocumentObjectGroup] Group048  label="STEP - Parametrically Coloured Compounds"
  Group = -> [Compound022,Compound023,Compound029,Compound030,Compound024,Compound025,Compound026,Compound031,Compound032,Compound027,Compound028,Compound036]
FEATURE [Part::FeaturePython] Clone011  label="PinSocket_1x20_H8.51mm_P2.54mm_Vertical"  # Draft clone (typed FeaturePython)
  AttacherType = Attacher::AttachEngine3D
  Fuse = false
  Objects = -> [Compound036]
  Scale = (1,1,1)
FEATURE [App::DocumentObjectGroup] Group053  label="VRML - Manually Coloured Clones (using KiCad StepUp colours)"
  Group = -> [Clone,Clone001,Clone002,Clone003,Clone004,Clone005,Clone006,Clone007,Clone008,Clone009,Clone010,Clone011]
FEATURE [App::DocumentObjectGroup] Group037  label="KiCad Model Outputs (ignore visual artefacting)"
  Group = -> [Group048,Group053]
FEATURE [App::DocumentObjectGroup] Group020  label="Export"
  Group = -> [Group036,Group037]
